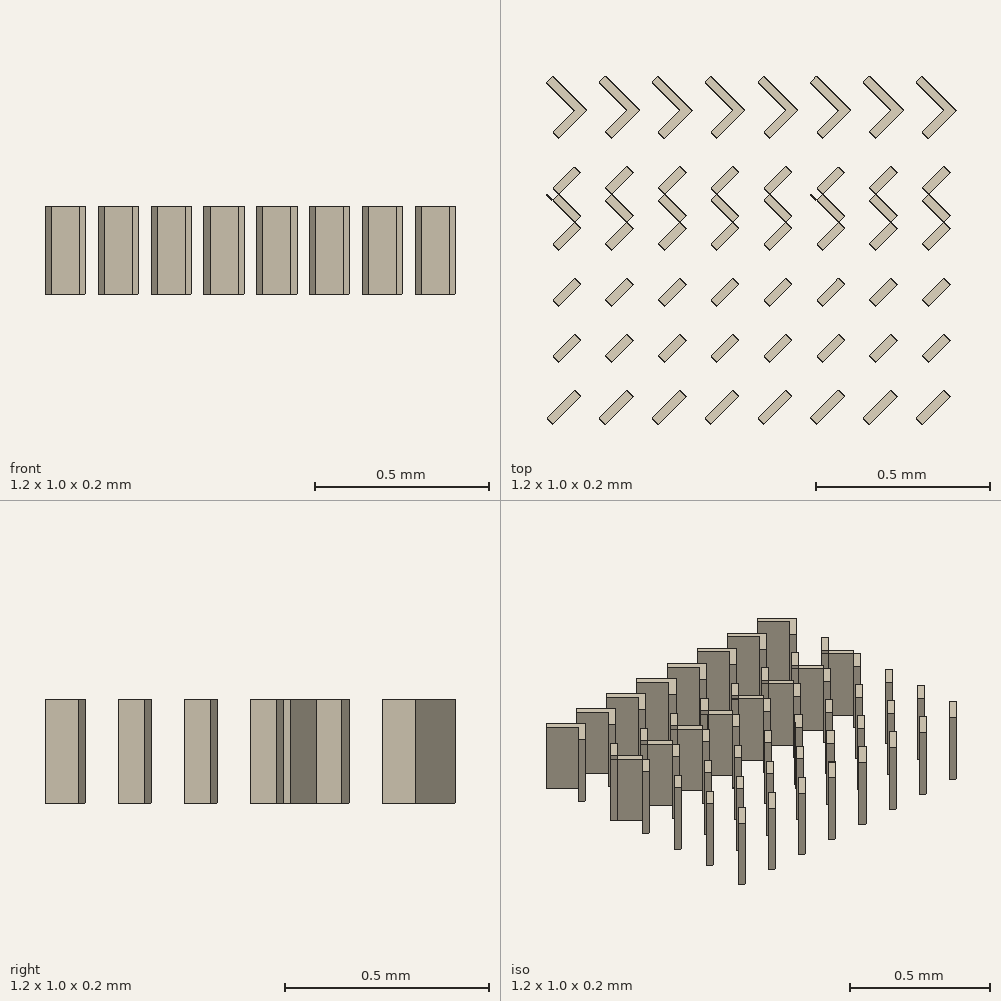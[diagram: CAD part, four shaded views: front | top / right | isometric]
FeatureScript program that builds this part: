
annotation { "Feature Type Name" : "Feature", "Feature Type Description" : "" }
export const myFeature = defineFeature(function(context is Context, id is Id, definition is map)
    precondition{}
    {
        {
            var Q0;
            Q0=qCreatedBy(makeId("Top.planeOp"),FACE);
            var sketch = newSketch(context, id + "F0", { "sketchPlane" : qUnion([Q0])});
            skLineSegment(sketch, "E0.bottom", {"start": v(-3.83, 2.01) * mm, "end": v(-3.93, 2.1) * mm});
            skLineSegment(sketch, "E0.top", {"start": v(-3.81, 2.03) * mm, "end": v(-3.91, 2.13) * mm});
            skLineSegment(sketch, "E0.left", {"start": v(-3.9, 1.93) * mm, "end": v(-3.9, 1.95) * mm});
            skLineSegment(sketch, "E0.right", {"start": v(-3.93, 2.1) * mm, "end": v(-3.91, 2.13) * mm});
            skPoint(sketch, "E0.middle", {"position": v(-3.95, 1.99) * mm});
            skLineSegment(sketch, "E1.bottom", {"start": v(-3.93, 1.95) * mm, "end": v(-3.83, 2.05) * mm});
            skLineSegment(sketch, "E1.top", {"start": v(-3.91, 1.93) * mm, "end": v(-3.81, 2.03) * mm});
            skLineSegment(sketch, "E1.left", {"start": v(-3.93, 1.95) * mm, "end": v(-3.91, 1.93) * mm});
            skLineSegment(sketch, "E1.right", {"start": v(-3.83, 2.05) * mm, "end": v(-3.81, 2.03) * mm});
            skPoint(sketch, "E1.middle", {"position": v(-3.87, 1.99) * mm});
            skLineSegment(sketch, "E2.bottom", {"start": v(-3.83, 1.85) * mm, "end": v(-3.93, 1.95) * mm});
            skLineSegment(sketch, "E2.top", {"start": v(-3.81, 1.87) * mm, "end": v(-3.91, 1.97) * mm});
            skLineSegment(sketch, "E2.left", {"start": v(-3.9, 1.77) * mm, "end": v(-3.9, 1.79) * mm});
            skLineSegment(sketch, "E2.right", {"start": v(-3.93, 1.95) * mm, "end": v(-3.91, 1.97) * mm});
            skPoint(sketch, "E2.middle", {"position": v(-3.95, 1.83) * mm});
            skLineSegment(sketch, "E3.bottom", {"start": v(-3.93, 1.79) * mm, "end": v(-3.83, 1.89) * mm});
            skLineSegment(sketch, "E3.top", {"start": v(-3.91, 1.77) * mm, "end": v(-3.81, 1.87) * mm});
            skLineSegment(sketch, "E3.left", {"start": v(-3.93, 1.79) * mm, "end": v(-3.91, 1.77) * mm});
            skLineSegment(sketch, "E3.right", {"start": v(-3.83, 1.89) * mm, "end": v(-3.81, 1.87) * mm});
            skPoint(sketch, "E3.middle", {"position": v(-3.87, 1.83) * mm});
            skLineSegment(sketch, "E4.bottom", {"start": v(-3.83, 1.69) * mm, "end": v(-3.93, 1.79) * mm});
            skLineSegment(sketch, "E4.top", {"start": v(-3.81, 1.7) * mm, "end": v(-3.9, 1.8) * mm});
            skLineSegment(sketch, "E4.left", {"start": v(-3.9, 1.6) * mm, "end": v(-3.9, 1.62) * mm});
            skLineSegment(sketch, "E4.right", {"start": v(-3.93, 1.79) * mm, "end": v(-3.9, 1.8) * mm});
            skPoint(sketch, "E4.middle", {"position": v(-3.95, 1.67) * mm});
            skLineSegment(sketch, "E5.bottom", {"start": v(-3.93, 1.63) * mm, "end": v(-3.83, 1.72) * mm});
            skLineSegment(sketch, "E5.top", {"start": v(-3.9, 1.6) * mm, "end": v(-3.81, 1.7) * mm});
            skLineSegment(sketch, "E5.left", {"start": v(-3.93, 1.63) * mm, "end": v(-3.9, 1.6) * mm});
            skLineSegment(sketch, "E5.right", {"start": v(-3.83, 1.72) * mm, "end": v(-3.81, 1.7) * mm});
            skPoint(sketch, "E5.middle", {"position": v(-3.87, 1.67) * mm});
            skLineSegment(sketch, "E6.bottom", {"start": v(-3.83, 1.53) * mm, "end": v(-3.93, 1.63) * mm});
            skLineSegment(sketch, "E6.top", {"start": v(-3.81, 1.54) * mm, "end": v(-3.9, 1.64) * mm});
            skLineSegment(sketch, "E6.left", {"start": v(-3.9, 1.45) * mm, "end": v(-3.9, 1.46) * mm});
            skLineSegment(sketch, "E6.right", {"start": v(-3.93, 1.63) * mm, "end": v(-3.9, 1.64) * mm});
            skPoint(sketch, "E6.middle", {"position": v(-3.95, 1.5) * mm});
            skLineSegment(sketch, "E7.bottom", {"start": v(-3.93, 1.46) * mm, "end": v(-3.83, 1.56) * mm});
            skLineSegment(sketch, "E7.top", {"start": v(-3.9, 1.45) * mm, "end": v(-3.81, 1.54) * mm});
            skLineSegment(sketch, "E7.left", {"start": v(-3.93, 1.46) * mm, "end": v(-3.9, 1.45) * mm});
            skLineSegment(sketch, "E7.right", {"start": v(-3.83, 1.56) * mm, "end": v(-3.81, 1.54) * mm});
            skPoint(sketch, "E7.middle", {"position": v(-3.87, 1.5) * mm});
            skLineSegment(sketch, "E8.bottom", {"start": v(-3.83, 1.36) * mm, "end": v(-3.93, 1.46) * mm});
            skLineSegment(sketch, "E8.top", {"start": v(-3.81, 1.38) * mm, "end": v(-3.9, 1.48) * mm});
            skLineSegment(sketch, "E8.left", {"start": v(-3.9, 1.28) * mm, "end": v(-3.9, 1.3) * mm});
            skLineSegment(sketch, "E8.right", {"start": v(-3.93, 1.46) * mm, "end": v(-3.9, 1.48) * mm});
            skPoint(sketch, "E8.middle", {"position": v(-3.95, 1.34) * mm});
            skLineSegment(sketch, "E9.bottom", {"start": v(-3.93, 1.3) * mm, "end": v(-3.83, 1.4) * mm});
            skLineSegment(sketch, "E9.top", {"start": v(-3.9, 1.28) * mm, "end": v(-3.81, 1.38) * mm});
            skLineSegment(sketch, "E9.left", {"start": v(-3.93, 1.3) * mm, "end": v(-3.9, 1.28) * mm});
            skLineSegment(sketch, "E9.right", {"start": v(-3.83, 1.4) * mm, "end": v(-3.81, 1.38) * mm});
            skPoint(sketch, "E9.middle", {"position": v(-3.87, 1.34) * mm});
            skLineSegment(sketch, "E10.bottom", {"start": v(-3.83, 1.2) * mm, "end": v(-3.93, 1.3) * mm});
            skLineSegment(sketch, "E10.top", {"start": v(-3.81, 1.22) * mm, "end": v(-3.9, 1.32) * mm});
            skLineSegment(sketch, "E10.left", {"start": v(-3.9, 1.12) * mm, "end": v(-3.9, 1.14) * mm});
            skLineSegment(sketch, "E10.right", {"start": v(-3.93, 1.3) * mm, "end": v(-3.9, 1.32) * mm});
            skPoint(sketch, "E10.middle", {"position": v(-3.95, 1.18) * mm});
            skLineSegment(sketch, "E11.bottom", {"start": v(-3.93, 1.14) * mm, "end": v(-3.83, 1.24) * mm});
            skLineSegment(sketch, "E11.top", {"start": v(-3.9, 1.12) * mm, "end": v(-3.81, 1.22) * mm});
            skLineSegment(sketch, "E11.left", {"start": v(-3.93, 1.14) * mm, "end": v(-3.9, 1.12) * mm});
            skLineSegment(sketch, "E11.right", {"start": v(-3.83, 1.24) * mm, "end": v(-3.81, 1.22) * mm});
            skPoint(sketch, "E11.middle", {"position": v(-3.87, 1.18) * mm});
            skLineSegment(sketch, "E12.0.1.0", {"start": v(-3.83, 3.56) * mm, "end": v(-3.93, 3.66) * mm});
            skLineSegment(sketch, "E12.0.1.1", {"start": v(-3.83, 3.24) * mm, "end": v(-3.93, 3.33) * mm});
            skPoint(sketch, "E12.0.1.2", {"position": v(-3.87, 4.02) * mm});
            skLineSegment(sketch, "E12.0.1.3", {"start": v(-3.81, 4.06) * mm, "end": v(-3.91, 4.16) * mm});
            skPoint(sketch, "E12.0.1.4", {"position": v(-3.95, 3.37) * mm});
            skLineSegment(sketch, "E12.0.1.5", {"start": v(-3.83, 4.04) * mm, "end": v(-3.93, 4.14) * mm});
            skPoint(sketch, "E12.0.1.6", {"position": v(-3.95, 3.54) * mm});
            skPoint(sketch, "E12.0.1.7", {"position": v(-3.95, 3.86) * mm});
            skPoint(sketch, "E12.0.1.8", {"position": v(-3.87, 3.37) * mm});
            skPoint(sketch, "E12.0.1.9", {"position": v(-3.87, 3.7) * mm});
            skLineSegment(sketch, "E12.0.1.10", {"start": v(-3.83, 3.4) * mm, "end": v(-3.93, 3.5) * mm});
            skPoint(sketch, "E12.0.1.11", {"position": v(-3.87, 3.54) * mm});
            skPoint(sketch, "E12.0.1.12", {"position": v(-3.87, 3.21) * mm});
            skLineSegment(sketch, "E12.0.1.13", {"start": v(-3.83, 3.72) * mm, "end": v(-3.93, 3.82) * mm});
            skPoint(sketch, "E12.0.1.14", {"position": v(-3.95, 4.02) * mm});
            skPoint(sketch, "E12.0.1.15", {"position": v(-3.95, 3.7) * mm});
            skLineSegment(sketch, "E12.0.1.16", {"start": v(-3.83, 3.88) * mm, "end": v(-3.93, 3.98) * mm});
            skPoint(sketch, "E12.0.1.17", {"position": v(-3.95, 3.21) * mm});
            skPoint(sketch, "E12.0.1.18", {"position": v(-3.87, 3.86) * mm});
            skLineSegment(sketch, "E12.0.1.19", {"start": v(-3.81, 3.41) * mm, "end": v(-3.9, 3.51) * mm});
            skLineSegment(sketch, "E12.0.1.20", {"start": v(-3.93, 3.98) * mm, "end": v(-3.83, 4.08) * mm});
            skLineSegment(sketch, "E12.0.1.21", {"start": v(-3.91, 3.8) * mm, "end": v(-3.81, 3.9) * mm});
            skLineSegment(sketch, "E12.0.1.22", {"start": v(-3.81, 3.58) * mm, "end": v(-3.9, 3.68) * mm});
            skLineSegment(sketch, "E12.0.1.23", {"start": v(-3.9, 3.32) * mm, "end": v(-3.81, 3.41) * mm});
            skLineSegment(sketch, "E12.0.1.24", {"start": v(-3.9, 3.64) * mm, "end": v(-3.81, 3.74) * mm});
            skLineSegment(sketch, "E12.0.1.25", {"start": v(-3.93, 3.5) * mm, "end": v(-3.83, 3.6) * mm});
            skLineSegment(sketch, "E12.0.1.26", {"start": v(-3.93, 3.17) * mm, "end": v(-3.83, 3.27) * mm});
            skLineSegment(sketch, "E12.0.1.27", {"start": v(-3.9, 3.48) * mm, "end": v(-3.81, 3.58) * mm});
            skLineSegment(sketch, "E12.0.1.28", {"start": v(-3.93, 3.33) * mm, "end": v(-3.83, 3.43) * mm});
            skLineSegment(sketch, "E12.0.1.29", {"start": v(-3.9, 3.15) * mm, "end": v(-3.81, 3.25) * mm});
            skLineSegment(sketch, "E12.0.1.30", {"start": v(-3.93, 3.66) * mm, "end": v(-3.83, 3.76) * mm});
            skLineSegment(sketch, "E12.0.1.31", {"start": v(-3.93, 3.82) * mm, "end": v(-3.83, 3.92) * mm});
            skLineSegment(sketch, "E12.0.1.32", {"start": v(-3.91, 3.96) * mm, "end": v(-3.81, 4.06) * mm});
            skLineSegment(sketch, "E12.0.1.33", {"start": v(-3.93, 4.14) * mm, "end": v(-3.91, 4.16) * mm});
            skLineSegment(sketch, "E12.0.1.34", {"start": v(-3.81, 3.74) * mm, "end": v(-3.9, 3.84) * mm});
            skLineSegment(sketch, "E12.0.1.35", {"start": v(-3.81, 3.25) * mm, "end": v(-3.9, 3.35) * mm});
            skLineSegment(sketch, "E12.0.1.36", {"start": v(-3.81, 3.9) * mm, "end": v(-3.91, 4) * mm});
            skLineSegment(sketch, "E12.0.1.37", {"start": v(-3.83, 3.92) * mm, "end": v(-3.81, 3.9) * mm});
            skLineSegment(sketch, "E12.0.1.38", {"start": v(-3.83, 3.6) * mm, "end": v(-3.81, 3.58) * mm});
            skLineSegment(sketch, "E12.0.1.39", {"start": v(-3.83, 3.27) * mm, "end": v(-3.81, 3.25) * mm});
            skLineSegment(sketch, "E12.0.1.40", {"start": v(-3.83, 3.76) * mm, "end": v(-3.81, 3.74) * mm});
            skLineSegment(sketch, "E12.0.1.41", {"start": v(-3.83, 3.43) * mm, "end": v(-3.81, 3.41) * mm});
            skLineSegment(sketch, "E12.0.1.42", {"start": v(-3.83, 4.08) * mm, "end": v(-3.81, 4.06) * mm});
            skLineSegment(sketch, "E12.0.1.43", {"start": v(-3.93, 3.82) * mm, "end": v(-3.9, 3.84) * mm});
            skLineSegment(sketch, "E12.0.1.44", {"start": v(-3.93, 3.82) * mm, "end": v(-3.91, 3.8) * mm});
            skLineSegment(sketch, "E12.0.1.45", {"start": v(-3.93, 3.17) * mm, "end": v(-3.9, 3.15) * mm});
            skLineSegment(sketch, "E12.0.1.46", {"start": v(-3.9, 3.8) * mm, "end": v(-3.9, 3.82) * mm});
            skLineSegment(sketch, "E12.0.1.47", {"start": v(-3.9, 3.15) * mm, "end": v(-3.9, 3.17) * mm});
            skLineSegment(sketch, "E12.0.1.48", {"start": v(-3.9, 3.96) * mm, "end": v(-3.9, 3.98) * mm});
            skLineSegment(sketch, "E12.0.1.49", {"start": v(-3.93, 3.33) * mm, "end": v(-3.9, 3.32) * mm});
            skLineSegment(sketch, "E12.0.1.50", {"start": v(-3.93, 3.66) * mm, "end": v(-3.9, 3.64) * mm});
            skLineSegment(sketch, "E12.0.1.51", {"start": v(-3.9, 3.64) * mm, "end": v(-3.9, 3.66) * mm});
            skLineSegment(sketch, "E12.0.1.52", {"start": v(-3.93, 3.5) * mm, "end": v(-3.9, 3.48) * mm});
            skLineSegment(sketch, "E12.0.1.53", {"start": v(-3.93, 3.66) * mm, "end": v(-3.9, 3.68) * mm});
            skLineSegment(sketch, "E12.0.1.54", {"start": v(-3.93, 3.33) * mm, "end": v(-3.9, 3.35) * mm});
            skLineSegment(sketch, "E12.0.1.55", {"start": v(-3.93, 3.98) * mm, "end": v(-3.91, 4) * mm});
            skLineSegment(sketch, "E12.0.1.56", {"start": v(-3.93, 3.98) * mm, "end": v(-3.91, 3.96) * mm});
            skLineSegment(sketch, "E12.0.1.57", {"start": v(-3.93, 3.5) * mm, "end": v(-3.9, 3.51) * mm});
            skLineSegment(sketch, "E12.0.1.58", {"start": v(-3.9, 3.48) * mm, "end": v(-3.9, 3.5) * mm});
            skLineSegment(sketch, "E12.0.1.59", {"start": v(-3.9, 3.32) * mm, "end": v(-3.9, 3.33) * mm});
            skLineSegment(sketch, "E12.1.0.0", {"start": v(-3.68, 1.53) * mm, "end": v(-3.78, 1.63) * mm});
            skLineSegment(sketch, "E12.1.0.1", {"start": v(-3.68, 1.2) * mm, "end": v(-3.78, 1.3) * mm});
            skPoint(sketch, "E12.1.0.2", {"position": v(-3.72, 1.99) * mm});
            skLineSegment(sketch, "E12.1.0.3", {"start": v(-3.66, 2.03) * mm, "end": v(-3.76, 2.13) * mm});
            skPoint(sketch, "E12.1.0.4", {"position": v(-3.8, 1.34) * mm});
            skLineSegment(sketch, "E12.1.0.5", {"start": v(-3.68, 2.01) * mm, "end": v(-3.78, 2.1) * mm});
            skPoint(sketch, "E12.1.0.6", {"position": v(-3.8, 1.5) * mm});
            skPoint(sketch, "E12.1.0.7", {"position": v(-3.8, 1.83) * mm});
            skPoint(sketch, "E12.1.0.8", {"position": v(-3.72, 1.34) * mm});
            skPoint(sketch, "E12.1.0.9", {"position": v(-3.72, 1.67) * mm});
            skLineSegment(sketch, "E12.1.0.10", {"start": v(-3.68, 1.36) * mm, "end": v(-3.78, 1.46) * mm});
            skPoint(sketch, "E12.1.0.11", {"position": v(-3.72, 1.5) * mm});
            skPoint(sketch, "E12.1.0.12", {"position": v(-3.72, 1.18) * mm});
            skLineSegment(sketch, "E12.1.0.13", {"start": v(-3.68, 1.69) * mm, "end": v(-3.78, 1.79) * mm});
            skPoint(sketch, "E12.1.0.14", {"position": v(-3.8, 1.99) * mm});
            skPoint(sketch, "E12.1.0.15", {"position": v(-3.8, 1.67) * mm});
            skLineSegment(sketch, "E12.1.0.16", {"start": v(-3.68, 1.85) * mm, "end": v(-3.78, 1.95) * mm});
            skPoint(sketch, "E12.1.0.17", {"position": v(-3.8, 1.18) * mm});
            skPoint(sketch, "E12.1.0.18", {"position": v(-3.72, 1.83) * mm});
            skLineSegment(sketch, "E12.1.0.19", {"start": v(-3.66, 1.38) * mm, "end": v(-3.76, 1.48) * mm});
            skLineSegment(sketch, "E12.1.0.20", {"start": v(-3.78, 1.95) * mm, "end": v(-3.68, 2.05) * mm});
            skLineSegment(sketch, "E12.1.0.21", {"start": v(-3.76, 1.77) * mm, "end": v(-3.66, 1.87) * mm});
            skLineSegment(sketch, "E12.1.0.22", {"start": v(-3.66, 1.54) * mm, "end": v(-3.76, 1.64) * mm});
            skLineSegment(sketch, "E12.1.0.23", {"start": v(-3.76, 1.28) * mm, "end": v(-3.66, 1.38) * mm});
            skLineSegment(sketch, "E12.1.0.24", {"start": v(-3.76, 1.6) * mm, "end": v(-3.66, 1.7) * mm});
            skLineSegment(sketch, "E12.1.0.25", {"start": v(-3.78, 1.46) * mm, "end": v(-3.68, 1.56) * mm});
            skLineSegment(sketch, "E12.1.0.26", {"start": v(-3.78, 1.14) * mm, "end": v(-3.68, 1.24) * mm});
            skLineSegment(sketch, "E12.1.0.27", {"start": v(-3.76, 1.45) * mm, "end": v(-3.66, 1.54) * mm});
            skLineSegment(sketch, "E12.1.0.28", {"start": v(-3.78, 1.3) * mm, "end": v(-3.68, 1.4) * mm});
            skLineSegment(sketch, "E12.1.0.29", {"start": v(-3.76, 1.12) * mm, "end": v(-3.66, 1.22) * mm});
            skLineSegment(sketch, "E12.1.0.30", {"start": v(-3.78, 1.63) * mm, "end": v(-3.68, 1.72) * mm});
            skLineSegment(sketch, "E12.1.0.31", {"start": v(-3.78, 1.79) * mm, "end": v(-3.68, 1.89) * mm});
            skLineSegment(sketch, "E12.1.0.32", {"start": v(-3.76, 1.93) * mm, "end": v(-3.66, 2.03) * mm});
            skLineSegment(sketch, "E12.1.0.33", {"start": v(-3.78, 2.1) * mm, "end": v(-3.76, 2.13) * mm});
            skLineSegment(sketch, "E12.1.0.34", {"start": v(-3.66, 1.7) * mm, "end": v(-3.76, 1.8) * mm});
            skLineSegment(sketch, "E12.1.0.35", {"start": v(-3.66, 1.22) * mm, "end": v(-3.76, 1.32) * mm});
            skLineSegment(sketch, "E12.1.0.36", {"start": v(-3.66, 1.87) * mm, "end": v(-3.76, 1.97) * mm});
            skLineSegment(sketch, "E12.1.0.37", {"start": v(-3.68, 1.89) * mm, "end": v(-3.66, 1.87) * mm});
            skLineSegment(sketch, "E12.1.0.38", {"start": v(-3.68, 1.56) * mm, "end": v(-3.66, 1.54) * mm});
            skLineSegment(sketch, "E12.1.0.39", {"start": v(-3.68, 1.24) * mm, "end": v(-3.66, 1.22) * mm});
            skLineSegment(sketch, "E12.1.0.40", {"start": v(-3.68, 1.72) * mm, "end": v(-3.66, 1.7) * mm});
            skLineSegment(sketch, "E12.1.0.41", {"start": v(-3.68, 1.4) * mm, "end": v(-3.66, 1.38) * mm});
            skLineSegment(sketch, "E12.1.0.42", {"start": v(-3.68, 2.05) * mm, "end": v(-3.66, 2.03) * mm});
            skLineSegment(sketch, "E12.1.0.43", {"start": v(-3.78, 1.79) * mm, "end": v(-3.76, 1.8) * mm});
            skLineSegment(sketch, "E12.1.0.44", {"start": v(-3.78, 1.79) * mm, "end": v(-3.76, 1.77) * mm});
            skLineSegment(sketch, "E12.1.0.45", {"start": v(-3.78, 1.14) * mm, "end": v(-3.76, 1.12) * mm});
            skLineSegment(sketch, "E12.1.0.46", {"start": v(-3.76, 1.77) * mm, "end": v(-3.74, 1.79) * mm});
            skLineSegment(sketch, "E12.1.0.47", {"start": v(-3.76, 1.12) * mm, "end": v(-3.74, 1.14) * mm});
            skLineSegment(sketch, "E12.1.0.48", {"start": v(-3.76, 1.93) * mm, "end": v(-3.74, 1.95) * mm});
            skLineSegment(sketch, "E12.1.0.49", {"start": v(-3.78, 1.3) * mm, "end": v(-3.76, 1.28) * mm});
            skLineSegment(sketch, "E12.1.0.50", {"start": v(-3.78, 1.63) * mm, "end": v(-3.76, 1.6) * mm});
            skLineSegment(sketch, "E12.1.0.51", {"start": v(-3.76, 1.6) * mm, "end": v(-3.74, 1.62) * mm});
            skLineSegment(sketch, "E12.1.0.52", {"start": v(-3.78, 1.46) * mm, "end": v(-3.76, 1.45) * mm});
            skLineSegment(sketch, "E12.1.0.53", {"start": v(-3.78, 1.63) * mm, "end": v(-3.76, 1.64) * mm});
            skLineSegment(sketch, "E12.1.0.54", {"start": v(-3.78, 1.3) * mm, "end": v(-3.76, 1.32) * mm});
            skLineSegment(sketch, "E12.1.0.55", {"start": v(-3.78, 1.95) * mm, "end": v(-3.76, 1.97) * mm});
            skLineSegment(sketch, "E12.1.0.56", {"start": v(-3.78, 1.95) * mm, "end": v(-3.76, 1.93) * mm});
            skLineSegment(sketch, "E12.1.0.57", {"start": v(-3.78, 1.46) * mm, "end": v(-3.76, 1.48) * mm});
            skLineSegment(sketch, "E12.1.0.58", {"start": v(-3.76, 1.45) * mm, "end": v(-3.74, 1.46) * mm});
            skLineSegment(sketch, "E12.1.0.59", {"start": v(-3.76, 1.28) * mm, "end": v(-3.74, 1.3) * mm});
            skLineSegment(sketch, "E12.1.1.0", {"start": v(-3.68, 3.56) * mm, "end": v(-3.78, 3.66) * mm});
            skLineSegment(sketch, "E12.1.1.1", {"start": v(-3.68, 3.24) * mm, "end": v(-3.78, 3.33) * mm});
            skPoint(sketch, "E12.1.1.2", {"position": v(-3.72, 4.02) * mm});
            skLineSegment(sketch, "E12.1.1.3", {"start": v(-3.66, 4.06) * mm, "end": v(-3.76, 4.16) * mm});
            skPoint(sketch, "E12.1.1.4", {"position": v(-3.8, 3.37) * mm});
            skLineSegment(sketch, "E12.1.1.5", {"start": v(-3.68, 4.04) * mm, "end": v(-3.78, 4.14) * mm});
            skPoint(sketch, "E12.1.1.6", {"position": v(-3.8, 3.54) * mm});
            skPoint(sketch, "E12.1.1.7", {"position": v(-3.8, 3.86) * mm});
            skPoint(sketch, "E12.1.1.8", {"position": v(-3.72, 3.37) * mm});
            skPoint(sketch, "E12.1.1.9", {"position": v(-3.72, 3.7) * mm});
            skLineSegment(sketch, "E12.1.1.10", {"start": v(-3.68, 3.4) * mm, "end": v(-3.78, 3.5) * mm});
            skPoint(sketch, "E12.1.1.11", {"position": v(-3.72, 3.54) * mm});
            skPoint(sketch, "E12.1.1.12", {"position": v(-3.72, 3.21) * mm});
            skLineSegment(sketch, "E12.1.1.13", {"start": v(-3.68, 3.72) * mm, "end": v(-3.78, 3.82) * mm});
            skPoint(sketch, "E12.1.1.14", {"position": v(-3.8, 4.02) * mm});
            skPoint(sketch, "E12.1.1.15", {"position": v(-3.8, 3.7) * mm});
            skLineSegment(sketch, "E12.1.1.16", {"start": v(-3.68, 3.88) * mm, "end": v(-3.78, 3.98) * mm});
            skPoint(sketch, "E12.1.1.17", {"position": v(-3.8, 3.21) * mm});
            skPoint(sketch, "E12.1.1.18", {"position": v(-3.72, 3.86) * mm});
            skLineSegment(sketch, "E12.1.1.19", {"start": v(-3.66, 3.41) * mm, "end": v(-3.76, 3.51) * mm});
            skLineSegment(sketch, "E12.1.1.20", {"start": v(-3.78, 3.98) * mm, "end": v(-3.68, 4.08) * mm});
            skLineSegment(sketch, "E12.1.1.21", {"start": v(-3.76, 3.8) * mm, "end": v(-3.66, 3.9) * mm});
            skLineSegment(sketch, "E12.1.1.22", {"start": v(-3.66, 3.58) * mm, "end": v(-3.76, 3.68) * mm});
            skLineSegment(sketch, "E12.1.1.23", {"start": v(-3.76, 3.32) * mm, "end": v(-3.66, 3.41) * mm});
            skLineSegment(sketch, "E12.1.1.24", {"start": v(-3.76, 3.64) * mm, "end": v(-3.66, 3.74) * mm});
            skLineSegment(sketch, "E12.1.1.25", {"start": v(-3.78, 3.5) * mm, "end": v(-3.68, 3.6) * mm});
            skLineSegment(sketch, "E12.1.1.26", {"start": v(-3.78, 3.17) * mm, "end": v(-3.68, 3.27) * mm});
            skLineSegment(sketch, "E12.1.1.27", {"start": v(-3.76, 3.48) * mm, "end": v(-3.66, 3.58) * mm});
            skLineSegment(sketch, "E12.1.1.28", {"start": v(-3.78, 3.33) * mm, "end": v(-3.68, 3.43) * mm});
            skLineSegment(sketch, "E12.1.1.29", {"start": v(-3.76, 3.15) * mm, "end": v(-3.66, 3.25) * mm});
            skLineSegment(sketch, "E12.1.1.30", {"start": v(-3.78, 3.66) * mm, "end": v(-3.68, 3.76) * mm});
            skLineSegment(sketch, "E12.1.1.31", {"start": v(-3.78, 3.82) * mm, "end": v(-3.68, 3.92) * mm});
            skLineSegment(sketch, "E12.1.1.32", {"start": v(-3.76, 3.96) * mm, "end": v(-3.66, 4.06) * mm});
            skLineSegment(sketch, "E12.1.1.33", {"start": v(-3.78, 4.14) * mm, "end": v(-3.76, 4.16) * mm});
            skLineSegment(sketch, "E12.1.1.34", {"start": v(-3.66, 3.74) * mm, "end": v(-3.76, 3.84) * mm});
            skLineSegment(sketch, "E12.1.1.35", {"start": v(-3.66, 3.25) * mm, "end": v(-3.76, 3.35) * mm});
            skLineSegment(sketch, "E12.1.1.36", {"start": v(-3.66, 3.9) * mm, "end": v(-3.76, 4) * mm});
            skLineSegment(sketch, "E12.1.1.37", {"start": v(-3.68, 3.92) * mm, "end": v(-3.66, 3.9) * mm});
            skLineSegment(sketch, "E12.1.1.38", {"start": v(-3.68, 3.6) * mm, "end": v(-3.66, 3.58) * mm});
            skLineSegment(sketch, "E12.1.1.39", {"start": v(-3.68, 3.27) * mm, "end": v(-3.66, 3.25) * mm});
            skLineSegment(sketch, "E12.1.1.40", {"start": v(-3.68, 3.76) * mm, "end": v(-3.66, 3.74) * mm});
            skLineSegment(sketch, "E12.1.1.41", {"start": v(-3.68, 3.43) * mm, "end": v(-3.66, 3.41) * mm});
            skLineSegment(sketch, "E12.1.1.42", {"start": v(-3.68, 4.08) * mm, "end": v(-3.66, 4.06) * mm});
            skLineSegment(sketch, "E12.1.1.43", {"start": v(-3.78, 3.82) * mm, "end": v(-3.76, 3.84) * mm});
            skLineSegment(sketch, "E12.1.1.44", {"start": v(-3.78, 3.82) * mm, "end": v(-3.76, 3.8) * mm});
            skLineSegment(sketch, "E12.1.1.45", {"start": v(-3.78, 3.17) * mm, "end": v(-3.76, 3.15) * mm});
            skLineSegment(sketch, "E12.1.1.46", {"start": v(-3.76, 3.8) * mm, "end": v(-3.74, 3.82) * mm});
            skLineSegment(sketch, "E12.1.1.47", {"start": v(-3.76, 3.15) * mm, "end": v(-3.74, 3.17) * mm});
            skLineSegment(sketch, "E12.1.1.48", {"start": v(-3.76, 3.96) * mm, "end": v(-3.74, 3.98) * mm});
            skLineSegment(sketch, "E12.1.1.49", {"start": v(-3.78, 3.33) * mm, "end": v(-3.76, 3.32) * mm});
            skLineSegment(sketch, "E12.1.1.50", {"start": v(-3.78, 3.66) * mm, "end": v(-3.76, 3.64) * mm});
            skLineSegment(sketch, "E12.1.1.51", {"start": v(-3.76, 3.64) * mm, "end": v(-3.74, 3.66) * mm});
            skLineSegment(sketch, "E12.1.1.52", {"start": v(-3.78, 3.5) * mm, "end": v(-3.76, 3.48) * mm});
            skLineSegment(sketch, "E12.1.1.53", {"start": v(-3.78, 3.66) * mm, "end": v(-3.76, 3.68) * mm});
            skLineSegment(sketch, "E12.1.1.54", {"start": v(-3.78, 3.33) * mm, "end": v(-3.76, 3.35) * mm});
            skLineSegment(sketch, "E12.1.1.55", {"start": v(-3.78, 3.98) * mm, "end": v(-3.76, 4) * mm});
            skLineSegment(sketch, "E12.1.1.56", {"start": v(-3.78, 3.98) * mm, "end": v(-3.76, 3.96) * mm});
            skLineSegment(sketch, "E12.1.1.57", {"start": v(-3.78, 3.5) * mm, "end": v(-3.76, 3.51) * mm});
            skLineSegment(sketch, "E12.1.1.58", {"start": v(-3.76, 3.48) * mm, "end": v(-3.74, 3.5) * mm});
            skLineSegment(sketch, "E12.1.1.59", {"start": v(-3.76, 3.32) * mm, "end": v(-3.74, 3.33) * mm});
            skLineSegment(sketch, "E12.2.0.0", {"start": v(-3.52, 1.53) * mm, "end": v(-3.62, 1.63) * mm});
            skLineSegment(sketch, "E12.2.0.1", {"start": v(-3.52, 1.2) * mm, "end": v(-3.62, 1.3) * mm});
            skPoint(sketch, "E12.2.0.2", {"position": v(-3.56, 1.99) * mm});
            skLineSegment(sketch, "E12.2.0.3", {"start": v(-3.5, 2.03) * mm, "end": v(-3.6, 2.13) * mm});
            skPoint(sketch, "E12.2.0.4", {"position": v(-3.65, 1.34) * mm});
            skLineSegment(sketch, "E12.2.0.5", {"start": v(-3.52, 2.01) * mm, "end": v(-3.62, 2.1) * mm});
            skPoint(sketch, "E12.2.0.6", {"position": v(-3.65, 1.5) * mm});
            skPoint(sketch, "E12.2.0.7", {"position": v(-3.65, 1.83) * mm});
            skPoint(sketch, "E12.2.0.8", {"position": v(-3.56, 1.34) * mm});
            skPoint(sketch, "E12.2.0.9", {"position": v(-3.56, 1.67) * mm});
            skLineSegment(sketch, "E12.2.0.10", {"start": v(-3.52, 1.36) * mm, "end": v(-3.62, 1.46) * mm});
            skPoint(sketch, "E12.2.0.11", {"position": v(-3.56, 1.5) * mm});
            skPoint(sketch, "E12.2.0.12", {"position": v(-3.56, 1.18) * mm});
            skLineSegment(sketch, "E12.2.0.13", {"start": v(-3.52, 1.69) * mm, "end": v(-3.62, 1.79) * mm});
            skPoint(sketch, "E12.2.0.14", {"position": v(-3.65, 1.99) * mm});
            skPoint(sketch, "E12.2.0.15", {"position": v(-3.65, 1.67) * mm});
            skLineSegment(sketch, "E12.2.0.16", {"start": v(-3.52, 1.85) * mm, "end": v(-3.62, 1.95) * mm});
            skPoint(sketch, "E12.2.0.17", {"position": v(-3.65, 1.18) * mm});
            skPoint(sketch, "E12.2.0.18", {"position": v(-3.56, 1.83) * mm});
            skLineSegment(sketch, "E12.2.0.19", {"start": v(-3.5, 1.38) * mm, "end": v(-3.6, 1.48) * mm});
            skLineSegment(sketch, "E12.2.0.20", {"start": v(-3.62, 1.95) * mm, "end": v(-3.52, 2.05) * mm});
            skLineSegment(sketch, "E12.2.0.21", {"start": v(-3.6, 1.77) * mm, "end": v(-3.5, 1.87) * mm});
            skLineSegment(sketch, "E12.2.0.22", {"start": v(-3.5, 1.54) * mm, "end": v(-3.6, 1.64) * mm});
            skLineSegment(sketch, "E12.2.0.23", {"start": v(-3.6, 1.28) * mm, "end": v(-3.5, 1.38) * mm});
            skLineSegment(sketch, "E12.2.0.24", {"start": v(-3.6, 1.6) * mm, "end": v(-3.5, 1.7) * mm});
            skLineSegment(sketch, "E12.2.0.25", {"start": v(-3.62, 1.46) * mm, "end": v(-3.52, 1.56) * mm});
            skLineSegment(sketch, "E12.2.0.26", {"start": v(-3.62, 1.14) * mm, "end": v(-3.52, 1.24) * mm});
            skLineSegment(sketch, "E12.2.0.27", {"start": v(-3.6, 1.45) * mm, "end": v(-3.5, 1.54) * mm});
            skLineSegment(sketch, "E12.2.0.28", {"start": v(-3.62, 1.3) * mm, "end": v(-3.52, 1.4) * mm});
            skLineSegment(sketch, "E12.2.0.29", {"start": v(-3.6, 1.12) * mm, "end": v(-3.5, 1.22) * mm});
            skLineSegment(sketch, "E12.2.0.30", {"start": v(-3.62, 1.63) * mm, "end": v(-3.52, 1.72) * mm});
            skLineSegment(sketch, "E12.2.0.31", {"start": v(-3.62, 1.79) * mm, "end": v(-3.52, 1.89) * mm});
            skLineSegment(sketch, "E12.2.0.32", {"start": v(-3.6, 1.93) * mm, "end": v(-3.5, 2.03) * mm});
            skLineSegment(sketch, "E12.2.0.33", {"start": v(-3.62, 2.1) * mm, "end": v(-3.6, 2.13) * mm});
            skLineSegment(sketch, "E12.2.0.34", {"start": v(-3.5, 1.7) * mm, "end": v(-3.6, 1.8) * mm});
            skLineSegment(sketch, "E12.2.0.35", {"start": v(-3.5, 1.22) * mm, "end": v(-3.6, 1.32) * mm});
            skLineSegment(sketch, "E12.2.0.36", {"start": v(-3.5, 1.87) * mm, "end": v(-3.6, 1.97) * mm});
            skLineSegment(sketch, "E12.2.0.37", {"start": v(-3.52, 1.89) * mm, "end": v(-3.5, 1.87) * mm});
            skLineSegment(sketch, "E12.2.0.38", {"start": v(-3.52, 1.56) * mm, "end": v(-3.5, 1.54) * mm});
            skLineSegment(sketch, "E12.2.0.39", {"start": v(-3.52, 1.24) * mm, "end": v(-3.5, 1.22) * mm});
            skLineSegment(sketch, "E12.2.0.40", {"start": v(-3.52, 1.72) * mm, "end": v(-3.5, 1.7) * mm});
            skLineSegment(sketch, "E12.2.0.41", {"start": v(-3.52, 1.4) * mm, "end": v(-3.5, 1.38) * mm});
            skLineSegment(sketch, "E12.2.0.42", {"start": v(-3.52, 2.05) * mm, "end": v(-3.5, 2.03) * mm});
            skLineSegment(sketch, "E12.2.0.43", {"start": v(-3.62, 1.79) * mm, "end": v(-3.6, 1.8) * mm});
            skLineSegment(sketch, "E12.2.0.44", {"start": v(-3.62, 1.79) * mm, "end": v(-3.6, 1.77) * mm});
            skLineSegment(sketch, "E12.2.0.45", {"start": v(-3.62, 1.14) * mm, "end": v(-3.6, 1.12) * mm});
            skLineSegment(sketch, "E12.2.0.46", {"start": v(-3.6, 1.77) * mm, "end": v(-3.59, 1.79) * mm});
            skLineSegment(sketch, "E12.2.0.47", {"start": v(-3.6, 1.12) * mm, "end": v(-3.59, 1.14) * mm});
            skLineSegment(sketch, "E12.2.0.48", {"start": v(-3.6, 1.93) * mm, "end": v(-3.59, 1.95) * mm});
            skLineSegment(sketch, "E12.2.0.49", {"start": v(-3.62, 1.3) * mm, "end": v(-3.6, 1.28) * mm});
            skLineSegment(sketch, "E12.2.0.50", {"start": v(-3.62, 1.63) * mm, "end": v(-3.6, 1.6) * mm});
            skLineSegment(sketch, "E12.2.0.51", {"start": v(-3.6, 1.6) * mm, "end": v(-3.59, 1.62) * mm});
            skLineSegment(sketch, "E12.2.0.52", {"start": v(-3.62, 1.46) * mm, "end": v(-3.6, 1.45) * mm});
            skLineSegment(sketch, "E12.2.0.53", {"start": v(-3.62, 1.63) * mm, "end": v(-3.6, 1.64) * mm});
            skLineSegment(sketch, "E12.2.0.54", {"start": v(-3.62, 1.3) * mm, "end": v(-3.6, 1.32) * mm});
            skLineSegment(sketch, "E12.2.0.55", {"start": v(-3.62, 1.95) * mm, "end": v(-3.6, 1.97) * mm});
            skLineSegment(sketch, "E12.2.0.56", {"start": v(-3.62, 1.95) * mm, "end": v(-3.6, 1.93) * mm});
            skLineSegment(sketch, "E12.2.0.57", {"start": v(-3.62, 1.46) * mm, "end": v(-3.6, 1.48) * mm});
            skLineSegment(sketch, "E12.2.0.58", {"start": v(-3.6, 1.45) * mm, "end": v(-3.59, 1.46) * mm});
            skLineSegment(sketch, "E12.2.0.59", {"start": v(-3.6, 1.28) * mm, "end": v(-3.59, 1.3) * mm});
            skLineSegment(sketch, "E12.2.1.0", {"start": v(-3.52, 3.56) * mm, "end": v(-3.62, 3.66) * mm});
            skLineSegment(sketch, "E12.2.1.1", {"start": v(-3.52, 3.24) * mm, "end": v(-3.62, 3.33) * mm});
            skPoint(sketch, "E12.2.1.2", {"position": v(-3.56, 4.02) * mm});
            skLineSegment(sketch, "E12.2.1.3", {"start": v(-3.5, 4.06) * mm, "end": v(-3.6, 4.16) * mm});
            skPoint(sketch, "E12.2.1.4", {"position": v(-3.65, 3.37) * mm});
            skLineSegment(sketch, "E12.2.1.5", {"start": v(-3.52, 4.04) * mm, "end": v(-3.62, 4.14) * mm});
            skPoint(sketch, "E12.2.1.6", {"position": v(-3.65, 3.54) * mm});
            skPoint(sketch, "E12.2.1.7", {"position": v(-3.65, 3.86) * mm});
            skPoint(sketch, "E12.2.1.8", {"position": v(-3.56, 3.37) * mm});
            skPoint(sketch, "E12.2.1.9", {"position": v(-3.56, 3.7) * mm});
            skLineSegment(sketch, "E12.2.1.10", {"start": v(-3.52, 3.4) * mm, "end": v(-3.62, 3.5) * mm});
            skPoint(sketch, "E12.2.1.11", {"position": v(-3.56, 3.54) * mm});
            skPoint(sketch, "E12.2.1.12", {"position": v(-3.56, 3.21) * mm});
            skLineSegment(sketch, "E12.2.1.13", {"start": v(-3.52, 3.72) * mm, "end": v(-3.62, 3.82) * mm});
            skPoint(sketch, "E12.2.1.14", {"position": v(-3.65, 4.02) * mm});
            skPoint(sketch, "E12.2.1.15", {"position": v(-3.65, 3.7) * mm});
            skLineSegment(sketch, "E12.2.1.16", {"start": v(-3.52, 3.88) * mm, "end": v(-3.62, 3.98) * mm});
            skPoint(sketch, "E12.2.1.17", {"position": v(-3.65, 3.21) * mm});
            skPoint(sketch, "E12.2.1.18", {"position": v(-3.56, 3.86) * mm});
            skLineSegment(sketch, "E12.2.1.19", {"start": v(-3.5, 3.41) * mm, "end": v(-3.6, 3.51) * mm});
            skLineSegment(sketch, "E12.2.1.20", {"start": v(-3.62, 3.98) * mm, "end": v(-3.52, 4.08) * mm});
            skLineSegment(sketch, "E12.2.1.21", {"start": v(-3.6, 3.8) * mm, "end": v(-3.5, 3.9) * mm});
            skLineSegment(sketch, "E12.2.1.22", {"start": v(-3.5, 3.58) * mm, "end": v(-3.6, 3.68) * mm});
            skLineSegment(sketch, "E12.2.1.23", {"start": v(-3.6, 3.32) * mm, "end": v(-3.5, 3.41) * mm});
            skLineSegment(sketch, "E12.2.1.24", {"start": v(-3.6, 3.64) * mm, "end": v(-3.5, 3.74) * mm});
            skLineSegment(sketch, "E12.2.1.25", {"start": v(-3.62, 3.5) * mm, "end": v(-3.52, 3.6) * mm});
            skLineSegment(sketch, "E12.2.1.26", {"start": v(-3.62, 3.17) * mm, "end": v(-3.52, 3.27) * mm});
            skLineSegment(sketch, "E12.2.1.27", {"start": v(-3.6, 3.48) * mm, "end": v(-3.5, 3.58) * mm});
            skLineSegment(sketch, "E12.2.1.28", {"start": v(-3.62, 3.33) * mm, "end": v(-3.52, 3.43) * mm});
            skLineSegment(sketch, "E12.2.1.29", {"start": v(-3.6, 3.15) * mm, "end": v(-3.5, 3.25) * mm});
            skLineSegment(sketch, "E12.2.1.30", {"start": v(-3.62, 3.66) * mm, "end": v(-3.52, 3.76) * mm});
            skLineSegment(sketch, "E12.2.1.31", {"start": v(-3.62, 3.82) * mm, "end": v(-3.52, 3.92) * mm});
            skLineSegment(sketch, "E12.2.1.32", {"start": v(-3.6, 3.96) * mm, "end": v(-3.5, 4.06) * mm});
            skLineSegment(sketch, "E12.2.1.33", {"start": v(-3.62, 4.14) * mm, "end": v(-3.6, 4.16) * mm});
            skLineSegment(sketch, "E12.2.1.34", {"start": v(-3.5, 3.74) * mm, "end": v(-3.6, 3.84) * mm});
            skLineSegment(sketch, "E12.2.1.35", {"start": v(-3.5, 3.25) * mm, "end": v(-3.6, 3.35) * mm});
            skLineSegment(sketch, "E12.2.1.36", {"start": v(-3.5, 3.9) * mm, "end": v(-3.6, 4) * mm});
            skLineSegment(sketch, "E12.2.1.37", {"start": v(-3.52, 3.92) * mm, "end": v(-3.5, 3.9) * mm});
            skLineSegment(sketch, "E12.2.1.38", {"start": v(-3.52, 3.6) * mm, "end": v(-3.5, 3.58) * mm});
            skLineSegment(sketch, "E12.2.1.39", {"start": v(-3.52, 3.27) * mm, "end": v(-3.5, 3.25) * mm});
            skLineSegment(sketch, "E12.2.1.40", {"start": v(-3.52, 3.76) * mm, "end": v(-3.5, 3.74) * mm});
            skLineSegment(sketch, "E12.2.1.41", {"start": v(-3.52, 3.43) * mm, "end": v(-3.5, 3.41) * mm});
            skLineSegment(sketch, "E12.2.1.42", {"start": v(-3.52, 4.08) * mm, "end": v(-3.5, 4.06) * mm});
            skLineSegment(sketch, "E12.2.1.43", {"start": v(-3.62, 3.82) * mm, "end": v(-3.6, 3.84) * mm});
            skLineSegment(sketch, "E12.2.1.44", {"start": v(-3.62, 3.82) * mm, "end": v(-3.6, 3.8) * mm});
            skLineSegment(sketch, "E12.2.1.45", {"start": v(-3.62, 3.17) * mm, "end": v(-3.6, 3.15) * mm});
            skLineSegment(sketch, "E12.2.1.46", {"start": v(-3.6, 3.8) * mm, "end": v(-3.59, 3.82) * mm});
            skLineSegment(sketch, "E12.2.1.47", {"start": v(-3.6, 3.15) * mm, "end": v(-3.59, 3.17) * mm});
            skLineSegment(sketch, "E12.2.1.48", {"start": v(-3.6, 3.96) * mm, "end": v(-3.59, 3.98) * mm});
            skLineSegment(sketch, "E12.2.1.49", {"start": v(-3.62, 3.33) * mm, "end": v(-3.6, 3.32) * mm});
            skLineSegment(sketch, "E12.2.1.50", {"start": v(-3.62, 3.66) * mm, "end": v(-3.6, 3.64) * mm});
            skLineSegment(sketch, "E12.2.1.51", {"start": v(-3.6, 3.64) * mm, "end": v(-3.59, 3.66) * mm});
            skLineSegment(sketch, "E12.2.1.52", {"start": v(-3.62, 3.5) * mm, "end": v(-3.6, 3.48) * mm});
            skLineSegment(sketch, "E12.2.1.53", {"start": v(-3.62, 3.66) * mm, "end": v(-3.6, 3.68) * mm});
            skLineSegment(sketch, "E12.2.1.54", {"start": v(-3.62, 3.33) * mm, "end": v(-3.6, 3.35) * mm});
            skLineSegment(sketch, "E12.2.1.55", {"start": v(-3.62, 3.98) * mm, "end": v(-3.6, 4) * mm});
            skLineSegment(sketch, "E12.2.1.56", {"start": v(-3.62, 3.98) * mm, "end": v(-3.6, 3.96) * mm});
            skLineSegment(sketch, "E12.2.1.57", {"start": v(-3.62, 3.5) * mm, "end": v(-3.6, 3.51) * mm});
            skLineSegment(sketch, "E12.2.1.58", {"start": v(-3.6, 3.48) * mm, "end": v(-3.59, 3.5) * mm});
            skLineSegment(sketch, "E12.2.1.59", {"start": v(-3.6, 3.32) * mm, "end": v(-3.59, 3.33) * mm});
            skLineSegment(sketch, "E12.3.0.0", {"start": v(-3.37, 1.53) * mm, "end": v(-3.47, 1.63) * mm});
            skLineSegment(sketch, "E12.3.0.1", {"start": v(-3.37, 1.2) * mm, "end": v(-3.47, 1.3) * mm});
            skPoint(sketch, "E12.3.0.2", {"position": v(-3.41, 1.99) * mm});
            skLineSegment(sketch, "E12.3.0.3", {"start": v(-3.35, 2.03) * mm, "end": v(-3.45, 2.13) * mm});
            skPoint(sketch, "E12.3.0.4", {"position": v(-3.5, 1.34) * mm});
            skLineSegment(sketch, "E12.3.0.5", {"start": v(-3.37, 2.01) * mm, "end": v(-3.47, 2.1) * mm});
            skPoint(sketch, "E12.3.0.6", {"position": v(-3.5, 1.5) * mm});
            skPoint(sketch, "E12.3.0.7", {"position": v(-3.5, 1.83) * mm});
            skPoint(sketch, "E12.3.0.8", {"position": v(-3.41, 1.34) * mm});
            skPoint(sketch, "E12.3.0.9", {"position": v(-3.41, 1.67) * mm});
            skLineSegment(sketch, "E12.3.0.10", {"start": v(-3.37, 1.36) * mm, "end": v(-3.47, 1.46) * mm});
            skPoint(sketch, "E12.3.0.11", {"position": v(-3.41, 1.5) * mm});
            skPoint(sketch, "E12.3.0.12", {"position": v(-3.41, 1.18) * mm});
            skLineSegment(sketch, "E12.3.0.13", {"start": v(-3.37, 1.69) * mm, "end": v(-3.47, 1.79) * mm});
            skPoint(sketch, "E12.3.0.14", {"position": v(-3.5, 1.99) * mm});
            skPoint(sketch, "E12.3.0.15", {"position": v(-3.5, 1.67) * mm});
            skLineSegment(sketch, "E12.3.0.16", {"start": v(-3.37, 1.85) * mm, "end": v(-3.47, 1.95) * mm});
            skPoint(sketch, "E12.3.0.17", {"position": v(-3.5, 1.18) * mm});
            skPoint(sketch, "E12.3.0.18", {"position": v(-3.41, 1.83) * mm});
            skLineSegment(sketch, "E12.3.0.19", {"start": v(-3.35, 1.38) * mm, "end": v(-3.45, 1.48) * mm});
            skLineSegment(sketch, "E12.3.0.20", {"start": v(-3.47, 1.95) * mm, "end": v(-3.37, 2.05) * mm});
            skLineSegment(sketch, "E12.3.0.21", {"start": v(-3.45, 1.77) * mm, "end": v(-3.35, 1.87) * mm});
            skLineSegment(sketch, "E12.3.0.22", {"start": v(-3.35, 1.54) * mm, "end": v(-3.45, 1.64) * mm});
            skLineSegment(sketch, "E12.3.0.23", {"start": v(-3.45, 1.28) * mm, "end": v(-3.35, 1.38) * mm});
            skLineSegment(sketch, "E12.3.0.24", {"start": v(-3.45, 1.6) * mm, "end": v(-3.35, 1.7) * mm});
            skLineSegment(sketch, "E12.3.0.25", {"start": v(-3.47, 1.46) * mm, "end": v(-3.37, 1.56) * mm});
            skLineSegment(sketch, "E12.3.0.26", {"start": v(-3.47, 1.14) * mm, "end": v(-3.37, 1.24) * mm});
            skLineSegment(sketch, "E12.3.0.27", {"start": v(-3.45, 1.45) * mm, "end": v(-3.35, 1.54) * mm});
            skLineSegment(sketch, "E12.3.0.28", {"start": v(-3.47, 1.3) * mm, "end": v(-3.37, 1.4) * mm});
            skLineSegment(sketch, "E12.3.0.29", {"start": v(-3.45, 1.12) * mm, "end": v(-3.35, 1.22) * mm});
            skLineSegment(sketch, "E12.3.0.30", {"start": v(-3.47, 1.63) * mm, "end": v(-3.37, 1.72) * mm});
            skLineSegment(sketch, "E12.3.0.31", {"start": v(-3.47, 1.79) * mm, "end": v(-3.37, 1.89) * mm});
            skLineSegment(sketch, "E12.3.0.32", {"start": v(-3.45, 1.93) * mm, "end": v(-3.35, 2.03) * mm});
            skLineSegment(sketch, "E12.3.0.33", {"start": v(-3.47, 2.1) * mm, "end": v(-3.45, 2.13) * mm});
            skLineSegment(sketch, "E12.3.0.34", {"start": v(-3.35, 1.7) * mm, "end": v(-3.45, 1.8) * mm});
            skLineSegment(sketch, "E12.3.0.35", {"start": v(-3.35, 1.22) * mm, "end": v(-3.45, 1.32) * mm});
            skLineSegment(sketch, "E12.3.0.36", {"start": v(-3.35, 1.87) * mm, "end": v(-3.45, 1.97) * mm});
            skLineSegment(sketch, "E12.3.0.37", {"start": v(-3.37, 1.89) * mm, "end": v(-3.35, 1.87) * mm});
            skLineSegment(sketch, "E12.3.0.38", {"start": v(-3.37, 1.56) * mm, "end": v(-3.35, 1.54) * mm});
            skLineSegment(sketch, "E12.3.0.39", {"start": v(-3.37, 1.24) * mm, "end": v(-3.35, 1.22) * mm});
            skLineSegment(sketch, "E12.3.0.40", {"start": v(-3.37, 1.72) * mm, "end": v(-3.35, 1.7) * mm});
            skLineSegment(sketch, "E12.3.0.41", {"start": v(-3.37, 1.4) * mm, "end": v(-3.35, 1.38) * mm});
            skLineSegment(sketch, "E12.3.0.42", {"start": v(-3.37, 2.05) * mm, "end": v(-3.35, 2.03) * mm});
            skLineSegment(sketch, "E12.3.0.43", {"start": v(-3.47, 1.79) * mm, "end": v(-3.45, 1.8) * mm});
            skLineSegment(sketch, "E12.3.0.44", {"start": v(-3.47, 1.79) * mm, "end": v(-3.45, 1.77) * mm});
            skLineSegment(sketch, "E12.3.0.45", {"start": v(-3.47, 1.14) * mm, "end": v(-3.45, 1.12) * mm});
            skLineSegment(sketch, "E12.3.0.46", {"start": v(-3.45, 1.77) * mm, "end": v(-3.43, 1.79) * mm});
            skLineSegment(sketch, "E12.3.0.47", {"start": v(-3.45, 1.12) * mm, "end": v(-3.43, 1.14) * mm});
            skLineSegment(sketch, "E12.3.0.48", {"start": v(-3.45, 1.93) * mm, "end": v(-3.43, 1.95) * mm});
            skLineSegment(sketch, "E12.3.0.49", {"start": v(-3.47, 1.3) * mm, "end": v(-3.45, 1.28) * mm});
            skLineSegment(sketch, "E12.3.0.50", {"start": v(-3.47, 1.63) * mm, "end": v(-3.45, 1.6) * mm});
            skLineSegment(sketch, "E12.3.0.51", {"start": v(-3.45, 1.6) * mm, "end": v(-3.43, 1.62) * mm});
            skLineSegment(sketch, "E12.3.0.52", {"start": v(-3.47, 1.46) * mm, "end": v(-3.45, 1.45) * mm});
            skLineSegment(sketch, "E12.3.0.53", {"start": v(-3.47, 1.63) * mm, "end": v(-3.45, 1.64) * mm});
            skLineSegment(sketch, "E12.3.0.54", {"start": v(-3.47, 1.3) * mm, "end": v(-3.45, 1.32) * mm});
            skLineSegment(sketch, "E12.3.0.55", {"start": v(-3.47, 1.95) * mm, "end": v(-3.45, 1.97) * mm});
            skLineSegment(sketch, "E12.3.0.56", {"start": v(-3.47, 1.95) * mm, "end": v(-3.45, 1.93) * mm});
            skLineSegment(sketch, "E12.3.0.57", {"start": v(-3.47, 1.46) * mm, "end": v(-3.45, 1.48) * mm});
            skLineSegment(sketch, "E12.3.0.58", {"start": v(-3.45, 1.45) * mm, "end": v(-3.43, 1.46) * mm});
            skLineSegment(sketch, "E12.3.0.59", {"start": v(-3.45, 1.28) * mm, "end": v(-3.43, 1.3) * mm});
            skLineSegment(sketch, "E12.3.1.0", {"start": v(-3.37, 3.56) * mm, "end": v(-3.47, 3.66) * mm});
            skLineSegment(sketch, "E12.3.1.1", {"start": v(-3.37, 3.24) * mm, "end": v(-3.47, 3.33) * mm});
            skPoint(sketch, "E12.3.1.2", {"position": v(-3.41, 4.02) * mm});
            skLineSegment(sketch, "E12.3.1.3", {"start": v(-3.35, 4.06) * mm, "end": v(-3.45, 4.16) * mm});
            skPoint(sketch, "E12.3.1.4", {"position": v(-3.5, 3.37) * mm});
            skLineSegment(sketch, "E12.3.1.5", {"start": v(-3.37, 4.04) * mm, "end": v(-3.47, 4.14) * mm});
            skPoint(sketch, "E12.3.1.6", {"position": v(-3.5, 3.54) * mm});
            skPoint(sketch, "E12.3.1.7", {"position": v(-3.5, 3.86) * mm});
            skPoint(sketch, "E12.3.1.8", {"position": v(-3.41, 3.37) * mm});
            skPoint(sketch, "E12.3.1.9", {"position": v(-3.41, 3.7) * mm});
            skLineSegment(sketch, "E12.3.1.10", {"start": v(-3.37, 3.4) * mm, "end": v(-3.47, 3.5) * mm});
            skPoint(sketch, "E12.3.1.11", {"position": v(-3.41, 3.54) * mm});
            skPoint(sketch, "E12.3.1.12", {"position": v(-3.41, 3.21) * mm});
            skLineSegment(sketch, "E12.3.1.13", {"start": v(-3.37, 3.72) * mm, "end": v(-3.47, 3.82) * mm});
            skPoint(sketch, "E12.3.1.14", {"position": v(-3.5, 4.02) * mm});
            skPoint(sketch, "E12.3.1.15", {"position": v(-3.5, 3.7) * mm});
            skLineSegment(sketch, "E12.3.1.16", {"start": v(-3.37, 3.88) * mm, "end": v(-3.47, 3.98) * mm});
            skPoint(sketch, "E12.3.1.17", {"position": v(-3.5, 3.21) * mm});
            skPoint(sketch, "E12.3.1.18", {"position": v(-3.41, 3.86) * mm});
            skLineSegment(sketch, "E12.3.1.19", {"start": v(-3.35, 3.41) * mm, "end": v(-3.45, 3.51) * mm});
            skLineSegment(sketch, "E12.3.1.20", {"start": v(-3.47, 3.98) * mm, "end": v(-3.37, 4.08) * mm});
            skLineSegment(sketch, "E12.3.1.21", {"start": v(-3.45, 3.8) * mm, "end": v(-3.35, 3.9) * mm});
            skLineSegment(sketch, "E12.3.1.22", {"start": v(-3.35, 3.58) * mm, "end": v(-3.45, 3.68) * mm});
            skLineSegment(sketch, "E12.3.1.23", {"start": v(-3.45, 3.32) * mm, "end": v(-3.35, 3.41) * mm});
            skLineSegment(sketch, "E12.3.1.24", {"start": v(-3.45, 3.64) * mm, "end": v(-3.35, 3.74) * mm});
            skLineSegment(sketch, "E12.3.1.25", {"start": v(-3.47, 3.5) * mm, "end": v(-3.37, 3.6) * mm});
            skLineSegment(sketch, "E12.3.1.26", {"start": v(-3.47, 3.17) * mm, "end": v(-3.37, 3.27) * mm});
            skLineSegment(sketch, "E12.3.1.27", {"start": v(-3.45, 3.48) * mm, "end": v(-3.35, 3.58) * mm});
            skLineSegment(sketch, "E12.3.1.28", {"start": v(-3.47, 3.33) * mm, "end": v(-3.37, 3.43) * mm});
            skLineSegment(sketch, "E12.3.1.29", {"start": v(-3.45, 3.15) * mm, "end": v(-3.35, 3.25) * mm});
            skLineSegment(sketch, "E12.3.1.30", {"start": v(-3.47, 3.66) * mm, "end": v(-3.37, 3.76) * mm});
            skLineSegment(sketch, "E12.3.1.31", {"start": v(-3.47, 3.82) * mm, "end": v(-3.37, 3.92) * mm});
            skLineSegment(sketch, "E12.3.1.32", {"start": v(-3.45, 3.96) * mm, "end": v(-3.35, 4.06) * mm});
            skLineSegment(sketch, "E12.3.1.33", {"start": v(-3.47, 4.14) * mm, "end": v(-3.45, 4.16) * mm});
            skLineSegment(sketch, "E12.3.1.34", {"start": v(-3.35, 3.74) * mm, "end": v(-3.45, 3.84) * mm});
            skLineSegment(sketch, "E12.3.1.35", {"start": v(-3.35, 3.25) * mm, "end": v(-3.45, 3.35) * mm});
            skLineSegment(sketch, "E12.3.1.36", {"start": v(-3.35, 3.9) * mm, "end": v(-3.45, 4) * mm});
            skLineSegment(sketch, "E12.3.1.37", {"start": v(-3.37, 3.92) * mm, "end": v(-3.35, 3.9) * mm});
            skLineSegment(sketch, "E12.3.1.38", {"start": v(-3.37, 3.6) * mm, "end": v(-3.35, 3.58) * mm});
            skLineSegment(sketch, "E12.3.1.39", {"start": v(-3.37, 3.27) * mm, "end": v(-3.35, 3.25) * mm});
            skLineSegment(sketch, "E12.3.1.40", {"start": v(-3.37, 3.76) * mm, "end": v(-3.35, 3.74) * mm});
            skLineSegment(sketch, "E12.3.1.41", {"start": v(-3.37, 3.43) * mm, "end": v(-3.35, 3.41) * mm});
            skLineSegment(sketch, "E12.3.1.42", {"start": v(-3.37, 4.08) * mm, "end": v(-3.35, 4.06) * mm});
            skLineSegment(sketch, "E12.3.1.43", {"start": v(-3.47, 3.82) * mm, "end": v(-3.45, 3.84) * mm});
            skLineSegment(sketch, "E12.3.1.44", {"start": v(-3.47, 3.82) * mm, "end": v(-3.45, 3.8) * mm});
            skLineSegment(sketch, "E12.3.1.45", {"start": v(-3.47, 3.17) * mm, "end": v(-3.45, 3.15) * mm});
            skLineSegment(sketch, "E12.3.1.46", {"start": v(-3.45, 3.8) * mm, "end": v(-3.43, 3.82) * mm});
            skLineSegment(sketch, "E12.3.1.47", {"start": v(-3.45, 3.15) * mm, "end": v(-3.43, 3.17) * mm});
            skLineSegment(sketch, "E12.3.1.48", {"start": v(-3.45, 3.96) * mm, "end": v(-3.43, 3.98) * mm});
            skLineSegment(sketch, "E12.3.1.49", {"start": v(-3.47, 3.33) * mm, "end": v(-3.45, 3.32) * mm});
            skLineSegment(sketch, "E12.3.1.50", {"start": v(-3.47, 3.66) * mm, "end": v(-3.45, 3.64) * mm});
            skLineSegment(sketch, "E12.3.1.51", {"start": v(-3.45, 3.64) * mm, "end": v(-3.43, 3.66) * mm});
            skLineSegment(sketch, "E12.3.1.52", {"start": v(-3.47, 3.5) * mm, "end": v(-3.45, 3.48) * mm});
            skLineSegment(sketch, "E12.3.1.53", {"start": v(-3.47, 3.66) * mm, "end": v(-3.45, 3.68) * mm});
            skLineSegment(sketch, "E12.3.1.54", {"start": v(-3.47, 3.33) * mm, "end": v(-3.45, 3.35) * mm});
            skLineSegment(sketch, "E12.3.1.55", {"start": v(-3.47, 3.98) * mm, "end": v(-3.45, 4) * mm});
            skLineSegment(sketch, "E12.3.1.56", {"start": v(-3.47, 3.98) * mm, "end": v(-3.45, 3.96) * mm});
            skLineSegment(sketch, "E12.3.1.57", {"start": v(-3.47, 3.5) * mm, "end": v(-3.45, 3.51) * mm});
            skLineSegment(sketch, "E12.3.1.58", {"start": v(-3.45, 3.48) * mm, "end": v(-3.43, 3.5) * mm});
            skLineSegment(sketch, "E12.3.1.59", {"start": v(-3.45, 3.32) * mm, "end": v(-3.43, 3.33) * mm});
            skLineSegment(sketch, "E12.4.0.0", {"start": v(-3.22, 1.53) * mm, "end": v(-3.32, 1.63) * mm});
            skLineSegment(sketch, "E12.4.0.1", {"start": v(-3.22, 1.2) * mm, "end": v(-3.32, 1.3) * mm});
            skPoint(sketch, "E12.4.0.2", {"position": v(-3.26, 1.99) * mm});
            skLineSegment(sketch, "E12.4.0.3", {"start": v(-3.2, 2.03) * mm, "end": v(-3.3, 2.13) * mm});
            skPoint(sketch, "E12.4.0.4", {"position": v(-3.34, 1.34) * mm});
            skLineSegment(sketch, "E12.4.0.5", {"start": v(-3.22, 2.01) * mm, "end": v(-3.32, 2.1) * mm});
            skPoint(sketch, "E12.4.0.6", {"position": v(-3.34, 1.5) * mm});
            skPoint(sketch, "E12.4.0.7", {"position": v(-3.34, 1.83) * mm});
            skPoint(sketch, "E12.4.0.8", {"position": v(-3.26, 1.34) * mm});
            skPoint(sketch, "E12.4.0.9", {"position": v(-3.26, 1.67) * mm});
            skLineSegment(sketch, "E12.4.0.10", {"start": v(-3.22, 1.36) * mm, "end": v(-3.32, 1.46) * mm});
            skPoint(sketch, "E12.4.0.11", {"position": v(-3.26, 1.5) * mm});
            skPoint(sketch, "E12.4.0.12", {"position": v(-3.26, 1.18) * mm});
            skLineSegment(sketch, "E12.4.0.13", {"start": v(-3.22, 1.69) * mm, "end": v(-3.32, 1.79) * mm});
            skPoint(sketch, "E12.4.0.14", {"position": v(-3.34, 1.99) * mm});
            skPoint(sketch, "E12.4.0.15", {"position": v(-3.34, 1.67) * mm});
            skLineSegment(sketch, "E12.4.0.16", {"start": v(-3.22, 1.85) * mm, "end": v(-3.32, 1.95) * mm});
            skPoint(sketch, "E12.4.0.17", {"position": v(-3.34, 1.18) * mm});
            skPoint(sketch, "E12.4.0.18", {"position": v(-3.26, 1.83) * mm});
            skLineSegment(sketch, "E12.4.0.19", {"start": v(-3.2, 1.38) * mm, "end": v(-3.3, 1.48) * mm});
            skLineSegment(sketch, "E12.4.0.20", {"start": v(-3.32, 1.95) * mm, "end": v(-3.22, 2.05) * mm});
            skLineSegment(sketch, "E12.4.0.21", {"start": v(-3.3, 1.77) * mm, "end": v(-3.2, 1.87) * mm});
            skLineSegment(sketch, "E12.4.0.22", {"start": v(-3.2, 1.54) * mm, "end": v(-3.3, 1.64) * mm});
            skLineSegment(sketch, "E12.4.0.23", {"start": v(-3.3, 1.28) * mm, "end": v(-3.2, 1.38) * mm});
            skLineSegment(sketch, "E12.4.0.24", {"start": v(-3.3, 1.6) * mm, "end": v(-3.2, 1.7) * mm});
            skLineSegment(sketch, "E12.4.0.25", {"start": v(-3.32, 1.46) * mm, "end": v(-3.22, 1.56) * mm});
            skLineSegment(sketch, "E12.4.0.26", {"start": v(-3.32, 1.14) * mm, "end": v(-3.22, 1.24) * mm});
            skLineSegment(sketch, "E12.4.0.27", {"start": v(-3.3, 1.45) * mm, "end": v(-3.2, 1.54) * mm});
            skLineSegment(sketch, "E12.4.0.28", {"start": v(-3.32, 1.3) * mm, "end": v(-3.22, 1.4) * mm});
            skLineSegment(sketch, "E12.4.0.29", {"start": v(-3.3, 1.12) * mm, "end": v(-3.2, 1.22) * mm});
            skLineSegment(sketch, "E12.4.0.30", {"start": v(-3.32, 1.63) * mm, "end": v(-3.22, 1.72) * mm});
            skLineSegment(sketch, "E12.4.0.31", {"start": v(-3.32, 1.79) * mm, "end": v(-3.22, 1.89) * mm});
            skLineSegment(sketch, "E12.4.0.32", {"start": v(-3.3, 1.93) * mm, "end": v(-3.2, 2.03) * mm});
            skLineSegment(sketch, "E12.4.0.33", {"start": v(-3.32, 2.1) * mm, "end": v(-3.3, 2.13) * mm});
            skLineSegment(sketch, "E12.4.0.34", {"start": v(-3.2, 1.7) * mm, "end": v(-3.3, 1.8) * mm});
            skLineSegment(sketch, "E12.4.0.35", {"start": v(-3.2, 1.22) * mm, "end": v(-3.3, 1.32) * mm});
            skLineSegment(sketch, "E12.4.0.36", {"start": v(-3.2, 1.87) * mm, "end": v(-3.3, 1.97) * mm});
            skLineSegment(sketch, "E12.4.0.37", {"start": v(-3.22, 1.89) * mm, "end": v(-3.2, 1.87) * mm});
            skLineSegment(sketch, "E12.4.0.38", {"start": v(-3.22, 1.56) * mm, "end": v(-3.2, 1.54) * mm});
            skLineSegment(sketch, "E12.4.0.39", {"start": v(-3.22, 1.24) * mm, "end": v(-3.2, 1.22) * mm});
            skLineSegment(sketch, "E12.4.0.40", {"start": v(-3.22, 1.72) * mm, "end": v(-3.2, 1.7) * mm});
            skLineSegment(sketch, "E12.4.0.41", {"start": v(-3.22, 1.4) * mm, "end": v(-3.2, 1.38) * mm});
            skLineSegment(sketch, "E12.4.0.42", {"start": v(-3.22, 2.05) * mm, "end": v(-3.2, 2.03) * mm});
            skLineSegment(sketch, "E12.4.0.43", {"start": v(-3.32, 1.79) * mm, "end": v(-3.3, 1.8) * mm});
            skLineSegment(sketch, "E12.4.0.44", {"start": v(-3.32, 1.79) * mm, "end": v(-3.3, 1.77) * mm});
            skLineSegment(sketch, "E12.4.0.45", {"start": v(-3.32, 1.14) * mm, "end": v(-3.3, 1.12) * mm});
            skLineSegment(sketch, "E12.4.0.46", {"start": v(-3.3, 1.77) * mm, "end": v(-3.28, 1.79) * mm});
            skLineSegment(sketch, "E12.4.0.47", {"start": v(-3.3, 1.12) * mm, "end": v(-3.28, 1.14) * mm});
            skLineSegment(sketch, "E12.4.0.48", {"start": v(-3.3, 1.93) * mm, "end": v(-3.28, 1.95) * mm});
            skLineSegment(sketch, "E12.4.0.49", {"start": v(-3.32, 1.3) * mm, "end": v(-3.3, 1.28) * mm});
            skLineSegment(sketch, "E12.4.0.50", {"start": v(-3.32, 1.63) * mm, "end": v(-3.3, 1.6) * mm});
            skLineSegment(sketch, "E12.4.0.51", {"start": v(-3.3, 1.6) * mm, "end": v(-3.28, 1.62) * mm});
            skLineSegment(sketch, "E12.4.0.52", {"start": v(-3.32, 1.46) * mm, "end": v(-3.3, 1.45) * mm});
            skLineSegment(sketch, "E12.4.0.53", {"start": v(-3.32, 1.63) * mm, "end": v(-3.3, 1.64) * mm});
            skLineSegment(sketch, "E12.4.0.54", {"start": v(-3.32, 1.3) * mm, "end": v(-3.3, 1.32) * mm});
            skLineSegment(sketch, "E12.4.0.55", {"start": v(-3.32, 1.95) * mm, "end": v(-3.3, 1.97) * mm});
            skLineSegment(sketch, "E12.4.0.56", {"start": v(-3.32, 1.95) * mm, "end": v(-3.3, 1.93) * mm});
            skLineSegment(sketch, "E12.4.0.57", {"start": v(-3.32, 1.46) * mm, "end": v(-3.3, 1.48) * mm});
            skLineSegment(sketch, "E12.4.0.58", {"start": v(-3.3, 1.45) * mm, "end": v(-3.28, 1.46) * mm});
            skLineSegment(sketch, "E12.4.0.59", {"start": v(-3.3, 1.28) * mm, "end": v(-3.28, 1.3) * mm});
            skLineSegment(sketch, "E12.4.1.0", {"start": v(-3.22, 3.56) * mm, "end": v(-3.32, 3.66) * mm});
            skLineSegment(sketch, "E12.4.1.1", {"start": v(-3.22, 3.24) * mm, "end": v(-3.32, 3.33) * mm});
            skPoint(sketch, "E12.4.1.2", {"position": v(-3.26, 4.02) * mm});
            skLineSegment(sketch, "E12.4.1.3", {"start": v(-3.2, 4.06) * mm, "end": v(-3.3, 4.16) * mm});
            skPoint(sketch, "E12.4.1.4", {"position": v(-3.34, 3.37) * mm});
            skLineSegment(sketch, "E12.4.1.5", {"start": v(-3.22, 4.04) * mm, "end": v(-3.32, 4.14) * mm});
            skPoint(sketch, "E12.4.1.6", {"position": v(-3.34, 3.54) * mm});
            skPoint(sketch, "E12.4.1.7", {"position": v(-3.34, 3.86) * mm});
            skPoint(sketch, "E12.4.1.8", {"position": v(-3.26, 3.37) * mm});
            skPoint(sketch, "E12.4.1.9", {"position": v(-3.26, 3.7) * mm});
            skLineSegment(sketch, "E12.4.1.10", {"start": v(-3.22, 3.4) * mm, "end": v(-3.32, 3.5) * mm});
            skPoint(sketch, "E12.4.1.11", {"position": v(-3.26, 3.54) * mm});
            skPoint(sketch, "E12.4.1.12", {"position": v(-3.26, 3.21) * mm});
            skLineSegment(sketch, "E12.4.1.13", {"start": v(-3.22, 3.72) * mm, "end": v(-3.32, 3.82) * mm});
            skPoint(sketch, "E12.4.1.14", {"position": v(-3.34, 4.02) * mm});
            skPoint(sketch, "E12.4.1.15", {"position": v(-3.34, 3.7) * mm});
            skLineSegment(sketch, "E12.4.1.16", {"start": v(-3.22, 3.88) * mm, "end": v(-3.32, 3.98) * mm});
            skPoint(sketch, "E12.4.1.17", {"position": v(-3.34, 3.21) * mm});
            skPoint(sketch, "E12.4.1.18", {"position": v(-3.26, 3.86) * mm});
            skLineSegment(sketch, "E12.4.1.19", {"start": v(-3.2, 3.41) * mm, "end": v(-3.3, 3.51) * mm});
            skLineSegment(sketch, "E12.4.1.20", {"start": v(-3.32, 3.98) * mm, "end": v(-3.22, 4.08) * mm});
            skLineSegment(sketch, "E12.4.1.21", {"start": v(-3.3, 3.8) * mm, "end": v(-3.2, 3.9) * mm});
            skLineSegment(sketch, "E12.4.1.22", {"start": v(-3.2, 3.58) * mm, "end": v(-3.3, 3.68) * mm});
            skLineSegment(sketch, "E12.4.1.23", {"start": v(-3.3, 3.32) * mm, "end": v(-3.2, 3.41) * mm});
            skLineSegment(sketch, "E12.4.1.24", {"start": v(-3.3, 3.64) * mm, "end": v(-3.2, 3.74) * mm});
            skLineSegment(sketch, "E12.4.1.25", {"start": v(-3.32, 3.5) * mm, "end": v(-3.22, 3.6) * mm});
            skLineSegment(sketch, "E12.4.1.26", {"start": v(-3.32, 3.17) * mm, "end": v(-3.22, 3.27) * mm});
            skLineSegment(sketch, "E12.4.1.27", {"start": v(-3.3, 3.48) * mm, "end": v(-3.2, 3.58) * mm});
            skLineSegment(sketch, "E12.4.1.28", {"start": v(-3.32, 3.33) * mm, "end": v(-3.22, 3.43) * mm});
            skLineSegment(sketch, "E12.4.1.29", {"start": v(-3.3, 3.15) * mm, "end": v(-3.2, 3.25) * mm});
            skLineSegment(sketch, "E12.4.1.30", {"start": v(-3.32, 3.66) * mm, "end": v(-3.22, 3.76) * mm});
            skLineSegment(sketch, "E12.4.1.31", {"start": v(-3.32, 3.82) * mm, "end": v(-3.22, 3.92) * mm});
            skLineSegment(sketch, "E12.4.1.32", {"start": v(-3.3, 3.96) * mm, "end": v(-3.2, 4.06) * mm});
            skLineSegment(sketch, "E12.4.1.33", {"start": v(-3.32, 4.14) * mm, "end": v(-3.3, 4.16) * mm});
            skLineSegment(sketch, "E12.4.1.34", {"start": v(-3.2, 3.74) * mm, "end": v(-3.3, 3.84) * mm});
            skLineSegment(sketch, "E12.4.1.35", {"start": v(-3.2, 3.25) * mm, "end": v(-3.3, 3.35) * mm});
            skLineSegment(sketch, "E12.4.1.36", {"start": v(-3.2, 3.9) * mm, "end": v(-3.3, 4) * mm});
            skLineSegment(sketch, "E12.4.1.37", {"start": v(-3.22, 3.92) * mm, "end": v(-3.2, 3.9) * mm});
            skLineSegment(sketch, "E12.4.1.38", {"start": v(-3.22, 3.6) * mm, "end": v(-3.2, 3.58) * mm});
            skLineSegment(sketch, "E12.4.1.39", {"start": v(-3.22, 3.27) * mm, "end": v(-3.2, 3.25) * mm});
            skLineSegment(sketch, "E12.4.1.40", {"start": v(-3.22, 3.76) * mm, "end": v(-3.2, 3.74) * mm});
            skLineSegment(sketch, "E12.4.1.41", {"start": v(-3.22, 3.43) * mm, "end": v(-3.2, 3.41) * mm});
            skLineSegment(sketch, "E12.4.1.42", {"start": v(-3.22, 4.08) * mm, "end": v(-3.2, 4.06) * mm});
            skLineSegment(sketch, "E12.4.1.43", {"start": v(-3.32, 3.82) * mm, "end": v(-3.3, 3.84) * mm});
            skLineSegment(sketch, "E12.4.1.44", {"start": v(-3.32, 3.82) * mm, "end": v(-3.3, 3.8) * mm});
            skLineSegment(sketch, "E12.4.1.45", {"start": v(-3.32, 3.17) * mm, "end": v(-3.3, 3.15) * mm});
            skLineSegment(sketch, "E12.4.1.46", {"start": v(-3.3, 3.8) * mm, "end": v(-3.28, 3.82) * mm});
            skLineSegment(sketch, "E12.4.1.47", {"start": v(-3.3, 3.15) * mm, "end": v(-3.28, 3.17) * mm});
            skLineSegment(sketch, "E12.4.1.48", {"start": v(-3.3, 3.96) * mm, "end": v(-3.28, 3.98) * mm});
            skLineSegment(sketch, "E12.4.1.49", {"start": v(-3.32, 3.33) * mm, "end": v(-3.3, 3.32) * mm});
            skLineSegment(sketch, "E12.4.1.50", {"start": v(-3.32, 3.66) * mm, "end": v(-3.3, 3.64) * mm});
            skLineSegment(sketch, "E12.4.1.51", {"start": v(-3.3, 3.64) * mm, "end": v(-3.28, 3.66) * mm});
            skLineSegment(sketch, "E12.4.1.52", {"start": v(-3.32, 3.5) * mm, "end": v(-3.3, 3.48) * mm});
            skLineSegment(sketch, "E12.4.1.53", {"start": v(-3.32, 3.66) * mm, "end": v(-3.3, 3.68) * mm});
            skLineSegment(sketch, "E12.4.1.54", {"start": v(-3.32, 3.33) * mm, "end": v(-3.3, 3.35) * mm});
            skLineSegment(sketch, "E12.4.1.55", {"start": v(-3.32, 3.98) * mm, "end": v(-3.3, 4) * mm});
            skLineSegment(sketch, "E12.4.1.56", {"start": v(-3.32, 3.98) * mm, "end": v(-3.3, 3.96) * mm});
            skLineSegment(sketch, "E12.4.1.57", {"start": v(-3.32, 3.5) * mm, "end": v(-3.3, 3.51) * mm});
            skLineSegment(sketch, "E12.4.1.58", {"start": v(-3.3, 3.48) * mm, "end": v(-3.28, 3.5) * mm});
            skLineSegment(sketch, "E12.4.1.59", {"start": v(-3.3, 3.32) * mm, "end": v(-3.28, 3.33) * mm});
            skLineSegment(sketch, "E12.5.0.0", {"start": v(-3.07, 1.53) * mm, "end": v(-3.17, 1.63) * mm});
            skLineSegment(sketch, "E12.5.0.1", {"start": v(-3.07, 1.2) * mm, "end": v(-3.17, 1.3) * mm});
            skPoint(sketch, "E12.5.0.2", {"position": v(-3.1, 1.99) * mm});
            skLineSegment(sketch, "E12.5.0.3", {"start": v(-3.05, 2.03) * mm, "end": v(-3.15, 2.13) * mm});
            skPoint(sketch, "E12.5.0.4", {"position": v(-3.19, 1.34) * mm});
            skLineSegment(sketch, "E12.5.0.5", {"start": v(-3.07, 2.01) * mm, "end": v(-3.17, 2.1) * mm});
            skPoint(sketch, "E12.5.0.6", {"position": v(-3.19, 1.5) * mm});
            skPoint(sketch, "E12.5.0.7", {"position": v(-3.19, 1.83) * mm});
            skPoint(sketch, "E12.5.0.8", {"position": v(-3.1, 1.34) * mm});
            skPoint(sketch, "E12.5.0.9", {"position": v(-3.1, 1.67) * mm});
            skLineSegment(sketch, "E12.5.0.10", {"start": v(-3.07, 1.36) * mm, "end": v(-3.17, 1.46) * mm});
            skPoint(sketch, "E12.5.0.11", {"position": v(-3.1, 1.5) * mm});
            skPoint(sketch, "E12.5.0.12", {"position": v(-3.1, 1.18) * mm});
            skLineSegment(sketch, "E12.5.0.13", {"start": v(-3.07, 1.69) * mm, "end": v(-3.17, 1.79) * mm});
            skPoint(sketch, "E12.5.0.14", {"position": v(-3.19, 1.99) * mm});
            skPoint(sketch, "E12.5.0.15", {"position": v(-3.19, 1.67) * mm});
            skLineSegment(sketch, "E12.5.0.16", {"start": v(-3.07, 1.85) * mm, "end": v(-3.17, 1.95) * mm});
            skPoint(sketch, "E12.5.0.17", {"position": v(-3.19, 1.18) * mm});
            skPoint(sketch, "E12.5.0.18", {"position": v(-3.1, 1.83) * mm});
            skLineSegment(sketch, "E12.5.0.19", {"start": v(-3.05, 1.38) * mm, "end": v(-3.15, 1.48) * mm});
            skLineSegment(sketch, "E12.5.0.20", {"start": v(-3.17, 1.95) * mm, "end": v(-3.07, 2.05) * mm});
            skLineSegment(sketch, "E12.5.0.21", {"start": v(-3.15, 1.77) * mm, "end": v(-3.05, 1.87) * mm});
            skLineSegment(sketch, "E12.5.0.22", {"start": v(-3.05, 1.54) * mm, "end": v(-3.15, 1.64) * mm});
            skLineSegment(sketch, "E12.5.0.23", {"start": v(-3.15, 1.28) * mm, "end": v(-3.05, 1.38) * mm});
            skLineSegment(sketch, "E12.5.0.24", {"start": v(-3.15, 1.6) * mm, "end": v(-3.05, 1.7) * mm});
            skLineSegment(sketch, "E12.5.0.25", {"start": v(-3.17, 1.46) * mm, "end": v(-3.07, 1.56) * mm});
            skLineSegment(sketch, "E12.5.0.26", {"start": v(-3.17, 1.14) * mm, "end": v(-3.07, 1.24) * mm});
            skLineSegment(sketch, "E12.5.0.27", {"start": v(-3.15, 1.45) * mm, "end": v(-3.05, 1.54) * mm});
            skLineSegment(sketch, "E12.5.0.28", {"start": v(-3.17, 1.3) * mm, "end": v(-3.07, 1.4) * mm});
            skLineSegment(sketch, "E12.5.0.29", {"start": v(-3.15, 1.12) * mm, "end": v(-3.05, 1.22) * mm});
            skLineSegment(sketch, "E12.5.0.30", {"start": v(-3.17, 1.63) * mm, "end": v(-3.07, 1.72) * mm});
            skLineSegment(sketch, "E12.5.0.31", {"start": v(-3.17, 1.79) * mm, "end": v(-3.07, 1.89) * mm});
            skLineSegment(sketch, "E12.5.0.32", {"start": v(-3.15, 1.93) * mm, "end": v(-3.05, 2.03) * mm});
            skLineSegment(sketch, "E12.5.0.33", {"start": v(-3.17, 2.1) * mm, "end": v(-3.15, 2.13) * mm});
            skLineSegment(sketch, "E12.5.0.34", {"start": v(-3.05, 1.7) * mm, "end": v(-3.15, 1.8) * mm});
            skLineSegment(sketch, "E12.5.0.35", {"start": v(-3.05, 1.22) * mm, "end": v(-3.15, 1.32) * mm});
            skLineSegment(sketch, "E12.5.0.36", {"start": v(-3.05, 1.87) * mm, "end": v(-3.15, 1.97) * mm});
            skLineSegment(sketch, "E12.5.0.37", {"start": v(-3.07, 1.89) * mm, "end": v(-3.05, 1.87) * mm});
            skLineSegment(sketch, "E12.5.0.38", {"start": v(-3.07, 1.56) * mm, "end": v(-3.05, 1.54) * mm});
            skLineSegment(sketch, "E12.5.0.39", {"start": v(-3.07, 1.24) * mm, "end": v(-3.05, 1.22) * mm});
            skLineSegment(sketch, "E12.5.0.40", {"start": v(-3.07, 1.72) * mm, "end": v(-3.05, 1.7) * mm});
            skLineSegment(sketch, "E12.5.0.41", {"start": v(-3.07, 1.4) * mm, "end": v(-3.05, 1.38) * mm});
            skLineSegment(sketch, "E12.5.0.42", {"start": v(-3.07, 2.05) * mm, "end": v(-3.05, 2.03) * mm});
            skLineSegment(sketch, "E12.5.0.43", {"start": v(-3.17, 1.79) * mm, "end": v(-3.15, 1.8) * mm});
            skLineSegment(sketch, "E12.5.0.44", {"start": v(-3.17, 1.79) * mm, "end": v(-3.15, 1.77) * mm});
            skLineSegment(sketch, "E12.5.0.45", {"start": v(-3.17, 1.14) * mm, "end": v(-3.15, 1.12) * mm});
            skLineSegment(sketch, "E12.5.0.46", {"start": v(-3.15, 1.77) * mm, "end": v(-3.13, 1.79) * mm});
            skLineSegment(sketch, "E12.5.0.47", {"start": v(-3.15, 1.12) * mm, "end": v(-3.13, 1.14) * mm});
            skLineSegment(sketch, "E12.5.0.48", {"start": v(-3.15, 1.93) * mm, "end": v(-3.13, 1.95) * mm});
            skLineSegment(sketch, "E12.5.0.49", {"start": v(-3.17, 1.3) * mm, "end": v(-3.15, 1.28) * mm});
            skLineSegment(sketch, "E12.5.0.50", {"start": v(-3.17, 1.63) * mm, "end": v(-3.15, 1.6) * mm});
            skLineSegment(sketch, "E12.5.0.51", {"start": v(-3.15, 1.6) * mm, "end": v(-3.13, 1.62) * mm});
            skLineSegment(sketch, "E12.5.0.52", {"start": v(-3.17, 1.46) * mm, "end": v(-3.15, 1.45) * mm});
            skLineSegment(sketch, "E12.5.0.53", {"start": v(-3.17, 1.63) * mm, "end": v(-3.15, 1.64) * mm});
            skLineSegment(sketch, "E12.5.0.54", {"start": v(-3.17, 1.3) * mm, "end": v(-3.15, 1.32) * mm});
            skLineSegment(sketch, "E12.5.0.55", {"start": v(-3.17, 1.95) * mm, "end": v(-3.15, 1.97) * mm});
            skLineSegment(sketch, "E12.5.0.56", {"start": v(-3.17, 1.95) * mm, "end": v(-3.15, 1.93) * mm});
            skLineSegment(sketch, "E12.5.0.57", {"start": v(-3.17, 1.46) * mm, "end": v(-3.15, 1.48) * mm});
            skLineSegment(sketch, "E12.5.0.58", {"start": v(-3.15, 1.45) * mm, "end": v(-3.13, 1.46) * mm});
            skLineSegment(sketch, "E12.5.0.59", {"start": v(-3.15, 1.28) * mm, "end": v(-3.13, 1.3) * mm});
            skLineSegment(sketch, "E12.5.1.0", {"start": v(-3.07, 3.56) * mm, "end": v(-3.17, 3.66) * mm});
            skLineSegment(sketch, "E12.5.1.1", {"start": v(-3.07, 3.24) * mm, "end": v(-3.17, 3.33) * mm});
            skPoint(sketch, "E12.5.1.2", {"position": v(-3.1, 4.02) * mm});
            skLineSegment(sketch, "E12.5.1.3", {"start": v(-3.05, 4.06) * mm, "end": v(-3.15, 4.16) * mm});
            skPoint(sketch, "E12.5.1.4", {"position": v(-3.19, 3.37) * mm});
            skLineSegment(sketch, "E12.5.1.5", {"start": v(-3.07, 4.04) * mm, "end": v(-3.17, 4.14) * mm});
            skPoint(sketch, "E12.5.1.6", {"position": v(-3.19, 3.54) * mm});
            skPoint(sketch, "E12.5.1.7", {"position": v(-3.19, 3.86) * mm});
            skPoint(sketch, "E12.5.1.8", {"position": v(-3.1, 3.37) * mm});
            skPoint(sketch, "E12.5.1.9", {"position": v(-3.1, 3.7) * mm});
            skLineSegment(sketch, "E12.5.1.10", {"start": v(-3.07, 3.4) * mm, "end": v(-3.17, 3.5) * mm});
            skPoint(sketch, "E12.5.1.11", {"position": v(-3.1, 3.54) * mm});
            skPoint(sketch, "E12.5.1.12", {"position": v(-3.1, 3.21) * mm});
            skLineSegment(sketch, "E12.5.1.13", {"start": v(-3.07, 3.72) * mm, "end": v(-3.17, 3.82) * mm});
            skPoint(sketch, "E12.5.1.14", {"position": v(-3.19, 4.02) * mm});
            skPoint(sketch, "E12.5.1.15", {"position": v(-3.19, 3.7) * mm});
            skLineSegment(sketch, "E12.5.1.16", {"start": v(-3.07, 3.88) * mm, "end": v(-3.17, 3.98) * mm});
            skPoint(sketch, "E12.5.1.17", {"position": v(-3.19, 3.21) * mm});
            skPoint(sketch, "E12.5.1.18", {"position": v(-3.1, 3.86) * mm});
            skLineSegment(sketch, "E12.5.1.19", {"start": v(-3.05, 3.41) * mm, "end": v(-3.15, 3.51) * mm});
            skLineSegment(sketch, "E12.5.1.20", {"start": v(-3.17, 3.98) * mm, "end": v(-3.07, 4.08) * mm});
            skLineSegment(sketch, "E12.5.1.21", {"start": v(-3.15, 3.8) * mm, "end": v(-3.05, 3.9) * mm});
            skLineSegment(sketch, "E12.5.1.22", {"start": v(-3.05, 3.58) * mm, "end": v(-3.15, 3.68) * mm});
            skLineSegment(sketch, "E12.5.1.23", {"start": v(-3.15, 3.32) * mm, "end": v(-3.05, 3.41) * mm});
            skLineSegment(sketch, "E12.5.1.24", {"start": v(-3.15, 3.64) * mm, "end": v(-3.05, 3.74) * mm});
            skLineSegment(sketch, "E12.5.1.25", {"start": v(-3.17, 3.5) * mm, "end": v(-3.07, 3.6) * mm});
            skLineSegment(sketch, "E12.5.1.26", {"start": v(-3.17, 3.17) * mm, "end": v(-3.07, 3.27) * mm});
            skLineSegment(sketch, "E12.5.1.27", {"start": v(-3.15, 3.48) * mm, "end": v(-3.05, 3.58) * mm});
            skLineSegment(sketch, "E12.5.1.28", {"start": v(-3.17, 3.33) * mm, "end": v(-3.07, 3.43) * mm});
            skLineSegment(sketch, "E12.5.1.29", {"start": v(-3.15, 3.15) * mm, "end": v(-3.05, 3.25) * mm});
            skLineSegment(sketch, "E12.5.1.30", {"start": v(-3.17, 3.66) * mm, "end": v(-3.07, 3.76) * mm});
            skLineSegment(sketch, "E12.5.1.31", {"start": v(-3.17, 3.82) * mm, "end": v(-3.07, 3.92) * mm});
            skLineSegment(sketch, "E12.5.1.32", {"start": v(-3.15, 3.96) * mm, "end": v(-3.05, 4.06) * mm});
            skLineSegment(sketch, "E12.5.1.33", {"start": v(-3.17, 4.14) * mm, "end": v(-3.15, 4.16) * mm});
            skLineSegment(sketch, "E12.5.1.34", {"start": v(-3.05, 3.74) * mm, "end": v(-3.15, 3.84) * mm});
            skLineSegment(sketch, "E12.5.1.35", {"start": v(-3.05, 3.25) * mm, "end": v(-3.15, 3.35) * mm});
            skLineSegment(sketch, "E12.5.1.36", {"start": v(-3.05, 3.9) * mm, "end": v(-3.15, 4) * mm});
            skLineSegment(sketch, "E12.5.1.37", {"start": v(-3.07, 3.92) * mm, "end": v(-3.05, 3.9) * mm});
            skLineSegment(sketch, "E12.5.1.38", {"start": v(-3.07, 3.6) * mm, "end": v(-3.05, 3.58) * mm});
            skLineSegment(sketch, "E12.5.1.39", {"start": v(-3.07, 3.27) * mm, "end": v(-3.05, 3.25) * mm});
            skLineSegment(sketch, "E12.5.1.40", {"start": v(-3.07, 3.76) * mm, "end": v(-3.05, 3.74) * mm});
            skLineSegment(sketch, "E12.5.1.41", {"start": v(-3.07, 3.43) * mm, "end": v(-3.05, 3.41) * mm});
            skLineSegment(sketch, "E12.5.1.42", {"start": v(-3.07, 4.08) * mm, "end": v(-3.05, 4.06) * mm});
            skLineSegment(sketch, "E12.5.1.43", {"start": v(-3.17, 3.82) * mm, "end": v(-3.15, 3.84) * mm});
            skLineSegment(sketch, "E12.5.1.44", {"start": v(-3.17, 3.82) * mm, "end": v(-3.15, 3.8) * mm});
            skLineSegment(sketch, "E12.5.1.45", {"start": v(-3.17, 3.17) * mm, "end": v(-3.15, 3.15) * mm});
            skLineSegment(sketch, "E12.5.1.46", {"start": v(-3.15, 3.8) * mm, "end": v(-3.13, 3.82) * mm});
            skLineSegment(sketch, "E12.5.1.47", {"start": v(-3.15, 3.15) * mm, "end": v(-3.13, 3.17) * mm});
            skLineSegment(sketch, "E12.5.1.48", {"start": v(-3.15, 3.96) * mm, "end": v(-3.13, 3.98) * mm});
            skLineSegment(sketch, "E12.5.1.49", {"start": v(-3.17, 3.33) * mm, "end": v(-3.15, 3.32) * mm});
            skLineSegment(sketch, "E12.5.1.50", {"start": v(-3.17, 3.66) * mm, "end": v(-3.15, 3.64) * mm});
            skLineSegment(sketch, "E12.5.1.51", {"start": v(-3.15, 3.64) * mm, "end": v(-3.13, 3.66) * mm});
            skLineSegment(sketch, "E12.5.1.52", {"start": v(-3.17, 3.5) * mm, "end": v(-3.15, 3.48) * mm});
            skLineSegment(sketch, "E12.5.1.53", {"start": v(-3.17, 3.66) * mm, "end": v(-3.15, 3.68) * mm});
            skLineSegment(sketch, "E12.5.1.54", {"start": v(-3.17, 3.33) * mm, "end": v(-3.15, 3.35) * mm});
            skLineSegment(sketch, "E12.5.1.55", {"start": v(-3.17, 3.98) * mm, "end": v(-3.15, 4) * mm});
            skLineSegment(sketch, "E12.5.1.56", {"start": v(-3.17, 3.98) * mm, "end": v(-3.15, 3.96) * mm});
            skLineSegment(sketch, "E12.5.1.57", {"start": v(-3.17, 3.5) * mm, "end": v(-3.15, 3.51) * mm});
            skLineSegment(sketch, "E12.5.1.58", {"start": v(-3.15, 3.48) * mm, "end": v(-3.13, 3.5) * mm});
            skLineSegment(sketch, "E12.5.1.59", {"start": v(-3.15, 3.32) * mm, "end": v(-3.13, 3.33) * mm});
            skLineSegment(sketch, "E12.6.0.0", {"start": v(-2.91, 1.53) * mm, "end": v(-3.01, 1.63) * mm});
            skLineSegment(sketch, "E12.6.0.1", {"start": v(-2.91, 1.2) * mm, "end": v(-3.01, 1.3) * mm});
            skPoint(sketch, "E12.6.0.2", {"position": v(-2.96, 1.99) * mm});
            skLineSegment(sketch, "E12.6.0.3", {"start": v(-2.9, 2.03) * mm, "end": v(-3, 2.13) * mm});
            skPoint(sketch, "E12.6.0.4", {"position": v(-3.04, 1.34) * mm});
            skLineSegment(sketch, "E12.6.0.5", {"start": v(-2.91, 2.01) * mm, "end": v(-3.01, 2.1) * mm});
            skPoint(sketch, "E12.6.0.6", {"position": v(-3.04, 1.5) * mm});
            skPoint(sketch, "E12.6.0.7", {"position": v(-3.04, 1.83) * mm});
            skPoint(sketch, "E12.6.0.8", {"position": v(-2.96, 1.34) * mm});
            skPoint(sketch, "E12.6.0.9", {"position": v(-2.96, 1.67) * mm});
            skLineSegment(sketch, "E12.6.0.10", {"start": v(-2.91, 1.36) * mm, "end": v(-3.01, 1.46) * mm});
            skPoint(sketch, "E12.6.0.11", {"position": v(-2.96, 1.5) * mm});
            skPoint(sketch, "E12.6.0.12", {"position": v(-2.96, 1.18) * mm});
            skLineSegment(sketch, "E12.6.0.13", {"start": v(-2.91, 1.69) * mm, "end": v(-3.01, 1.79) * mm});
            skPoint(sketch, "E12.6.0.14", {"position": v(-3.04, 1.99) * mm});
            skPoint(sketch, "E12.6.0.15", {"position": v(-3.04, 1.67) * mm});
            skLineSegment(sketch, "E12.6.0.16", {"start": v(-2.91, 1.85) * mm, "end": v(-3.01, 1.95) * mm});
            skPoint(sketch, "E12.6.0.17", {"position": v(-3.04, 1.18) * mm});
            skPoint(sketch, "E12.6.0.18", {"position": v(-2.96, 1.83) * mm});
            skLineSegment(sketch, "E12.6.0.19", {"start": v(-2.9, 1.38) * mm, "end": v(-3, 1.48) * mm});
            skLineSegment(sketch, "E12.6.0.20", {"start": v(-3.01, 1.95) * mm, "end": v(-2.91, 2.05) * mm});
            skLineSegment(sketch, "E12.6.0.21", {"start": v(-3, 1.77) * mm, "end": v(-2.9, 1.87) * mm});
            skLineSegment(sketch, "E12.6.0.22", {"start": v(-2.9, 1.54) * mm, "end": v(-3, 1.64) * mm});
            skLineSegment(sketch, "E12.6.0.23", {"start": v(-3, 1.28) * mm, "end": v(-2.9, 1.38) * mm});
            skLineSegment(sketch, "E12.6.0.24", {"start": v(-3, 1.6) * mm, "end": v(-2.9, 1.7) * mm});
            skLineSegment(sketch, "E12.6.0.25", {"start": v(-3.01, 1.46) * mm, "end": v(-2.91, 1.56) * mm});
            skLineSegment(sketch, "E12.6.0.26", {"start": v(-3.01, 1.14) * mm, "end": v(-2.91, 1.24) * mm});
            skLineSegment(sketch, "E12.6.0.27", {"start": v(-3, 1.45) * mm, "end": v(-2.9, 1.54) * mm});
            skLineSegment(sketch, "E12.6.0.28", {"start": v(-3.01, 1.3) * mm, "end": v(-2.91, 1.4) * mm});
            skLineSegment(sketch, "E12.6.0.29", {"start": v(-3, 1.12) * mm, "end": v(-2.9, 1.22) * mm});
            skLineSegment(sketch, "E12.6.0.30", {"start": v(-3.01, 1.63) * mm, "end": v(-2.91, 1.72) * mm});
            skLineSegment(sketch, "E12.6.0.31", {"start": v(-3.01, 1.79) * mm, "end": v(-2.91, 1.89) * mm});
            skLineSegment(sketch, "E12.6.0.32", {"start": v(-3, 1.93) * mm, "end": v(-2.9, 2.03) * mm});
            skLineSegment(sketch, "E12.6.0.33", {"start": v(-3.01, 2.1) * mm, "end": v(-3, 2.13) * mm});
            skLineSegment(sketch, "E12.6.0.34", {"start": v(-2.9, 1.7) * mm, "end": v(-3, 1.8) * mm});
            skLineSegment(sketch, "E12.6.0.35", {"start": v(-2.9, 1.22) * mm, "end": v(-3, 1.32) * mm});
            skLineSegment(sketch, "E12.6.0.36", {"start": v(-2.9, 1.87) * mm, "end": v(-3, 1.97) * mm});
            skLineSegment(sketch, "E12.6.0.37", {"start": v(-2.91, 1.89) * mm, "end": v(-2.9, 1.87) * mm});
            skLineSegment(sketch, "E12.6.0.38", {"start": v(-2.91, 1.56) * mm, "end": v(-2.9, 1.54) * mm});
            skLineSegment(sketch, "E12.6.0.39", {"start": v(-2.91, 1.24) * mm, "end": v(-2.9, 1.22) * mm});
            skLineSegment(sketch, "E12.6.0.40", {"start": v(-2.91, 1.72) * mm, "end": v(-2.9, 1.7) * mm});
            skLineSegment(sketch, "E12.6.0.41", {"start": v(-2.91, 1.4) * mm, "end": v(-2.9, 1.38) * mm});
            skLineSegment(sketch, "E12.6.0.42", {"start": v(-2.91, 2.05) * mm, "end": v(-2.9, 2.03) * mm});
            skLineSegment(sketch, "E12.6.0.43", {"start": v(-3.01, 1.79) * mm, "end": v(-3, 1.8) * mm});
            skLineSegment(sketch, "E12.6.0.44", {"start": v(-3.01, 1.79) * mm, "end": v(-3, 1.77) * mm});
            skLineSegment(sketch, "E12.6.0.45", {"start": v(-3.01, 1.14) * mm, "end": v(-3, 1.12) * mm});
            skLineSegment(sketch, "E12.6.0.46", {"start": v(-3, 1.77) * mm, "end": v(-2.98, 1.79) * mm});
            skLineSegment(sketch, "E12.6.0.47", {"start": v(-3, 1.12) * mm, "end": v(-2.98, 1.14) * mm});
            skLineSegment(sketch, "E12.6.0.48", {"start": v(-3, 1.93) * mm, "end": v(-2.98, 1.95) * mm});
            skLineSegment(sketch, "E12.6.0.49", {"start": v(-3.01, 1.3) * mm, "end": v(-3, 1.28) * mm});
            skLineSegment(sketch, "E12.6.0.50", {"start": v(-3.01, 1.63) * mm, "end": v(-3, 1.6) * mm});
            skLineSegment(sketch, "E12.6.0.51", {"start": v(-3, 1.6) * mm, "end": v(-2.98, 1.62) * mm});
            skLineSegment(sketch, "E12.6.0.52", {"start": v(-3.01, 1.46) * mm, "end": v(-3, 1.45) * mm});
            skLineSegment(sketch, "E12.6.0.53", {"start": v(-3.01, 1.63) * mm, "end": v(-3, 1.64) * mm});
            skLineSegment(sketch, "E12.6.0.54", {"start": v(-3.01, 1.3) * mm, "end": v(-3, 1.32) * mm});
            skLineSegment(sketch, "E12.6.0.55", {"start": v(-3.01, 1.95) * mm, "end": v(-3, 1.97) * mm});
            skLineSegment(sketch, "E12.6.0.56", {"start": v(-3.01, 1.95) * mm, "end": v(-3, 1.93) * mm});
            skLineSegment(sketch, "E12.6.0.57", {"start": v(-3.01, 1.46) * mm, "end": v(-3, 1.48) * mm});
            skLineSegment(sketch, "E12.6.0.58", {"start": v(-3, 1.45) * mm, "end": v(-2.98, 1.46) * mm});
            skLineSegment(sketch, "E12.6.0.59", {"start": v(-3, 1.28) * mm, "end": v(-2.98, 1.3) * mm});
            skLineSegment(sketch, "E12.6.1.0", {"start": v(-2.91, 3.56) * mm, "end": v(-3.01, 3.66) * mm});
            skLineSegment(sketch, "E12.6.1.1", {"start": v(-2.91, 3.24) * mm, "end": v(-3.01, 3.33) * mm});
            skPoint(sketch, "E12.6.1.2", {"position": v(-2.96, 4.02) * mm});
            skLineSegment(sketch, "E12.6.1.3", {"start": v(-2.9, 4.06) * mm, "end": v(-3, 4.16) * mm});
            skPoint(sketch, "E12.6.1.4", {"position": v(-3.04, 3.37) * mm});
            skLineSegment(sketch, "E12.6.1.5", {"start": v(-2.91, 4.04) * mm, "end": v(-3.01, 4.14) * mm});
            skPoint(sketch, "E12.6.1.6", {"position": v(-3.04, 3.54) * mm});
            skPoint(sketch, "E12.6.1.7", {"position": v(-3.04, 3.86) * mm});
            skPoint(sketch, "E12.6.1.8", {"position": v(-2.96, 3.37) * mm});
            skPoint(sketch, "E12.6.1.9", {"position": v(-2.96, 3.7) * mm});
            skLineSegment(sketch, "E12.6.1.10", {"start": v(-2.91, 3.4) * mm, "end": v(-3.01, 3.5) * mm});
            skPoint(sketch, "E12.6.1.11", {"position": v(-2.96, 3.54) * mm});
            skPoint(sketch, "E12.6.1.12", {"position": v(-2.96, 3.21) * mm});
            skLineSegment(sketch, "E12.6.1.13", {"start": v(-2.91, 3.72) * mm, "end": v(-3.01, 3.82) * mm});
            skPoint(sketch, "E12.6.1.14", {"position": v(-3.04, 4.02) * mm});
            skPoint(sketch, "E12.6.1.15", {"position": v(-3.04, 3.7) * mm});
            skLineSegment(sketch, "E12.6.1.16", {"start": v(-2.91, 3.88) * mm, "end": v(-3.01, 3.98) * mm});
            skPoint(sketch, "E12.6.1.17", {"position": v(-3.04, 3.21) * mm});
            skPoint(sketch, "E12.6.1.18", {"position": v(-2.96, 3.86) * mm});
            skLineSegment(sketch, "E12.6.1.19", {"start": v(-2.9, 3.41) * mm, "end": v(-3, 3.51) * mm});
            skLineSegment(sketch, "E12.6.1.20", {"start": v(-3.01, 3.98) * mm, "end": v(-2.91, 4.08) * mm});
            skLineSegment(sketch, "E12.6.1.21", {"start": v(-3, 3.8) * mm, "end": v(-2.9, 3.9) * mm});
            skLineSegment(sketch, "E12.6.1.22", {"start": v(-2.9, 3.58) * mm, "end": v(-3, 3.68) * mm});
            skLineSegment(sketch, "E12.6.1.23", {"start": v(-3, 3.32) * mm, "end": v(-2.9, 3.41) * mm});
            skLineSegment(sketch, "E12.6.1.24", {"start": v(-3, 3.64) * mm, "end": v(-2.9, 3.74) * mm});
            skLineSegment(sketch, "E12.6.1.25", {"start": v(-3.01, 3.5) * mm, "end": v(-2.91, 3.6) * mm});
            skLineSegment(sketch, "E12.6.1.26", {"start": v(-3.01, 3.17) * mm, "end": v(-2.91, 3.27) * mm});
            skLineSegment(sketch, "E12.6.1.27", {"start": v(-3, 3.48) * mm, "end": v(-2.9, 3.58) * mm});
            skLineSegment(sketch, "E12.6.1.28", {"start": v(-3.01, 3.33) * mm, "end": v(-2.91, 3.43) * mm});
            skLineSegment(sketch, "E12.6.1.29", {"start": v(-3, 3.15) * mm, "end": v(-2.9, 3.25) * mm});
            skLineSegment(sketch, "E12.6.1.30", {"start": v(-3.01, 3.66) * mm, "end": v(-2.91, 3.76) * mm});
            skLineSegment(sketch, "E12.6.1.31", {"start": v(-3.01, 3.82) * mm, "end": v(-2.91, 3.92) * mm});
            skLineSegment(sketch, "E12.6.1.32", {"start": v(-3, 3.96) * mm, "end": v(-2.9, 4.06) * mm});
            skLineSegment(sketch, "E12.6.1.33", {"start": v(-3.01, 4.14) * mm, "end": v(-3, 4.16) * mm});
            skLineSegment(sketch, "E12.6.1.34", {"start": v(-2.9, 3.74) * mm, "end": v(-3, 3.84) * mm});
            skLineSegment(sketch, "E12.6.1.35", {"start": v(-2.9, 3.25) * mm, "end": v(-3, 3.35) * mm});
            skLineSegment(sketch, "E12.6.1.36", {"start": v(-2.9, 3.9) * mm, "end": v(-3, 4) * mm});
            skLineSegment(sketch, "E12.6.1.37", {"start": v(-2.91, 3.92) * mm, "end": v(-2.9, 3.9) * mm});
            skLineSegment(sketch, "E12.6.1.38", {"start": v(-2.91, 3.6) * mm, "end": v(-2.9, 3.58) * mm});
            skLineSegment(sketch, "E12.6.1.39", {"start": v(-2.91, 3.27) * mm, "end": v(-2.9, 3.25) * mm});
            skLineSegment(sketch, "E12.6.1.40", {"start": v(-2.91, 3.76) * mm, "end": v(-2.9, 3.74) * mm});
            skLineSegment(sketch, "E12.6.1.41", {"start": v(-2.91, 3.43) * mm, "end": v(-2.9, 3.41) * mm});
            skLineSegment(sketch, "E12.6.1.42", {"start": v(-2.91, 4.08) * mm, "end": v(-2.9, 4.06) * mm});
            skLineSegment(sketch, "E12.6.1.43", {"start": v(-3.01, 3.82) * mm, "end": v(-3, 3.84) * mm});
            skLineSegment(sketch, "E12.6.1.44", {"start": v(-3.01, 3.82) * mm, "end": v(-3, 3.8) * mm});
            skLineSegment(sketch, "E12.6.1.45", {"start": v(-3.01, 3.17) * mm, "end": v(-3, 3.15) * mm});
            skLineSegment(sketch, "E12.6.1.46", {"start": v(-3, 3.8) * mm, "end": v(-2.98, 3.82) * mm});
            skLineSegment(sketch, "E12.6.1.47", {"start": v(-3, 3.15) * mm, "end": v(-2.98, 3.17) * mm});
            skLineSegment(sketch, "E12.6.1.48", {"start": v(-3, 3.96) * mm, "end": v(-2.98, 3.98) * mm});
            skLineSegment(sketch, "E12.6.1.49", {"start": v(-3.01, 3.33) * mm, "end": v(-3, 3.32) * mm});
            skLineSegment(sketch, "E12.6.1.50", {"start": v(-3.01, 3.66) * mm, "end": v(-3, 3.64) * mm});
            skLineSegment(sketch, "E12.6.1.51", {"start": v(-3, 3.64) * mm, "end": v(-2.98, 3.66) * mm});
            skLineSegment(sketch, "E12.6.1.52", {"start": v(-3.01, 3.5) * mm, "end": v(-3, 3.48) * mm});
            skLineSegment(sketch, "E12.6.1.53", {"start": v(-3.01, 3.66) * mm, "end": v(-3, 3.68) * mm});
            skLineSegment(sketch, "E12.6.1.54", {"start": v(-3.01, 3.33) * mm, "end": v(-3, 3.35) * mm});
            skLineSegment(sketch, "E12.6.1.55", {"start": v(-3.01, 3.98) * mm, "end": v(-3, 4) * mm});
            skLineSegment(sketch, "E12.6.1.56", {"start": v(-3.01, 3.98) * mm, "end": v(-3, 3.96) * mm});
            skLineSegment(sketch, "E12.6.1.57", {"start": v(-3.01, 3.5) * mm, "end": v(-3, 3.51) * mm});
            skLineSegment(sketch, "E12.6.1.58", {"start": v(-3, 3.48) * mm, "end": v(-2.98, 3.5) * mm});
            skLineSegment(sketch, "E12.6.1.59", {"start": v(-3, 3.32) * mm, "end": v(-2.98, 3.33) * mm});
            skLineSegment(sketch, "E12.7.0.0", {"start": v(-2.76, 1.53) * mm, "end": v(-2.86, 1.63) * mm});
            skLineSegment(sketch, "E12.7.0.1", {"start": v(-2.76, 1.2) * mm, "end": v(-2.86, 1.3) * mm});
            skPoint(sketch, "E12.7.0.2", {"position": v(-2.8, 1.99) * mm});
            skLineSegment(sketch, "E12.7.0.3", {"start": v(-2.74, 2.03) * mm, "end": v(-2.84, 2.13) * mm});
            skPoint(sketch, "E12.7.0.4", {"position": v(-2.88, 1.34) * mm});
            skLineSegment(sketch, "E12.7.0.5", {"start": v(-2.76, 2.01) * mm, "end": v(-2.86, 2.1) * mm});
            skPoint(sketch, "E12.7.0.6", {"position": v(-2.88, 1.5) * mm});
            skPoint(sketch, "E12.7.0.7", {"position": v(-2.88, 1.83) * mm});
            skPoint(sketch, "E12.7.0.8", {"position": v(-2.8, 1.34) * mm});
            skPoint(sketch, "E12.7.0.9", {"position": v(-2.8, 1.67) * mm});
            skLineSegment(sketch, "E12.7.0.10", {"start": v(-2.76, 1.36) * mm, "end": v(-2.86, 1.46) * mm});
            skPoint(sketch, "E12.7.0.11", {"position": v(-2.8, 1.5) * mm});
            skPoint(sketch, "E12.7.0.12", {"position": v(-2.8, 1.18) * mm});
            skLineSegment(sketch, "E12.7.0.13", {"start": v(-2.76, 1.69) * mm, "end": v(-2.86, 1.79) * mm});
            skPoint(sketch, "E12.7.0.14", {"position": v(-2.88, 1.99) * mm});
            skPoint(sketch, "E12.7.0.15", {"position": v(-2.88, 1.67) * mm});
            skLineSegment(sketch, "E12.7.0.16", {"start": v(-2.76, 1.85) * mm, "end": v(-2.86, 1.95) * mm});
            skPoint(sketch, "E12.7.0.17", {"position": v(-2.88, 1.18) * mm});
            skPoint(sketch, "E12.7.0.18", {"position": v(-2.8, 1.83) * mm});
            skLineSegment(sketch, "E12.7.0.19", {"start": v(-2.74, 1.38) * mm, "end": v(-2.84, 1.48) * mm});
            skLineSegment(sketch, "E12.7.0.20", {"start": v(-2.86, 1.95) * mm, "end": v(-2.76, 2.05) * mm});
            skLineSegment(sketch, "E12.7.0.21", {"start": v(-2.84, 1.77) * mm, "end": v(-2.74, 1.87) * mm});
            skLineSegment(sketch, "E12.7.0.22", {"start": v(-2.74, 1.54) * mm, "end": v(-2.84, 1.64) * mm});
            skLineSegment(sketch, "E12.7.0.23", {"start": v(-2.84, 1.28) * mm, "end": v(-2.74, 1.38) * mm});
            skLineSegment(sketch, "E12.7.0.24", {"start": v(-2.84, 1.6) * mm, "end": v(-2.74, 1.7) * mm});
            skLineSegment(sketch, "E12.7.0.25", {"start": v(-2.86, 1.46) * mm, "end": v(-2.76, 1.56) * mm});
            skLineSegment(sketch, "E12.7.0.26", {"start": v(-2.86, 1.14) * mm, "end": v(-2.76, 1.24) * mm});
            skLineSegment(sketch, "E12.7.0.27", {"start": v(-2.84, 1.45) * mm, "end": v(-2.74, 1.54) * mm});
            skLineSegment(sketch, "E12.7.0.28", {"start": v(-2.86, 1.3) * mm, "end": v(-2.76, 1.4) * mm});
            skLineSegment(sketch, "E12.7.0.29", {"start": v(-2.84, 1.12) * mm, "end": v(-2.74, 1.22) * mm});
            skLineSegment(sketch, "E12.7.0.30", {"start": v(-2.86, 1.63) * mm, "end": v(-2.76, 1.72) * mm});
            skLineSegment(sketch, "E12.7.0.31", {"start": v(-2.86, 1.79) * mm, "end": v(-2.76, 1.89) * mm});
            skLineSegment(sketch, "E12.7.0.32", {"start": v(-2.84, 1.93) * mm, "end": v(-2.74, 2.03) * mm});
            skLineSegment(sketch, "E12.7.0.33", {"start": v(-2.86, 2.1) * mm, "end": v(-2.84, 2.13) * mm});
            skLineSegment(sketch, "E12.7.0.34", {"start": v(-2.74, 1.7) * mm, "end": v(-2.84, 1.8) * mm});
            skLineSegment(sketch, "E12.7.0.35", {"start": v(-2.74, 1.22) * mm, "end": v(-2.84, 1.32) * mm});
            skLineSegment(sketch, "E12.7.0.36", {"start": v(-2.74, 1.87) * mm, "end": v(-2.84, 1.97) * mm});
            skLineSegment(sketch, "E12.7.0.37", {"start": v(-2.76, 1.89) * mm, "end": v(-2.74, 1.87) * mm});
            skLineSegment(sketch, "E12.7.0.38", {"start": v(-2.76, 1.56) * mm, "end": v(-2.74, 1.54) * mm});
            skLineSegment(sketch, "E12.7.0.39", {"start": v(-2.76, 1.24) * mm, "end": v(-2.74, 1.22) * mm});
            skLineSegment(sketch, "E12.7.0.40", {"start": v(-2.76, 1.72) * mm, "end": v(-2.74, 1.7) * mm});
            skLineSegment(sketch, "E12.7.0.41", {"start": v(-2.76, 1.4) * mm, "end": v(-2.74, 1.38) * mm});
            skLineSegment(sketch, "E12.7.0.42", {"start": v(-2.76, 2.05) * mm, "end": v(-2.74, 2.03) * mm});
            skLineSegment(sketch, "E12.7.0.43", {"start": v(-2.86, 1.79) * mm, "end": v(-2.84, 1.8) * mm});
            skLineSegment(sketch, "E12.7.0.44", {"start": v(-2.86, 1.79) * mm, "end": v(-2.84, 1.77) * mm});
            skLineSegment(sketch, "E12.7.0.45", {"start": v(-2.86, 1.14) * mm, "end": v(-2.84, 1.12) * mm});
            skLineSegment(sketch, "E12.7.0.46", {"start": v(-2.84, 1.77) * mm, "end": v(-2.83, 1.79) * mm});
            skLineSegment(sketch, "E12.7.0.47", {"start": v(-2.84, 1.12) * mm, "end": v(-2.82, 1.14) * mm});
            skLineSegment(sketch, "E12.7.0.48", {"start": v(-2.84, 1.93) * mm, "end": v(-2.83, 1.95) * mm});
            skLineSegment(sketch, "E12.7.0.49", {"start": v(-2.86, 1.3) * mm, "end": v(-2.84, 1.28) * mm});
            skLineSegment(sketch, "E12.7.0.50", {"start": v(-2.86, 1.63) * mm, "end": v(-2.84, 1.6) * mm});
            skLineSegment(sketch, "E12.7.0.51", {"start": v(-2.84, 1.6) * mm, "end": v(-2.82, 1.62) * mm});
            skLineSegment(sketch, "E12.7.0.52", {"start": v(-2.86, 1.46) * mm, "end": v(-2.84, 1.45) * mm});
            skLineSegment(sketch, "E12.7.0.53", {"start": v(-2.86, 1.63) * mm, "end": v(-2.84, 1.64) * mm});
            skLineSegment(sketch, "E12.7.0.54", {"start": v(-2.86, 1.3) * mm, "end": v(-2.84, 1.32) * mm});
            skLineSegment(sketch, "E12.7.0.55", {"start": v(-2.86, 1.95) * mm, "end": v(-2.84, 1.97) * mm});
            skLineSegment(sketch, "E12.7.0.56", {"start": v(-2.86, 1.95) * mm, "end": v(-2.84, 1.93) * mm});
            skLineSegment(sketch, "E12.7.0.57", {"start": v(-2.86, 1.46) * mm, "end": v(-2.84, 1.48) * mm});
            skLineSegment(sketch, "E12.7.0.58", {"start": v(-2.84, 1.45) * mm, "end": v(-2.82, 1.46) * mm});
            skLineSegment(sketch, "E12.7.0.59", {"start": v(-2.84, 1.28) * mm, "end": v(-2.82, 1.3) * mm});
            skLineSegment(sketch, "E12.7.1.0", {"start": v(-2.76, 3.56) * mm, "end": v(-2.86, 3.66) * mm});
            skLineSegment(sketch, "E12.7.1.1", {"start": v(-2.76, 3.24) * mm, "end": v(-2.86, 3.33) * mm});
            skPoint(sketch, "E12.7.1.2", {"position": v(-2.8, 4.02) * mm});
            skLineSegment(sketch, "E12.7.1.3", {"start": v(-2.74, 4.06) * mm, "end": v(-2.84, 4.16) * mm});
            skPoint(sketch, "E12.7.1.4", {"position": v(-2.88, 3.37) * mm});
            skLineSegment(sketch, "E12.7.1.5", {"start": v(-2.76, 4.04) * mm, "end": v(-2.86, 4.14) * mm});
            skPoint(sketch, "E12.7.1.6", {"position": v(-2.88, 3.54) * mm});
            skPoint(sketch, "E12.7.1.7", {"position": v(-2.88, 3.86) * mm});
            skPoint(sketch, "E12.7.1.8", {"position": v(-2.8, 3.37) * mm});
            skPoint(sketch, "E12.7.1.9", {"position": v(-2.8, 3.7) * mm});
            skLineSegment(sketch, "E12.7.1.10", {"start": v(-2.76, 3.4) * mm, "end": v(-2.86, 3.5) * mm});
            skPoint(sketch, "E12.7.1.11", {"position": v(-2.8, 3.54) * mm});
            skPoint(sketch, "E12.7.1.12", {"position": v(-2.8, 3.21) * mm});
            skLineSegment(sketch, "E12.7.1.13", {"start": v(-2.76, 3.72) * mm, "end": v(-2.86, 3.82) * mm});
            skPoint(sketch, "E12.7.1.14", {"position": v(-2.88, 4.02) * mm});
            skPoint(sketch, "E12.7.1.15", {"position": v(-2.88, 3.7) * mm});
            skLineSegment(sketch, "E12.7.1.16", {"start": v(-2.76, 3.88) * mm, "end": v(-2.86, 3.98) * mm});
            skPoint(sketch, "E12.7.1.17", {"position": v(-2.88, 3.21) * mm});
            skPoint(sketch, "E12.7.1.18", {"position": v(-2.8, 3.86) * mm});
            skLineSegment(sketch, "E12.7.1.19", {"start": v(-2.74, 3.41) * mm, "end": v(-2.84, 3.51) * mm});
            skLineSegment(sketch, "E12.7.1.20", {"start": v(-2.86, 3.98) * mm, "end": v(-2.76, 4.08) * mm});
            skLineSegment(sketch, "E12.7.1.21", {"start": v(-2.84, 3.8) * mm, "end": v(-2.74, 3.9) * mm});
            skLineSegment(sketch, "E12.7.1.22", {"start": v(-2.74, 3.58) * mm, "end": v(-2.84, 3.68) * mm});
            skLineSegment(sketch, "E12.7.1.23", {"start": v(-2.84, 3.32) * mm, "end": v(-2.74, 3.41) * mm});
            skLineSegment(sketch, "E12.7.1.24", {"start": v(-2.84, 3.64) * mm, "end": v(-2.74, 3.74) * mm});
            skLineSegment(sketch, "E12.7.1.25", {"start": v(-2.86, 3.5) * mm, "end": v(-2.76, 3.6) * mm});
            skLineSegment(sketch, "E12.7.1.26", {"start": v(-2.86, 3.17) * mm, "end": v(-2.76, 3.27) * mm});
            skLineSegment(sketch, "E12.7.1.27", {"start": v(-2.84, 3.48) * mm, "end": v(-2.74, 3.58) * mm});
            skLineSegment(sketch, "E12.7.1.28", {"start": v(-2.86, 3.33) * mm, "end": v(-2.76, 3.43) * mm});
            skLineSegment(sketch, "E12.7.1.29", {"start": v(-2.84, 3.15) * mm, "end": v(-2.74, 3.25) * mm});
            skLineSegment(sketch, "E12.7.1.30", {"start": v(-2.86, 3.66) * mm, "end": v(-2.76, 3.76) * mm});
            skLineSegment(sketch, "E12.7.1.31", {"start": v(-2.86, 3.82) * mm, "end": v(-2.76, 3.92) * mm});
            skLineSegment(sketch, "E12.7.1.32", {"start": v(-2.84, 3.96) * mm, "end": v(-2.74, 4.06) * mm});
            skLineSegment(sketch, "E12.7.1.33", {"start": v(-2.86, 4.14) * mm, "end": v(-2.84, 4.16) * mm});
            skLineSegment(sketch, "E12.7.1.34", {"start": v(-2.74, 3.74) * mm, "end": v(-2.84, 3.84) * mm});
            skLineSegment(sketch, "E12.7.1.35", {"start": v(-2.74, 3.25) * mm, "end": v(-2.84, 3.35) * mm});
            skLineSegment(sketch, "E12.7.1.36", {"start": v(-2.74, 3.9) * mm, "end": v(-2.84, 4) * mm});
            skLineSegment(sketch, "E12.7.1.37", {"start": v(-2.76, 3.92) * mm, "end": v(-2.74, 3.9) * mm});
            skLineSegment(sketch, "E12.7.1.38", {"start": v(-2.76, 3.6) * mm, "end": v(-2.74, 3.58) * mm});
            skLineSegment(sketch, "E12.7.1.39", {"start": v(-2.76, 3.27) * mm, "end": v(-2.74, 3.25) * mm});
            skLineSegment(sketch, "E12.7.1.40", {"start": v(-2.76, 3.76) * mm, "end": v(-2.74, 3.74) * mm});
            skLineSegment(sketch, "E12.7.1.41", {"start": v(-2.76, 3.43) * mm, "end": v(-2.74, 3.41) * mm});
            skLineSegment(sketch, "E12.7.1.42", {"start": v(-2.76, 4.08) * mm, "end": v(-2.74, 4.06) * mm});
            skLineSegment(sketch, "E12.7.1.43", {"start": v(-2.86, 3.82) * mm, "end": v(-2.84, 3.84) * mm});
            skLineSegment(sketch, "E12.7.1.44", {"start": v(-2.86, 3.82) * mm, "end": v(-2.84, 3.8) * mm});
            skLineSegment(sketch, "E12.7.1.45", {"start": v(-2.86, 3.17) * mm, "end": v(-2.84, 3.15) * mm});
            skLineSegment(sketch, "E12.7.1.46", {"start": v(-2.84, 3.8) * mm, "end": v(-2.83, 3.82) * mm});
            skLineSegment(sketch, "E12.7.1.47", {"start": v(-2.84, 3.15) * mm, "end": v(-2.82, 3.17) * mm});
            skLineSegment(sketch, "E12.7.1.48", {"start": v(-2.84, 3.96) * mm, "end": v(-2.83, 3.98) * mm});
            skLineSegment(sketch, "E12.7.1.49", {"start": v(-2.86, 3.33) * mm, "end": v(-2.84, 3.32) * mm});
            skLineSegment(sketch, "E12.7.1.50", {"start": v(-2.86, 3.66) * mm, "end": v(-2.84, 3.64) * mm});
            skLineSegment(sketch, "E12.7.1.51", {"start": v(-2.84, 3.64) * mm, "end": v(-2.82, 3.66) * mm});
            skLineSegment(sketch, "E12.7.1.52", {"start": v(-2.86, 3.5) * mm, "end": v(-2.84, 3.48) * mm});
            skLineSegment(sketch, "E12.7.1.53", {"start": v(-2.86, 3.66) * mm, "end": v(-2.84, 3.68) * mm});
            skLineSegment(sketch, "E12.7.1.54", {"start": v(-2.86, 3.33) * mm, "end": v(-2.84, 3.35) * mm});
            skLineSegment(sketch, "E12.7.1.55", {"start": v(-2.86, 3.98) * mm, "end": v(-2.84, 4) * mm});
            skLineSegment(sketch, "E12.7.1.56", {"start": v(-2.86, 3.98) * mm, "end": v(-2.84, 3.96) * mm});
            skLineSegment(sketch, "E12.7.1.57", {"start": v(-2.86, 3.5) * mm, "end": v(-2.84, 3.51) * mm});
            skLineSegment(sketch, "E12.7.1.58", {"start": v(-2.84, 3.48) * mm, "end": v(-2.82, 3.5) * mm});
            skLineSegment(sketch, "E12.7.1.59", {"start": v(-2.84, 3.32) * mm, "end": v(-2.82, 3.33) * mm});
            skLineSegment(sketch, "E12.direction1", {"start": v(-3.9, 1.12) * mm, "end": v(-3.76, 1.12) * mm, "construction": true});
            skLineSegment(sketch, "E12.direction2", {"start": v(-3.9, 1.12) * mm, "end": v(-3.9, 3.15) * mm, "construction": true});
            skSolve(sketch);
        }
        {
            var Q0;
            {var subQ0=sQuery(id+"F0.wireOp",EDGE,"E12.2.0.3");Q0=makeQuery(id+"F0.imprint","IMPRINT",FACE,{"disambiguationData":[TD([[makeQuery(id+"F0.imprint","IMPRINT",EDGE,{"derivedFrom":subQ0}),1.0]])]});}
            var Q1;
            {var subQ4=sQuery(id+"F0.wireOp",EDGE,"E0.top");Q1=makeQuery(id+"F0.imprint","IMPRINT",FACE,{"disambiguationData":[TD([[makeQuery(id+"F0.imprint","IMPRINT",EDGE,{"derivedFrom":subQ4}),1.0]])]});}
            var Q2;
            {var subQ0=sQuery(id+"F0.wireOp",EDGE,"E12.1.0.3");Q2=makeQuery(id+"F0.imprint","IMPRINT",FACE,{"disambiguationData":[TD([[makeQuery(id+"F0.imprint","IMPRINT",EDGE,{"derivedFrom":subQ0}),1.0]])]});}
            var Q3;
            {var subQ1=sQuery(id+"F0.wireOp",EDGE,"E12.4.0.13");var subQ5=makeQuery(id+"F0.imprint","IMPRINT",VERTEX,{"derivedFrom":subQ1});Q3=makeQuery(id+"F0.imprint","IMPRINT",FACE,{"disambiguationData":[TD([[makeQuery(id+"F0.imprint","IMPRINT",EDGE,{"disambiguationData":[TD([[subQ5,1.0]])],"derivedFrom":subQ1}),-1.0]])]});}
            var Q4;
            {var subQ1=sQuery(id+"F0.wireOp",EDGE,"E12.6.0.13");var subQ5=makeQuery(id+"F0.imprint","IMPRINT",VERTEX,{"derivedFrom":subQ1});Q4=makeQuery(id+"F0.imprint","IMPRINT",FACE,{"disambiguationData":[TD([[makeQuery(id+"F0.imprint","IMPRINT",EDGE,{"disambiguationData":[TD([[subQ5,1.0]])],"derivedFrom":subQ1}),-1.0]])]});}
            var Q5;
            {var subQ1=sQuery(id+"F0.wireOp",EDGE,"E12.5.0.13");var subQ5=makeQuery(id+"F0.imprint","IMPRINT",VERTEX,{"derivedFrom":subQ1});Q5=makeQuery(id+"F0.imprint","IMPRINT",FACE,{"disambiguationData":[TD([[makeQuery(id+"F0.imprint","IMPRINT",EDGE,{"disambiguationData":[TD([[subQ5,1.0]])],"derivedFrom":subQ1}),-1.0]])]});}
            var Q6;
            {var subQ1=sQuery(id+"F0.wireOp",EDGE,"E12.7.0.13");var subQ5=makeQuery(id+"F0.imprint","IMPRINT",VERTEX,{"derivedFrom":subQ1});Q6=makeQuery(id+"F0.imprint","IMPRINT",FACE,{"disambiguationData":[TD([[makeQuery(id+"F0.imprint","IMPRINT",EDGE,{"disambiguationData":[TD([[subQ5,1.0]])],"derivedFrom":subQ1}),-1.0]])]});}
            var Q7;
            {var subQ0=sQuery(id+"F0.wireOp",EDGE,"E12.5.0.3");Q7=makeQuery(id+"F0.imprint","IMPRINT",FACE,{"disambiguationData":[TD([[makeQuery(id+"F0.imprint","IMPRINT",EDGE,{"derivedFrom":subQ0}),1.0]])]});}
            var Q8;
            {var subQ1=sQuery(id+"F0.wireOp",EDGE,"E12.2.0.13");var subQ5=makeQuery(id+"F0.imprint","IMPRINT",VERTEX,{"derivedFrom":subQ1});Q8=makeQuery(id+"F0.imprint","IMPRINT",FACE,{"disambiguationData":[TD([[makeQuery(id+"F0.imprint","IMPRINT",EDGE,{"disambiguationData":[TD([[subQ5,1.0]])],"derivedFrom":subQ1}),-1.0]])]});}
            var Q9;
            {var subQ1=sQuery(id+"F0.wireOp",EDGE,"E12.1.0.13");var subQ5=makeQuery(id+"F0.imprint","IMPRINT",VERTEX,{"derivedFrom":subQ1});Q9=makeQuery(id+"F0.imprint","IMPRINT",FACE,{"disambiguationData":[TD([[makeQuery(id+"F0.imprint","IMPRINT",EDGE,{"disambiguationData":[TD([[subQ5,1.0]])],"derivedFrom":subQ1}),-1.0]])]});}
            var Q10;
            {var subQ1=sQuery(id+"F0.wireOp",EDGE,"E12.3.0.13");var subQ5=makeQuery(id+"F0.imprint","IMPRINT",VERTEX,{"derivedFrom":subQ1});Q10=makeQuery(id+"F0.imprint","IMPRINT",FACE,{"disambiguationData":[TD([[makeQuery(id+"F0.imprint","IMPRINT",EDGE,{"disambiguationData":[TD([[subQ5,1.0]])],"derivedFrom":subQ1}),-1.0]])]});}
            var Q11;
            {var subQ0=sQuery(id+"F0.wireOp",EDGE,"E6.left");Q11=makeQuery(id+"F0.imprint","IMPRINT",FACE,{"disambiguationData":[TD([[makeQuery(id+"F0.imprint","IMPRINT",EDGE,{"derivedFrom":subQ0}),-1.0]])]});}
            var Q12;
            {var subQ0=sQuery(id+"F0.wireOp",EDGE,"E12.2.0.51");Q12=makeQuery(id+"F0.imprint","IMPRINT",FACE,{"disambiguationData":[TD([[makeQuery(id+"F0.imprint","IMPRINT",EDGE,{"derivedFrom":subQ0}),-1.0]])]});}
            var Q13;
            {var subQ0=sQuery(id+"F0.wireOp",EDGE,"E12.1.0.48");Q13=makeQuery(id+"F0.imprint","IMPRINT",FACE,{"disambiguationData":[TD([[makeQuery(id+"F0.imprint","IMPRINT",EDGE,{"derivedFrom":subQ0}),-1.0]])]});}
            var Q14;
            {var subQ0=sQuery(id+"F0.wireOp",EDGE,"E12.1.0.51");Q14=makeQuery(id+"F0.imprint","IMPRINT",FACE,{"disambiguationData":[TD([[makeQuery(id+"F0.imprint","IMPRINT",EDGE,{"derivedFrom":subQ0}),-1.0]])]});}
            var Q15;
            {var subQ0=sQuery(id+"F0.wireOp",EDGE,"E12.3.0.48");Q15=makeQuery(id+"F0.imprint","IMPRINT",FACE,{"disambiguationData":[TD([[makeQuery(id+"F0.imprint","IMPRINT",EDGE,{"derivedFrom":subQ0}),-1.0]])]});}
            var Q16;
            {var subQ0=sQuery(id+"F0.wireOp",EDGE,"E12.3.0.51");Q16=makeQuery(id+"F0.imprint","IMPRINT",FACE,{"disambiguationData":[TD([[makeQuery(id+"F0.imprint","IMPRINT",EDGE,{"derivedFrom":subQ0}),-1.0]])]});}
            var Q17;
            {var subQ0=sQuery(id+"F0.wireOp",EDGE,"E12.2.0.48");Q17=makeQuery(id+"F0.imprint","IMPRINT",FACE,{"disambiguationData":[TD([[makeQuery(id+"F0.imprint","IMPRINT",EDGE,{"derivedFrom":subQ0}),-1.0]])]});}
            var Q18;
            {var subQ0=sQuery(id+"F0.wireOp",EDGE,"E12.4.0.48");Q18=makeQuery(id+"F0.imprint","IMPRINT",FACE,{"disambiguationData":[TD([[makeQuery(id+"F0.imprint","IMPRINT",EDGE,{"derivedFrom":subQ0}),-1.0]])]});}
            var Q19;
            {var subQ0=sQuery(id+"F0.wireOp",EDGE,"E12.4.0.51");Q19=makeQuery(id+"F0.imprint","IMPRINT",FACE,{"disambiguationData":[TD([[makeQuery(id+"F0.imprint","IMPRINT",EDGE,{"derivedFrom":subQ0}),-1.0]])]});}
            var Q20;
            {var subQ0=sQuery(id+"F0.wireOp",EDGE,"E12.6.0.51");Q20=makeQuery(id+"F0.imprint","IMPRINT",FACE,{"disambiguationData":[TD([[makeQuery(id+"F0.imprint","IMPRINT",EDGE,{"derivedFrom":subQ0}),-1.0]])]});}
            var Q21;
            {var subQ0=sQuery(id+"F0.wireOp",EDGE,"E12.5.0.48");Q21=makeQuery(id+"F0.imprint","IMPRINT",FACE,{"disambiguationData":[TD([[makeQuery(id+"F0.imprint","IMPRINT",EDGE,{"derivedFrom":subQ0}),-1.0]])]});}
            var Q22;
            {var subQ0=sQuery(id+"F0.wireOp",EDGE,"E12.5.0.51");Q22=makeQuery(id+"F0.imprint","IMPRINT",FACE,{"disambiguationData":[TD([[makeQuery(id+"F0.imprint","IMPRINT",EDGE,{"derivedFrom":subQ0}),-1.0]])]});}
            var Q23;
            {var subQ0=sQuery(id+"F0.wireOp",EDGE,"E12.7.0.48");Q23=makeQuery(id+"F0.imprint","IMPRINT",FACE,{"disambiguationData":[TD([[makeQuery(id+"F0.imprint","IMPRINT",EDGE,{"derivedFrom":subQ0}),-1.0]])]});}
            var Q24;
            {var subQ0=sQuery(id+"F0.wireOp",EDGE,"E12.7.0.51");Q24=makeQuery(id+"F0.imprint","IMPRINT",FACE,{"disambiguationData":[TD([[makeQuery(id+"F0.imprint","IMPRINT",EDGE,{"derivedFrom":subQ0}),-1.0]])]});}
            var Q25;
            {var subQ0=sQuery(id+"F0.wireOp",EDGE,"E12.6.0.48");Q25=makeQuery(id+"F0.imprint","IMPRINT",FACE,{"disambiguationData":[TD([[makeQuery(id+"F0.imprint","IMPRINT",EDGE,{"derivedFrom":subQ0}),-1.0]])]});}
            var Q26;
            {var subQ0=sQuery(id+"F0.wireOp",EDGE,"E12.3.0.3");Q26=makeQuery(id+"F0.imprint","IMPRINT",FACE,{"disambiguationData":[TD([[makeQuery(id+"F0.imprint","IMPRINT",EDGE,{"derivedFrom":subQ0}),1.0]])]});}
            var Q27;
            {var subQ0=sQuery(id+"F0.wireOp",EDGE,"E0.left");Q27=makeQuery(id+"F0.imprint","IMPRINT",FACE,{"disambiguationData":[TD([[makeQuery(id+"F0.imprint","IMPRINT",EDGE,{"derivedFrom":subQ0}),-1.0]])]});}
            var Q28;
            {var subQ0=sQuery(id+"F0.wireOp",EDGE,"E8.left");Q28=makeQuery(id+"F0.imprint","IMPRINT",FACE,{"disambiguationData":[TD([[makeQuery(id+"F0.imprint","IMPRINT",EDGE,{"derivedFrom":subQ0}),-1.0]])]});}
            var Q29;
            {var subQ0=sQuery(id+"F0.wireOp",EDGE,"E12.6.0.3");Q29=makeQuery(id+"F0.imprint","IMPRINT",FACE,{"disambiguationData":[TD([[makeQuery(id+"F0.imprint","IMPRINT",EDGE,{"derivedFrom":subQ0}),1.0]])]});}
            var Q30;
            {var subQ0=sQuery(id+"F0.wireOp",EDGE,"E12.2.0.59");Q30=makeQuery(id+"F0.imprint","IMPRINT",FACE,{"disambiguationData":[TD([[makeQuery(id+"F0.imprint","IMPRINT",EDGE,{"derivedFrom":subQ0}),-1.0]])]});}
            var Q31;
            {var subQ0=sQuery(id+"F0.wireOp",EDGE,"E12.1.0.59");Q31=makeQuery(id+"F0.imprint","IMPRINT",FACE,{"disambiguationData":[TD([[makeQuery(id+"F0.imprint","IMPRINT",EDGE,{"derivedFrom":subQ0}),-1.0]])]});}
            var Q32;
            {var subQ0=sQuery(id+"F0.wireOp",EDGE,"E12.3.0.59");Q32=makeQuery(id+"F0.imprint","IMPRINT",FACE,{"disambiguationData":[TD([[makeQuery(id+"F0.imprint","IMPRINT",EDGE,{"derivedFrom":subQ0}),-1.0]])]});}
            var Q33;
            {var subQ0=sQuery(id+"F0.wireOp",EDGE,"E12.4.0.59");Q33=makeQuery(id+"F0.imprint","IMPRINT",FACE,{"disambiguationData":[TD([[makeQuery(id+"F0.imprint","IMPRINT",EDGE,{"derivedFrom":subQ0}),-1.0]])]});}
            var Q34;
            {var subQ0=sQuery(id+"F0.wireOp",EDGE,"E12.6.0.59");Q34=makeQuery(id+"F0.imprint","IMPRINT",FACE,{"disambiguationData":[TD([[makeQuery(id+"F0.imprint","IMPRINT",EDGE,{"derivedFrom":subQ0}),-1.0]])]});}
            var Q35;
            {var subQ0=sQuery(id+"F0.wireOp",EDGE,"E12.5.0.59");Q35=makeQuery(id+"F0.imprint","IMPRINT",FACE,{"disambiguationData":[TD([[makeQuery(id+"F0.imprint","IMPRINT",EDGE,{"derivedFrom":subQ0}),-1.0]])]});}
            var Q36;
            {var subQ0=sQuery(id+"F0.wireOp",EDGE,"E12.7.0.59");Q36=makeQuery(id+"F0.imprint","IMPRINT",FACE,{"disambiguationData":[TD([[makeQuery(id+"F0.imprint","IMPRINT",EDGE,{"derivedFrom":subQ0}),-1.0]])]});}
            var Q37;
            {var subQ5=sQuery(id+"F0.wireOp",EDGE,"E4.bottom");var subQ6=makeQuery(id+"F0.imprint","IMPRINT",VERTEX,{"derivedFrom":subQ5});Q37=makeQuery(id+"F0.imprint","IMPRINT",FACE,{"disambiguationData":[TD([[makeQuery(id+"F0.imprint","IMPRINT",EDGE,{"disambiguationData":[TD([[subQ6,1.0]])],"derivedFrom":subQ5}),-1.0]])]});}
            var Q38;
            {var subQ0=sQuery(id+"F0.wireOp",EDGE,"E12.4.0.3");Q38=makeQuery(id+"F0.imprint","IMPRINT",FACE,{"disambiguationData":[TD([[makeQuery(id+"F0.imprint","IMPRINT",EDGE,{"derivedFrom":subQ0}),1.0]])]});}
            var Q39;
            {var subQ0=sQuery(id+"F0.wireOp",EDGE,"E12.7.0.58");Q39=makeQuery(id+"F0.imprint","IMPRINT",FACE,{"disambiguationData":[TD([[makeQuery(id+"F0.imprint","IMPRINT",EDGE,{"derivedFrom":subQ0}),-1.0]])]});}
            var Q40;
            {var subQ0=sQuery(id+"F0.wireOp",EDGE,"E4.left");Q40=makeQuery(id+"F0.imprint","IMPRINT",FACE,{"disambiguationData":[TD([[makeQuery(id+"F0.imprint","IMPRINT",EDGE,{"derivedFrom":subQ0}),-1.0]])]});}
            var Q41;
            {var subQ0=sQuery(id+"F0.wireOp",EDGE,"E12.7.0.3");Q41=makeQuery(id+"F0.imprint","IMPRINT",FACE,{"disambiguationData":[TD([[makeQuery(id+"F0.imprint","IMPRINT",EDGE,{"derivedFrom":subQ0}),1.0]])]});}
            var Q42;
            {var subQ0=sQuery(id+"F0.wireOp",EDGE,"E12.1.0.58");Q42=makeQuery(id+"F0.imprint","IMPRINT",FACE,{"disambiguationData":[TD([[makeQuery(id+"F0.imprint","IMPRINT",EDGE,{"derivedFrom":subQ0}),-1.0]])]});}
            var Q43;
            {var subQ0=sQuery(id+"F0.wireOp",EDGE,"E12.2.0.58");Q43=makeQuery(id+"F0.imprint","IMPRINT",FACE,{"disambiguationData":[TD([[makeQuery(id+"F0.imprint","IMPRINT",EDGE,{"derivedFrom":subQ0}),-1.0]])]});}
            var Q44;
            {var subQ0=sQuery(id+"F0.wireOp",EDGE,"E12.4.0.58");Q44=makeQuery(id+"F0.imprint","IMPRINT",FACE,{"disambiguationData":[TD([[makeQuery(id+"F0.imprint","IMPRINT",EDGE,{"derivedFrom":subQ0}),-1.0]])]});}
            var Q45;
            {var subQ0=sQuery(id+"F0.wireOp",EDGE,"E12.3.0.58");Q45=makeQuery(id+"F0.imprint","IMPRINT",FACE,{"disambiguationData":[TD([[makeQuery(id+"F0.imprint","IMPRINT",EDGE,{"derivedFrom":subQ0}),-1.0]])]});}
            var Q46;
            {var subQ0=sQuery(id+"F0.wireOp",EDGE,"E12.5.0.58");Q46=makeQuery(id+"F0.imprint","IMPRINT",FACE,{"disambiguationData":[TD([[makeQuery(id+"F0.imprint","IMPRINT",EDGE,{"derivedFrom":subQ0}),-1.0]])]});}
            var Q47;
            {var subQ0=sQuery(id+"F0.wireOp",EDGE,"E12.6.0.58");Q47=makeQuery(id+"F0.imprint","IMPRINT",FACE,{"disambiguationData":[TD([[makeQuery(id+"F0.imprint","IMPRINT",EDGE,{"derivedFrom":subQ0}),-1.0]])]});}
            var Q48;
            {var subQ5=sQuery(id+"F0.wireOp",EDGE,"E11.left");Q48=makeQuery(id+"F0.imprint","IMPRINT",FACE,{"disambiguationData":[TD([[makeQuery(id+"F0.imprint","IMPRINT",EDGE,{"derivedFrom":subQ5}),1.0]])]});}
            var Q49;
            {var subQ5=sQuery(id+"F0.wireOp",EDGE,"E12.1.0.45");Q49=makeQuery(id+"F0.imprint","IMPRINT",FACE,{"disambiguationData":[TD([[makeQuery(id+"F0.imprint","IMPRINT",EDGE,{"derivedFrom":subQ5}),1.0]])]});}
            var Q50;
            {var subQ5=sQuery(id+"F0.wireOp",EDGE,"E12.2.0.45");Q50=makeQuery(id+"F0.imprint","IMPRINT",FACE,{"disambiguationData":[TD([[makeQuery(id+"F0.imprint","IMPRINT",EDGE,{"derivedFrom":subQ5}),1.0]])]});}
            var Q51;
            {var subQ0=sQuery(id+"F0.wireOp",EDGE,"E7.top");var subQ1=sQuery(id+"F0.wireOp",EDGE,"E6.bottom");var subQ2=makeQuery(id+"F0.imprint","INTERSECT",VERTEX,{"derivedFrom":[subQ1,subQ0]});Q51=makeQuery(id+"F0.imprint","IMPRINT",FACE,{"disambiguationData":[TD([[makeQuery(id+"F0.imprint","IMPRINT",EDGE,{"disambiguationData":[TD([[subQ2,-1.0]])],"derivedFrom":subQ1}),1.0]])]});}
            var Q52;
            {var subQ0=sQuery(id+"F0.wireOp",EDGE,"E12.1.0.24");var subQ1=sQuery(id+"F0.wireOp",EDGE,"E12.1.0.13");var subQ2=makeQuery(id+"F0.imprint","INTERSECT",VERTEX,{"derivedFrom":[subQ1,subQ0]});Q52=makeQuery(id+"F0.imprint","IMPRINT",FACE,{"disambiguationData":[TD([[makeQuery(id+"F0.imprint","IMPRINT",EDGE,{"disambiguationData":[TD([[subQ2,-1.0]])],"derivedFrom":subQ1}),1.0]])]});}
            var Q53;
            {var subQ0=sQuery(id+"F0.wireOp",EDGE,"E12.3.0.24");var subQ1=sQuery(id+"F0.wireOp",EDGE,"E12.3.0.13");var subQ2=makeQuery(id+"F0.imprint","INTERSECT",VERTEX,{"derivedFrom":[subQ1,subQ0]});Q53=makeQuery(id+"F0.imprint","IMPRINT",FACE,{"disambiguationData":[TD([[makeQuery(id+"F0.imprint","IMPRINT",EDGE,{"disambiguationData":[TD([[subQ2,-1.0]])],"derivedFrom":subQ1}),1.0]])]});}
            var Q54;
            {var subQ0=sQuery(id+"F0.wireOp",EDGE,"E12.2.0.24");var subQ1=sQuery(id+"F0.wireOp",EDGE,"E12.2.0.13");var subQ2=makeQuery(id+"F0.imprint","INTERSECT",VERTEX,{"derivedFrom":[subQ1,subQ0]});Q54=makeQuery(id+"F0.imprint","IMPRINT",FACE,{"disambiguationData":[TD([[makeQuery(id+"F0.imprint","IMPRINT",EDGE,{"disambiguationData":[TD([[subQ2,-1.0]])],"derivedFrom":subQ1}),1.0]])]});}
            var Q55;
            {var subQ0=sQuery(id+"F0.wireOp",EDGE,"E12.4.0.24");var subQ1=sQuery(id+"F0.wireOp",EDGE,"E12.4.0.13");var subQ2=makeQuery(id+"F0.imprint","INTERSECT",VERTEX,{"derivedFrom":[subQ1,subQ0]});Q55=makeQuery(id+"F0.imprint","IMPRINT",FACE,{"disambiguationData":[TD([[makeQuery(id+"F0.imprint","IMPRINT",EDGE,{"disambiguationData":[TD([[subQ2,-1.0]])],"derivedFrom":subQ1}),1.0]])]});}
            var Q56;
            {var subQ0=sQuery(id+"F0.wireOp",EDGE,"E12.5.0.24");var subQ1=sQuery(id+"F0.wireOp",EDGE,"E12.5.0.13");var subQ2=makeQuery(id+"F0.imprint","INTERSECT",VERTEX,{"derivedFrom":[subQ1,subQ0]});Q56=makeQuery(id+"F0.imprint","IMPRINT",FACE,{"disambiguationData":[TD([[makeQuery(id+"F0.imprint","IMPRINT",EDGE,{"disambiguationData":[TD([[subQ2,-1.0]])],"derivedFrom":subQ1}),1.0]])]});}
            var Q57;
            {var subQ0=sQuery(id+"F0.wireOp",EDGE,"E12.7.0.24");var subQ1=sQuery(id+"F0.wireOp",EDGE,"E12.7.0.13");var subQ2=makeQuery(id+"F0.imprint","INTERSECT",VERTEX,{"derivedFrom":[subQ1,subQ0]});Q57=makeQuery(id+"F0.imprint","IMPRINT",FACE,{"disambiguationData":[TD([[makeQuery(id+"F0.imprint","IMPRINT",EDGE,{"disambiguationData":[TD([[subQ2,-1.0]])],"derivedFrom":subQ1}),1.0]])]});}
            var Q58;
            {var subQ0=sQuery(id+"F0.wireOp",EDGE,"E12.6.0.24");var subQ1=sQuery(id+"F0.wireOp",EDGE,"E12.6.0.13");var subQ2=makeQuery(id+"F0.imprint","INTERSECT",VERTEX,{"derivedFrom":[subQ1,subQ0]});Q58=makeQuery(id+"F0.imprint","IMPRINT",FACE,{"disambiguationData":[TD([[makeQuery(id+"F0.imprint","IMPRINT",EDGE,{"disambiguationData":[TD([[subQ2,-1.0]])],"derivedFrom":subQ1}),1.0]])]});}
            var Q59;
            {var subQ5=sQuery(id+"F0.wireOp",EDGE,"E12.5.0.45");Q59=makeQuery(id+"F0.imprint","IMPRINT",FACE,{"disambiguationData":[TD([[makeQuery(id+"F0.imprint","IMPRINT",EDGE,{"derivedFrom":subQ5}),1.0]])]});}
            var Q60;
            {var subQ0=sQuery(id+"F0.wireOp",EDGE,"E1.top");var subQ1=sQuery(id+"F0.wireOp",EDGE,"E0.bottom");var subQ2=makeQuery(id+"F0.imprint","INTERSECT",VERTEX,{"derivedFrom":[subQ1,subQ0]});Q60=makeQuery(id+"F0.imprint","IMPRINT",FACE,{"disambiguationData":[TD([[makeQuery(id+"F0.imprint","IMPRINT",EDGE,{"disambiguationData":[TD([[subQ2,-1.0]])],"derivedFrom":subQ1}),1.0]])]});}
            var Q61;
            {var subQ0=sQuery(id+"F0.wireOp",EDGE,"E12.2.0.27");var subQ1=sQuery(id+"F0.wireOp",EDGE,"E12.2.0.0");var subQ2=makeQuery(id+"F0.imprint","INTERSECT",VERTEX,{"derivedFrom":[subQ1,subQ0]});Q61=makeQuery(id+"F0.imprint","IMPRINT",FACE,{"disambiguationData":[TD([[makeQuery(id+"F0.imprint","IMPRINT",EDGE,{"disambiguationData":[TD([[subQ2,-1.0]])],"derivedFrom":subQ1}),1.0]])]});}
            var Q62;
            {var subQ0=sQuery(id+"F0.wireOp",EDGE,"E12.1.0.21");var subQ1=sQuery(id+"F0.wireOp",EDGE,"E12.1.0.16");var subQ2=makeQuery(id+"F0.imprint","INTERSECT",VERTEX,{"derivedFrom":[subQ1,subQ0]});Q62=makeQuery(id+"F0.imprint","IMPRINT",FACE,{"disambiguationData":[TD([[makeQuery(id+"F0.imprint","IMPRINT",EDGE,{"disambiguationData":[TD([[subQ2,-1.0]])],"derivedFrom":subQ1}),1.0]])]});}
            var Q63;
            {var subQ0=sQuery(id+"F0.wireOp",EDGE,"E12.1.0.27");var subQ1=sQuery(id+"F0.wireOp",EDGE,"E12.1.0.0");var subQ2=makeQuery(id+"F0.imprint","INTERSECT",VERTEX,{"derivedFrom":[subQ1,subQ0]});Q63=makeQuery(id+"F0.imprint","IMPRINT",FACE,{"disambiguationData":[TD([[makeQuery(id+"F0.imprint","IMPRINT",EDGE,{"disambiguationData":[TD([[subQ2,-1.0]])],"derivedFrom":subQ1}),1.0]])]});}
            var Q64;
            {var subQ0=sQuery(id+"F0.wireOp",EDGE,"E12.3.0.21");var subQ1=sQuery(id+"F0.wireOp",EDGE,"E12.3.0.16");var subQ2=makeQuery(id+"F0.imprint","INTERSECT",VERTEX,{"derivedFrom":[subQ1,subQ0]});Q64=makeQuery(id+"F0.imprint","IMPRINT",FACE,{"disambiguationData":[TD([[makeQuery(id+"F0.imprint","IMPRINT",EDGE,{"disambiguationData":[TD([[subQ2,-1.0]])],"derivedFrom":subQ1}),1.0]])]});}
            var Q65;
            {var subQ0=sQuery(id+"F0.wireOp",EDGE,"E12.3.0.27");var subQ1=sQuery(id+"F0.wireOp",EDGE,"E12.3.0.0");var subQ2=makeQuery(id+"F0.imprint","INTERSECT",VERTEX,{"derivedFrom":[subQ1,subQ0]});Q65=makeQuery(id+"F0.imprint","IMPRINT",FACE,{"disambiguationData":[TD([[makeQuery(id+"F0.imprint","IMPRINT",EDGE,{"disambiguationData":[TD([[subQ2,-1.0]])],"derivedFrom":subQ1}),1.0]])]});}
            var Q66;
            {var subQ0=sQuery(id+"F0.wireOp",EDGE,"E12.2.0.21");var subQ1=sQuery(id+"F0.wireOp",EDGE,"E12.2.0.16");var subQ2=makeQuery(id+"F0.imprint","INTERSECT",VERTEX,{"derivedFrom":[subQ1,subQ0]});Q66=makeQuery(id+"F0.imprint","IMPRINT",FACE,{"disambiguationData":[TD([[makeQuery(id+"F0.imprint","IMPRINT",EDGE,{"disambiguationData":[TD([[subQ2,-1.0]])],"derivedFrom":subQ1}),1.0]])]});}
            var Q67;
            {var subQ0=sQuery(id+"F0.wireOp",EDGE,"E12.4.0.21");var subQ1=sQuery(id+"F0.wireOp",EDGE,"E12.4.0.16");var subQ2=makeQuery(id+"F0.imprint","INTERSECT",VERTEX,{"derivedFrom":[subQ1,subQ0]});Q67=makeQuery(id+"F0.imprint","IMPRINT",FACE,{"disambiguationData":[TD([[makeQuery(id+"F0.imprint","IMPRINT",EDGE,{"disambiguationData":[TD([[subQ2,-1.0]])],"derivedFrom":subQ1}),1.0]])]});}
            var Q68;
            {var subQ0=sQuery(id+"F0.wireOp",EDGE,"E12.4.0.27");var subQ1=sQuery(id+"F0.wireOp",EDGE,"E12.4.0.0");var subQ2=makeQuery(id+"F0.imprint","INTERSECT",VERTEX,{"derivedFrom":[subQ1,subQ0]});Q68=makeQuery(id+"F0.imprint","IMPRINT",FACE,{"disambiguationData":[TD([[makeQuery(id+"F0.imprint","IMPRINT",EDGE,{"disambiguationData":[TD([[subQ2,-1.0]])],"derivedFrom":subQ1}),1.0]])]});}
            var Q69;
            {var subQ0=sQuery(id+"F0.wireOp",EDGE,"E12.6.0.27");var subQ1=sQuery(id+"F0.wireOp",EDGE,"E12.6.0.0");var subQ2=makeQuery(id+"F0.imprint","INTERSECT",VERTEX,{"derivedFrom":[subQ1,subQ0]});Q69=makeQuery(id+"F0.imprint","IMPRINT",FACE,{"disambiguationData":[TD([[makeQuery(id+"F0.imprint","IMPRINT",EDGE,{"disambiguationData":[TD([[subQ2,-1.0]])],"derivedFrom":subQ1}),1.0]])]});}
            var Q70;
            {var subQ0=sQuery(id+"F0.wireOp",EDGE,"E12.5.0.21");var subQ1=sQuery(id+"F0.wireOp",EDGE,"E12.5.0.16");var subQ2=makeQuery(id+"F0.imprint","INTERSECT",VERTEX,{"derivedFrom":[subQ1,subQ0]});Q70=makeQuery(id+"F0.imprint","IMPRINT",FACE,{"disambiguationData":[TD([[makeQuery(id+"F0.imprint","IMPRINT",EDGE,{"disambiguationData":[TD([[subQ2,-1.0]])],"derivedFrom":subQ1}),1.0]])]});}
            var Q71;
            {var subQ0=sQuery(id+"F0.wireOp",EDGE,"E12.5.0.27");var subQ1=sQuery(id+"F0.wireOp",EDGE,"E12.5.0.0");var subQ2=makeQuery(id+"F0.imprint","INTERSECT",VERTEX,{"derivedFrom":[subQ1,subQ0]});Q71=makeQuery(id+"F0.imprint","IMPRINT",FACE,{"disambiguationData":[TD([[makeQuery(id+"F0.imprint","IMPRINT",EDGE,{"disambiguationData":[TD([[subQ2,-1.0]])],"derivedFrom":subQ1}),1.0]])]});}
            var Q72;
            {var subQ0=sQuery(id+"F0.wireOp",EDGE,"E12.7.0.21");var subQ1=sQuery(id+"F0.wireOp",EDGE,"E12.7.0.16");var subQ2=makeQuery(id+"F0.imprint","INTERSECT",VERTEX,{"derivedFrom":[subQ1,subQ0]});Q72=makeQuery(id+"F0.imprint","IMPRINT",FACE,{"disambiguationData":[TD([[makeQuery(id+"F0.imprint","IMPRINT",EDGE,{"disambiguationData":[TD([[subQ2,-1.0]])],"derivedFrom":subQ1}),1.0]])]});}
            var Q73;
            {var subQ0=sQuery(id+"F0.wireOp",EDGE,"E12.7.0.27");var subQ1=sQuery(id+"F0.wireOp",EDGE,"E12.7.0.0");var subQ2=makeQuery(id+"F0.imprint","INTERSECT",VERTEX,{"derivedFrom":[subQ1,subQ0]});Q73=makeQuery(id+"F0.imprint","IMPRINT",FACE,{"disambiguationData":[TD([[makeQuery(id+"F0.imprint","IMPRINT",EDGE,{"disambiguationData":[TD([[subQ2,-1.0]])],"derivedFrom":subQ1}),1.0]])]});}
            var Q74;
            {var subQ0=sQuery(id+"F0.wireOp",EDGE,"E12.6.0.21");var subQ1=sQuery(id+"F0.wireOp",EDGE,"E12.6.0.16");var subQ2=makeQuery(id+"F0.imprint","INTERSECT",VERTEX,{"derivedFrom":[subQ1,subQ0]});Q74=makeQuery(id+"F0.imprint","IMPRINT",FACE,{"disambiguationData":[TD([[makeQuery(id+"F0.imprint","IMPRINT",EDGE,{"disambiguationData":[TD([[subQ2,-1.0]])],"derivedFrom":subQ1}),1.0]])]});}
            var Q75;
            {var subQ5=sQuery(id+"F0.wireOp",EDGE,"E12.1.0.37");Q75=makeQuery(id+"F0.imprint","IMPRINT",FACE,{"disambiguationData":[TD([[makeQuery(id+"F0.imprint","IMPRINT",EDGE,{"derivedFrom":subQ5}),-1.0]])]});}
            var Q76;
            {var subQ5=sQuery(id+"F0.wireOp",EDGE,"E12.3.0.37");Q76=makeQuery(id+"F0.imprint","IMPRINT",FACE,{"disambiguationData":[TD([[makeQuery(id+"F0.imprint","IMPRINT",EDGE,{"derivedFrom":subQ5}),-1.0]])]});}
            var Q77;
            {var subQ5=sQuery(id+"F0.wireOp",EDGE,"E12.2.0.37");Q77=makeQuery(id+"F0.imprint","IMPRINT",FACE,{"disambiguationData":[TD([[makeQuery(id+"F0.imprint","IMPRINT",EDGE,{"derivedFrom":subQ5}),-1.0]])]});}
            var Q78;
            {var subQ5=sQuery(id+"F0.wireOp",EDGE,"E12.4.0.37");Q78=makeQuery(id+"F0.imprint","IMPRINT",FACE,{"disambiguationData":[TD([[makeQuery(id+"F0.imprint","IMPRINT",EDGE,{"derivedFrom":subQ5}),-1.0]])]});}
            var Q79;
            {var subQ5=sQuery(id+"F0.wireOp",EDGE,"E12.5.0.37");Q79=makeQuery(id+"F0.imprint","IMPRINT",FACE,{"disambiguationData":[TD([[makeQuery(id+"F0.imprint","IMPRINT",EDGE,{"derivedFrom":subQ5}),-1.0]])]});}
            var Q80;
            {var subQ5=sQuery(id+"F0.wireOp",EDGE,"E12.7.0.37");Q80=makeQuery(id+"F0.imprint","IMPRINT",FACE,{"disambiguationData":[TD([[makeQuery(id+"F0.imprint","IMPRINT",EDGE,{"derivedFrom":subQ5}),-1.0]])]});}
            var Q81;
            {var subQ5=sQuery(id+"F0.wireOp",EDGE,"E12.6.0.37");Q81=makeQuery(id+"F0.imprint","IMPRINT",FACE,{"disambiguationData":[TD([[makeQuery(id+"F0.imprint","IMPRINT",EDGE,{"derivedFrom":subQ5}),-1.0]])]});}
            var Q82;
            {var subQ5=sQuery(id+"F0.wireOp",EDGE,"E12.3.0.45");Q82=makeQuery(id+"F0.imprint","IMPRINT",FACE,{"disambiguationData":[TD([[makeQuery(id+"F0.imprint","IMPRINT",EDGE,{"derivedFrom":subQ5}),1.0]])]});}
            var Q83;
            {var subQ0=sQuery(id+"F0.wireOp",EDGE,"E9.top");var subQ1=sQuery(id+"F0.wireOp",EDGE,"E8.bottom");var subQ2=makeQuery(id+"F0.imprint","INTERSECT",VERTEX,{"derivedFrom":[subQ1,subQ0]});Q83=makeQuery(id+"F0.imprint","IMPRINT",FACE,{"disambiguationData":[TD([[makeQuery(id+"F0.imprint","IMPRINT",EDGE,{"disambiguationData":[TD([[subQ2,-1.0]])],"derivedFrom":subQ1}),1.0]])]});}
            var Q84;
            {var subQ5=sQuery(id+"F0.wireOp",EDGE,"E12.6.0.45");Q84=makeQuery(id+"F0.imprint","IMPRINT",FACE,{"disambiguationData":[TD([[makeQuery(id+"F0.imprint","IMPRINT",EDGE,{"derivedFrom":subQ5}),1.0]])]});}
            var Q85;
            {var subQ0=sQuery(id+"F0.wireOp",EDGE,"E3.top");var subQ1=sQuery(id+"F0.wireOp",EDGE,"E2.bottom");var subQ2=makeQuery(id+"F0.imprint","INTERSECT",VERTEX,{"derivedFrom":[subQ1,subQ0]});Q85=makeQuery(id+"F0.imprint","IMPRINT",FACE,{"disambiguationData":[TD([[makeQuery(id+"F0.imprint","IMPRINT",EDGE,{"disambiguationData":[TD([[subQ2,-1.0]])],"derivedFrom":subQ1}),1.0]])]});}
            var Q86;
            {var subQ0=sQuery(id+"F0.wireOp",EDGE,"E12.2.0.32");var subQ1=sQuery(id+"F0.wireOp",EDGE,"E12.2.0.5");var subQ2=makeQuery(id+"F0.imprint","INTERSECT",VERTEX,{"derivedFrom":[subQ1,subQ0]});Q86=makeQuery(id+"F0.imprint","IMPRINT",FACE,{"disambiguationData":[TD([[makeQuery(id+"F0.imprint","IMPRINT",EDGE,{"disambiguationData":[TD([[subQ2,-1.0]])],"derivedFrom":subQ1}),1.0]])]});}
            var Q87;
            {var subQ0=sQuery(id+"F0.wireOp",EDGE,"E12.4.0.32");var subQ1=sQuery(id+"F0.wireOp",EDGE,"E12.4.0.5");var subQ2=makeQuery(id+"F0.imprint","INTERSECT",VERTEX,{"derivedFrom":[subQ1,subQ0]});Q87=makeQuery(id+"F0.imprint","IMPRINT",FACE,{"disambiguationData":[TD([[makeQuery(id+"F0.imprint","IMPRINT",EDGE,{"disambiguationData":[TD([[subQ2,-1.0]])],"derivedFrom":subQ1}),1.0]])]});}
            var Q88;
            {var subQ0=sQuery(id+"F0.wireOp",EDGE,"E12.3.0.32");var subQ1=sQuery(id+"F0.wireOp",EDGE,"E12.3.0.5");var subQ2=makeQuery(id+"F0.imprint","INTERSECT",VERTEX,{"derivedFrom":[subQ1,subQ0]});Q88=makeQuery(id+"F0.imprint","IMPRINT",FACE,{"disambiguationData":[TD([[makeQuery(id+"F0.imprint","IMPRINT",EDGE,{"disambiguationData":[TD([[subQ2,-1.0]])],"derivedFrom":subQ1}),1.0]])]});}
            var Q89;
            {var subQ0=sQuery(id+"F0.wireOp",EDGE,"E12.5.0.32");var subQ1=sQuery(id+"F0.wireOp",EDGE,"E12.5.0.5");var subQ2=makeQuery(id+"F0.imprint","INTERSECT",VERTEX,{"derivedFrom":[subQ1,subQ0]});Q89=makeQuery(id+"F0.imprint","IMPRINT",FACE,{"disambiguationData":[TD([[makeQuery(id+"F0.imprint","IMPRINT",EDGE,{"disambiguationData":[TD([[subQ2,-1.0]])],"derivedFrom":subQ1}),1.0]])]});}
            var Q90;
            {var subQ0=sQuery(id+"F0.wireOp",EDGE,"E12.6.0.32");var subQ1=sQuery(id+"F0.wireOp",EDGE,"E12.6.0.5");var subQ2=makeQuery(id+"F0.imprint","INTERSECT",VERTEX,{"derivedFrom":[subQ1,subQ0]});Q90=makeQuery(id+"F0.imprint","IMPRINT",FACE,{"disambiguationData":[TD([[makeQuery(id+"F0.imprint","IMPRINT",EDGE,{"disambiguationData":[TD([[subQ2,-1.0]])],"derivedFrom":subQ1}),1.0]])]});}
            var Q91;
            {var subQ0=sQuery(id+"F0.wireOp",EDGE,"E12.7.0.32");var subQ1=sQuery(id+"F0.wireOp",EDGE,"E12.7.0.5");var subQ2=makeQuery(id+"F0.imprint","INTERSECT",VERTEX,{"derivedFrom":[subQ1,subQ0]});Q91=makeQuery(id+"F0.imprint","IMPRINT",FACE,{"disambiguationData":[TD([[makeQuery(id+"F0.imprint","IMPRINT",EDGE,{"disambiguationData":[TD([[subQ2,-1.0]])],"derivedFrom":subQ1}),1.0]])]});}
            var Q92;
            {var subQ0=sQuery(id+"F0.wireOp",EDGE,"E12.1.0.32");var subQ1=sQuery(id+"F0.wireOp",EDGE,"E12.1.0.5");var subQ2=makeQuery(id+"F0.imprint","INTERSECT",VERTEX,{"derivedFrom":[subQ1,subQ0]});Q92=makeQuery(id+"F0.imprint","IMPRINT",FACE,{"disambiguationData":[TD([[makeQuery(id+"F0.imprint","IMPRINT",EDGE,{"disambiguationData":[TD([[subQ2,-1.0]])],"derivedFrom":subQ1}),1.0]])]});}
            var Q93;
            {var subQ0=sQuery(id+"F0.wireOp",EDGE,"E5.top");var subQ1=sQuery(id+"F0.wireOp",EDGE,"E4.bottom");var subQ2=makeQuery(id+"F0.imprint","INTERSECT",VERTEX,{"derivedFrom":[subQ1,subQ0]});Q93=makeQuery(id+"F0.imprint","IMPRINT",FACE,{"disambiguationData":[TD([[makeQuery(id+"F0.imprint","IMPRINT",EDGE,{"disambiguationData":[TD([[subQ2,-1.0]])],"derivedFrom":subQ1}),1.0]])]});}
            var Q94;
            {var subQ5=sQuery(id+"F0.wireOp",EDGE,"E12.4.0.45");Q94=makeQuery(id+"F0.imprint","IMPRINT",FACE,{"disambiguationData":[TD([[makeQuery(id+"F0.imprint","IMPRINT",EDGE,{"derivedFrom":subQ5}),1.0]])]});}
            var Q95;
            {var subQ0=sQuery(id+"F0.wireOp",EDGE,"E12.5.0.23");var subQ1=sQuery(id+"F0.wireOp",EDGE,"E12.5.0.10");var subQ2=makeQuery(id+"F0.imprint","INTERSECT",VERTEX,{"derivedFrom":[subQ1,subQ0]});Q95=makeQuery(id+"F0.imprint","IMPRINT",FACE,{"disambiguationData":[TD([[makeQuery(id+"F0.imprint","IMPRINT",EDGE,{"disambiguationData":[TD([[subQ2,-1.0]])],"derivedFrom":subQ1}),1.0]])]});}
            var Q96;
            {var subQ0=sQuery(id+"F0.wireOp",EDGE,"E12.6.0.23");var subQ1=sQuery(id+"F0.wireOp",EDGE,"E12.6.0.10");var subQ2=makeQuery(id+"F0.imprint","INTERSECT",VERTEX,{"derivedFrom":[subQ1,subQ0]});Q96=makeQuery(id+"F0.imprint","IMPRINT",FACE,{"disambiguationData":[TD([[makeQuery(id+"F0.imprint","IMPRINT",EDGE,{"disambiguationData":[TD([[subQ2,-1.0]])],"derivedFrom":subQ1}),1.0]])]});}
            var Q97;
            {var subQ0=sQuery(id+"F0.wireOp",EDGE,"E12.7.0.23");var subQ1=sQuery(id+"F0.wireOp",EDGE,"E12.7.0.10");var subQ2=makeQuery(id+"F0.imprint","INTERSECT",VERTEX,{"derivedFrom":[subQ1,subQ0]});Q97=makeQuery(id+"F0.imprint","IMPRINT",FACE,{"disambiguationData":[TD([[makeQuery(id+"F0.imprint","IMPRINT",EDGE,{"disambiguationData":[TD([[subQ2,-1.0]])],"derivedFrom":subQ1}),1.0]])]});}
            var Q98;
            {var subQ0=sQuery(id+"F0.wireOp",EDGE,"E12.1.0.23");var subQ1=sQuery(id+"F0.wireOp",EDGE,"E12.1.0.10");var subQ2=makeQuery(id+"F0.imprint","INTERSECT",VERTEX,{"derivedFrom":[subQ1,subQ0]});Q98=makeQuery(id+"F0.imprint","IMPRINT",FACE,{"disambiguationData":[TD([[makeQuery(id+"F0.imprint","IMPRINT",EDGE,{"disambiguationData":[TD([[subQ2,-1.0]])],"derivedFrom":subQ1}),1.0]])]});}
            var Q99;
            {var subQ0=sQuery(id+"F0.wireOp",EDGE,"E12.2.0.23");var subQ1=sQuery(id+"F0.wireOp",EDGE,"E12.2.0.10");var subQ2=makeQuery(id+"F0.imprint","INTERSECT",VERTEX,{"derivedFrom":[subQ1,subQ0]});Q99=makeQuery(id+"F0.imprint","IMPRINT",FACE,{"disambiguationData":[TD([[makeQuery(id+"F0.imprint","IMPRINT",EDGE,{"disambiguationData":[TD([[subQ2,-1.0]])],"derivedFrom":subQ1}),1.0]])]});}
            var Q100;
            {var subQ0=sQuery(id+"F0.wireOp",EDGE,"E12.4.0.23");var subQ1=sQuery(id+"F0.wireOp",EDGE,"E12.4.0.10");var subQ2=makeQuery(id+"F0.imprint","INTERSECT",VERTEX,{"derivedFrom":[subQ1,subQ0]});Q100=makeQuery(id+"F0.imprint","IMPRINT",FACE,{"disambiguationData":[TD([[makeQuery(id+"F0.imprint","IMPRINT",EDGE,{"disambiguationData":[TD([[subQ2,-1.0]])],"derivedFrom":subQ1}),1.0]])]});}
            var Q101;
            {var subQ0=sQuery(id+"F0.wireOp",EDGE,"E12.3.0.23");var subQ1=sQuery(id+"F0.wireOp",EDGE,"E12.3.0.10");var subQ2=makeQuery(id+"F0.imprint","INTERSECT",VERTEX,{"derivedFrom":[subQ1,subQ0]});Q101=makeQuery(id+"F0.imprint","IMPRINT",FACE,{"disambiguationData":[TD([[makeQuery(id+"F0.imprint","IMPRINT",EDGE,{"disambiguationData":[TD([[subQ2,-1.0]])],"derivedFrom":subQ1}),1.0]])]});}
            var Q102;
            {var subQ5=sQuery(id+"F0.wireOp",EDGE,"E12.7.0.45");Q102=makeQuery(id+"F0.imprint","IMPRINT",FACE,{"disambiguationData":[TD([[makeQuery(id+"F0.imprint","IMPRINT",EDGE,{"derivedFrom":subQ5}),1.0]])]});}
            var Q103;
            {var subQ0=sQuery(id+"F0.wireOp",EDGE,"E6.left");Q103=makeQuery(id+"F0.imprint","IMPRINT",FACE,{"disambiguationData":[TD([[makeQuery(id+"F0.imprint","IMPRINT",EDGE,{"derivedFrom":subQ0}),1.0]])]});}
            var Q104;
            {var subQ5=sQuery(id+"F0.wireOp",EDGE,"E7.right");Q104=makeQuery(id+"F0.imprint","IMPRINT",FACE,{"disambiguationData":[TD([[makeQuery(id+"F0.imprint","IMPRINT",EDGE,{"derivedFrom":subQ5}),-1.0]])]});}
            var Q105;
            {var subQ5=sQuery(id+"F0.wireOp",EDGE,"E12.1.0.40");Q105=makeQuery(id+"F0.imprint","IMPRINT",FACE,{"disambiguationData":[TD([[makeQuery(id+"F0.imprint","IMPRINT",EDGE,{"derivedFrom":subQ5}),-1.0]])]});}
            var Q106;
            {var subQ5=sQuery(id+"F0.wireOp",EDGE,"E12.3.0.40");Q106=makeQuery(id+"F0.imprint","IMPRINT",FACE,{"disambiguationData":[TD([[makeQuery(id+"F0.imprint","IMPRINT",EDGE,{"derivedFrom":subQ5}),-1.0]])]});}
            var Q107;
            {var subQ5=sQuery(id+"F0.wireOp",EDGE,"E12.2.0.40");Q107=makeQuery(id+"F0.imprint","IMPRINT",FACE,{"disambiguationData":[TD([[makeQuery(id+"F0.imprint","IMPRINT",EDGE,{"derivedFrom":subQ5}),-1.0]])]});}
            var Q108;
            {var subQ5=sQuery(id+"F0.wireOp",EDGE,"E12.4.0.40");Q108=makeQuery(id+"F0.imprint","IMPRINT",FACE,{"disambiguationData":[TD([[makeQuery(id+"F0.imprint","IMPRINT",EDGE,{"derivedFrom":subQ5}),-1.0]])]});}
            var Q109;
            {var subQ5=sQuery(id+"F0.wireOp",EDGE,"E12.5.0.40");Q109=makeQuery(id+"F0.imprint","IMPRINT",FACE,{"disambiguationData":[TD([[makeQuery(id+"F0.imprint","IMPRINT",EDGE,{"derivedFrom":subQ5}),-1.0]])]});}
            var Q110;
            {var subQ5=sQuery(id+"F0.wireOp",EDGE,"E12.7.0.40");Q110=makeQuery(id+"F0.imprint","IMPRINT",FACE,{"disambiguationData":[TD([[makeQuery(id+"F0.imprint","IMPRINT",EDGE,{"derivedFrom":subQ5}),-1.0]])]});}
            var Q111;
            {var subQ5=sQuery(id+"F0.wireOp",EDGE,"E12.6.0.40");Q111=makeQuery(id+"F0.imprint","IMPRINT",FACE,{"disambiguationData":[TD([[makeQuery(id+"F0.imprint","IMPRINT",EDGE,{"derivedFrom":subQ5}),-1.0]])]});}
            var Q112;
            {var subQ5=sQuery(id+"F0.wireOp",EDGE,"E4.right");Q112=makeQuery(id+"F0.imprint","IMPRINT",FACE,{"disambiguationData":[TD([[makeQuery(id+"F0.imprint","IMPRINT",EDGE,{"derivedFrom":subQ5}),-1.0]])]});}
            var Q113;
            {var subQ5=sQuery(id+"F0.wireOp",EDGE,"E8.right");Q113=makeQuery(id+"F0.imprint","IMPRINT",FACE,{"disambiguationData":[TD([[makeQuery(id+"F0.imprint","IMPRINT",EDGE,{"derivedFrom":subQ5}),-1.0]])]});}
            var Q114;
            {var subQ5=sQuery(id+"F0.wireOp",EDGE,"E1.right");Q114=makeQuery(id+"F0.imprint","IMPRINT",FACE,{"disambiguationData":[TD([[makeQuery(id+"F0.imprint","IMPRINT",EDGE,{"derivedFrom":subQ5}),-1.0]])]});}
            var Q115;
            {var subQ5=sQuery(id+"F0.wireOp",EDGE,"E12.2.0.38");Q115=makeQuery(id+"F0.imprint","IMPRINT",FACE,{"disambiguationData":[TD([[makeQuery(id+"F0.imprint","IMPRINT",EDGE,{"derivedFrom":subQ5}),-1.0]])]});}
            var Q116;
            {var subQ5=sQuery(id+"F0.wireOp",EDGE,"E12.1.0.38");Q116=makeQuery(id+"F0.imprint","IMPRINT",FACE,{"disambiguationData":[TD([[makeQuery(id+"F0.imprint","IMPRINT",EDGE,{"derivedFrom":subQ5}),-1.0]])]});}
            var Q117;
            {var subQ5=sQuery(id+"F0.wireOp",EDGE,"E12.3.0.38");Q117=makeQuery(id+"F0.imprint","IMPRINT",FACE,{"disambiguationData":[TD([[makeQuery(id+"F0.imprint","IMPRINT",EDGE,{"derivedFrom":subQ5}),-1.0]])]});}
            var Q118;
            {var subQ5=sQuery(id+"F0.wireOp",EDGE,"E12.4.0.38");Q118=makeQuery(id+"F0.imprint","IMPRINT",FACE,{"disambiguationData":[TD([[makeQuery(id+"F0.imprint","IMPRINT",EDGE,{"derivedFrom":subQ5}),-1.0]])]});}
            var Q119;
            {var subQ5=sQuery(id+"F0.wireOp",EDGE,"E12.6.0.38");Q119=makeQuery(id+"F0.imprint","IMPRINT",FACE,{"disambiguationData":[TD([[makeQuery(id+"F0.imprint","IMPRINT",EDGE,{"derivedFrom":subQ5}),-1.0]])]});}
            var Q120;
            {var subQ5=sQuery(id+"F0.wireOp",EDGE,"E12.5.0.38");Q120=makeQuery(id+"F0.imprint","IMPRINT",FACE,{"disambiguationData":[TD([[makeQuery(id+"F0.imprint","IMPRINT",EDGE,{"derivedFrom":subQ5}),-1.0]])]});}
            var Q121;
            {var subQ5=sQuery(id+"F0.wireOp",EDGE,"E12.7.0.38");Q121=makeQuery(id+"F0.imprint","IMPRINT",FACE,{"disambiguationData":[TD([[makeQuery(id+"F0.imprint","IMPRINT",EDGE,{"derivedFrom":subQ5}),-1.0]])]});}
            var Q122;
            {var subQ0=sQuery(id+"F0.wireOp",EDGE,"E0.left");Q122=makeQuery(id+"F0.imprint","IMPRINT",FACE,{"disambiguationData":[TD([[makeQuery(id+"F0.imprint","IMPRINT",EDGE,{"derivedFrom":subQ0}),1.0]])]});}
            var Q123;
            {var subQ0=sQuery(id+"F0.wireOp",EDGE,"E12.1.0.43");Q123=makeQuery(id+"F0.imprint","IMPRINT",FACE,{"disambiguationData":[TD([[makeQuery(id+"F0.imprint","IMPRINT",EDGE,{"derivedFrom":subQ0}),-1.0]])]});}
            var Q124;
            {var subQ5=sQuery(id+"F0.wireOp",EDGE,"E9.right");Q124=makeQuery(id+"F0.imprint","IMPRINT",FACE,{"disambiguationData":[TD([[makeQuery(id+"F0.imprint","IMPRINT",EDGE,{"derivedFrom":subQ5}),-1.0]])]});}
            var Q125;
            {var subQ3=sQuery(id+"F0.wireOp",EDGE,"E12.1.0.48");Q125=makeQuery(id+"F0.imprint","IMPRINT",FACE,{"disambiguationData":[TD([[makeQuery(id+"F0.imprint","IMPRINT",EDGE,{"derivedFrom":subQ3}),1.0]])]});}
            var Q126;
            {var subQ3=sQuery(id+"F0.wireOp",EDGE,"E12.1.0.51");Q126=makeQuery(id+"F0.imprint","IMPRINT",FACE,{"disambiguationData":[TD([[makeQuery(id+"F0.imprint","IMPRINT",EDGE,{"derivedFrom":subQ3}),1.0]])]});}
            var Q127;
            {var subQ0=sQuery(id+"F0.wireOp",EDGE,"E8.left");Q127=makeQuery(id+"F0.imprint","IMPRINT",FACE,{"disambiguationData":[TD([[makeQuery(id+"F0.imprint","IMPRINT",EDGE,{"derivedFrom":subQ0}),1.0]])]});}
            var Q128;
            {var subQ5=sQuery(id+"F0.wireOp",EDGE,"E12.2.0.39");Q128=makeQuery(id+"F0.imprint","IMPRINT",FACE,{"disambiguationData":[TD([[makeQuery(id+"F0.imprint","IMPRINT",EDGE,{"derivedFrom":subQ5}),-1.0]])]});}
            var Q129;
            {var subQ4=sQuery(id+"F0.wireOp",EDGE,"E12.1.0.52");Q129=makeQuery(id+"F0.imprint","IMPRINT",FACE,{"disambiguationData":[TD([[makeQuery(id+"F0.imprint","IMPRINT",EDGE,{"derivedFrom":subQ4}),1.0]])]});}
            var Q130;
            {var subQ5=sQuery(id+"F0.wireOp",EDGE,"E12.1.0.39");Q130=makeQuery(id+"F0.imprint","IMPRINT",FACE,{"disambiguationData":[TD([[makeQuery(id+"F0.imprint","IMPRINT",EDGE,{"derivedFrom":subQ5}),-1.0]])]});}
            var Q131;
            {var subQ4=sQuery(id+"F0.wireOp",EDGE,"E12.3.0.52");Q131=makeQuery(id+"F0.imprint","IMPRINT",FACE,{"disambiguationData":[TD([[makeQuery(id+"F0.imprint","IMPRINT",EDGE,{"derivedFrom":subQ4}),1.0]])]});}
            var Q132;
            {var subQ5=sQuery(id+"F0.wireOp",EDGE,"E12.3.0.39");Q132=makeQuery(id+"F0.imprint","IMPRINT",FACE,{"disambiguationData":[TD([[makeQuery(id+"F0.imprint","IMPRINT",EDGE,{"derivedFrom":subQ5}),-1.0]])]});}
            var Q133;
            {var subQ4=sQuery(id+"F0.wireOp",EDGE,"E12.2.0.52");Q133=makeQuery(id+"F0.imprint","IMPRINT",FACE,{"disambiguationData":[TD([[makeQuery(id+"F0.imprint","IMPRINT",EDGE,{"derivedFrom":subQ4}),1.0]])]});}
            var Q134;
            {var subQ4=sQuery(id+"F0.wireOp",EDGE,"E12.4.0.52");Q134=makeQuery(id+"F0.imprint","IMPRINT",FACE,{"disambiguationData":[TD([[makeQuery(id+"F0.imprint","IMPRINT",EDGE,{"derivedFrom":subQ4}),1.0]])]});}
            var Q135;
            {var subQ5=sQuery(id+"F0.wireOp",EDGE,"E12.4.0.39");Q135=makeQuery(id+"F0.imprint","IMPRINT",FACE,{"disambiguationData":[TD([[makeQuery(id+"F0.imprint","IMPRINT",EDGE,{"derivedFrom":subQ5}),-1.0]])]});}
            var Q136;
            {var subQ5=sQuery(id+"F0.wireOp",EDGE,"E12.6.0.39");Q136=makeQuery(id+"F0.imprint","IMPRINT",FACE,{"disambiguationData":[TD([[makeQuery(id+"F0.imprint","IMPRINT",EDGE,{"derivedFrom":subQ5}),-1.0]])]});}
            var Q137;
            {var subQ4=sQuery(id+"F0.wireOp",EDGE,"E12.5.0.52");Q137=makeQuery(id+"F0.imprint","IMPRINT",FACE,{"disambiguationData":[TD([[makeQuery(id+"F0.imprint","IMPRINT",EDGE,{"derivedFrom":subQ4}),1.0]])]});}
            var Q138;
            {var subQ5=sQuery(id+"F0.wireOp",EDGE,"E12.5.0.39");Q138=makeQuery(id+"F0.imprint","IMPRINT",FACE,{"disambiguationData":[TD([[makeQuery(id+"F0.imprint","IMPRINT",EDGE,{"derivedFrom":subQ5}),-1.0]])]});}
            var Q139;
            {var subQ4=sQuery(id+"F0.wireOp",EDGE,"E12.7.0.52");Q139=makeQuery(id+"F0.imprint","IMPRINT",FACE,{"disambiguationData":[TD([[makeQuery(id+"F0.imprint","IMPRINT",EDGE,{"derivedFrom":subQ4}),1.0]])]});}
            var Q140;
            {var subQ5=sQuery(id+"F0.wireOp",EDGE,"E12.7.0.39");Q140=makeQuery(id+"F0.imprint","IMPRINT",FACE,{"disambiguationData":[TD([[makeQuery(id+"F0.imprint","IMPRINT",EDGE,{"derivedFrom":subQ5}),-1.0]])]});}
            var Q141;
            {var subQ4=sQuery(id+"F0.wireOp",EDGE,"E12.6.0.52");Q141=makeQuery(id+"F0.imprint","IMPRINT",FACE,{"disambiguationData":[TD([[makeQuery(id+"F0.imprint","IMPRINT",EDGE,{"derivedFrom":subQ4}),1.0]])]});}
            var Q142;
            {var subQ4=sQuery(id+"F0.wireOp",EDGE,"E12.4.0.50");Q142=makeQuery(id+"F0.imprint","IMPRINT",FACE,{"disambiguationData":[TD([[makeQuery(id+"F0.imprint","IMPRINT",EDGE,{"derivedFrom":subQ4}),1.0]])]});}
            var Q143;
            {var subQ4=sQuery(id+"F0.wireOp",EDGE,"E12.5.0.50");Q143=makeQuery(id+"F0.imprint","IMPRINT",FACE,{"disambiguationData":[TD([[makeQuery(id+"F0.imprint","IMPRINT",EDGE,{"derivedFrom":subQ4}),1.0]])]});}
            var Q144;
            {var subQ4=sQuery(id+"F0.wireOp",EDGE,"E12.7.0.50");Q144=makeQuery(id+"F0.imprint","IMPRINT",FACE,{"disambiguationData":[TD([[makeQuery(id+"F0.imprint","IMPRINT",EDGE,{"derivedFrom":subQ4}),1.0]])]});}
            var Q145;
            {var subQ4=sQuery(id+"F0.wireOp",EDGE,"E12.6.0.50");Q145=makeQuery(id+"F0.imprint","IMPRINT",FACE,{"disambiguationData":[TD([[makeQuery(id+"F0.imprint","IMPRINT",EDGE,{"derivedFrom":subQ4}),1.0]])]});}
            var Q146;
            {var subQ0=sQuery(id+"F0.wireOp",EDGE,"E12.1.0.49");Q146=makeQuery(id+"F0.imprint","IMPRINT",FACE,{"disambiguationData":[TD([[makeQuery(id+"F0.imprint","IMPRINT",EDGE,{"derivedFrom":subQ0}),1.0]])]});}
            var Q147;
            {var subQ0=sQuery(id+"F0.wireOp",EDGE,"E12.3.0.43");Q147=makeQuery(id+"F0.imprint","IMPRINT",FACE,{"disambiguationData":[TD([[makeQuery(id+"F0.imprint","IMPRINT",EDGE,{"derivedFrom":subQ0}),-1.0]])]});}
            var Q148;
            {var subQ5=sQuery(id+"F0.wireOp",EDGE,"E3.right");Q148=makeQuery(id+"F0.imprint","IMPRINT",FACE,{"disambiguationData":[TD([[makeQuery(id+"F0.imprint","IMPRINT",EDGE,{"derivedFrom":subQ5}),-1.0]])]});}
            var Q149;
            {var subQ5=sQuery(id+"F0.wireOp",EDGE,"E11.right");Q149=makeQuery(id+"F0.imprint","IMPRINT",FACE,{"disambiguationData":[TD([[makeQuery(id+"F0.imprint","IMPRINT",EDGE,{"derivedFrom":subQ5}),-1.0]])]});}
            var Q150;
            {var subQ5=sQuery(id+"F0.wireOp",EDGE,"E12.4.0.42");Q150=makeQuery(id+"F0.imprint","IMPRINT",FACE,{"disambiguationData":[TD([[makeQuery(id+"F0.imprint","IMPRINT",EDGE,{"derivedFrom":subQ5}),-1.0]])]});}
            var Q151;
            {var subQ5=sQuery(id+"F0.wireOp",EDGE,"E12.3.0.42");Q151=makeQuery(id+"F0.imprint","IMPRINT",FACE,{"disambiguationData":[TD([[makeQuery(id+"F0.imprint","IMPRINT",EDGE,{"derivedFrom":subQ5}),-1.0]])]});}
            var Q152;
            {var subQ5=sQuery(id+"F0.wireOp",EDGE,"E12.5.0.42");Q152=makeQuery(id+"F0.imprint","IMPRINT",FACE,{"disambiguationData":[TD([[makeQuery(id+"F0.imprint","IMPRINT",EDGE,{"derivedFrom":subQ5}),-1.0]])]});}
            var Q153;
            {var subQ5=sQuery(id+"F0.wireOp",EDGE,"E12.6.0.42");Q153=makeQuery(id+"F0.imprint","IMPRINT",FACE,{"disambiguationData":[TD([[makeQuery(id+"F0.imprint","IMPRINT",EDGE,{"derivedFrom":subQ5}),-1.0]])]});}
            var Q154;
            {var subQ5=sQuery(id+"F0.wireOp",EDGE,"E12.7.0.42");Q154=makeQuery(id+"F0.imprint","IMPRINT",FACE,{"disambiguationData":[TD([[makeQuery(id+"F0.imprint","IMPRINT",EDGE,{"derivedFrom":subQ5}),-1.0]])]});}
            var Q155;
            {var subQ0=sQuery(id+"F0.wireOp",EDGE,"E12.4.0.43");Q155=makeQuery(id+"F0.imprint","IMPRINT",FACE,{"disambiguationData":[TD([[makeQuery(id+"F0.imprint","IMPRINT",EDGE,{"derivedFrom":subQ0}),-1.0]])]});}
            var Q156;
            {var subQ5=sQuery(id+"F0.wireOp",EDGE,"E12.1.0.42");Q156=makeQuery(id+"F0.imprint","IMPRINT",FACE,{"disambiguationData":[TD([[makeQuery(id+"F0.imprint","IMPRINT",EDGE,{"derivedFrom":subQ5}),-1.0]])]});}
            var Q157;
            {var subQ5=sQuery(id+"F0.wireOp",EDGE,"E12.2.0.42");Q157=makeQuery(id+"F0.imprint","IMPRINT",FACE,{"disambiguationData":[TD([[makeQuery(id+"F0.imprint","IMPRINT",EDGE,{"derivedFrom":subQ5}),-1.0]])]});}
            var Q158;
            {var subQ5=sQuery(id+"F0.wireOp",EDGE,"E5.right");Q158=makeQuery(id+"F0.imprint","IMPRINT",FACE,{"disambiguationData":[TD([[makeQuery(id+"F0.imprint","IMPRINT",EDGE,{"derivedFrom":subQ5}),-1.0]])]});}
            var Q159;
            {var subQ5=sQuery(id+"F0.wireOp",EDGE,"E12.6.0.41");Q159=makeQuery(id+"F0.imprint","IMPRINT",FACE,{"disambiguationData":[TD([[makeQuery(id+"F0.imprint","IMPRINT",EDGE,{"derivedFrom":subQ5}),-1.0]])]});}
            var Q160;
            {var subQ5=sQuery(id+"F0.wireOp",EDGE,"E12.7.0.41");Q160=makeQuery(id+"F0.imprint","IMPRINT",FACE,{"disambiguationData":[TD([[makeQuery(id+"F0.imprint","IMPRINT",EDGE,{"derivedFrom":subQ5}),-1.0]])]});}
            var Q161;
            {var subQ0=sQuery(id+"F0.wireOp",EDGE,"E12.5.0.43");Q161=makeQuery(id+"F0.imprint","IMPRINT",FACE,{"disambiguationData":[TD([[makeQuery(id+"F0.imprint","IMPRINT",EDGE,{"derivedFrom":subQ0}),-1.0]])]});}
            var Q162;
            {var subQ0=sQuery(id+"F0.wireOp",EDGE,"E4.left");Q162=makeQuery(id+"F0.imprint","IMPRINT",FACE,{"disambiguationData":[TD([[makeQuery(id+"F0.imprint","IMPRINT",EDGE,{"derivedFrom":subQ0}),1.0]])]});}
            var Q163;
            {var subQ5=sQuery(id+"F0.wireOp",EDGE,"E12.1.0.41");Q163=makeQuery(id+"F0.imprint","IMPRINT",FACE,{"disambiguationData":[TD([[makeQuery(id+"F0.imprint","IMPRINT",EDGE,{"derivedFrom":subQ5}),-1.0]])]});}
            var Q164;
            {var subQ5=sQuery(id+"F0.wireOp",EDGE,"E12.2.0.41");Q164=makeQuery(id+"F0.imprint","IMPRINT",FACE,{"disambiguationData":[TD([[makeQuery(id+"F0.imprint","IMPRINT",EDGE,{"derivedFrom":subQ5}),-1.0]])]});}
            var Q165;
            {var subQ5=sQuery(id+"F0.wireOp",EDGE,"E12.4.0.41");Q165=makeQuery(id+"F0.imprint","IMPRINT",FACE,{"disambiguationData":[TD([[makeQuery(id+"F0.imprint","IMPRINT",EDGE,{"derivedFrom":subQ5}),-1.0]])]});}
            var Q166;
            {var subQ5=sQuery(id+"F0.wireOp",EDGE,"E12.3.0.41");Q166=makeQuery(id+"F0.imprint","IMPRINT",FACE,{"disambiguationData":[TD([[makeQuery(id+"F0.imprint","IMPRINT",EDGE,{"derivedFrom":subQ5}),-1.0]])]});}
            var Q167;
            {var subQ5=sQuery(id+"F0.wireOp",EDGE,"E12.5.0.41");Q167=makeQuery(id+"F0.imprint","IMPRINT",FACE,{"disambiguationData":[TD([[makeQuery(id+"F0.imprint","IMPRINT",EDGE,{"derivedFrom":subQ5}),-1.0]])]});}
            var Q168;
            {var subQ0=sQuery(id+"F0.wireOp",EDGE,"E12.6.0.43");Q168=makeQuery(id+"F0.imprint","IMPRINT",FACE,{"disambiguationData":[TD([[makeQuery(id+"F0.imprint","IMPRINT",EDGE,{"derivedFrom":subQ0}),-1.0]])]});}
            var Q169;
            {var subQ3=sQuery(id+"F0.wireOp",EDGE,"E12.1.0.58");Q169=makeQuery(id+"F0.imprint","IMPRINT",FACE,{"disambiguationData":[TD([[makeQuery(id+"F0.imprint","IMPRINT",EDGE,{"derivedFrom":subQ3}),1.0]])]});}
            var Q170;
            {var subQ0=sQuery(id+"F0.wireOp",EDGE,"E12.7.0.43");Q170=makeQuery(id+"F0.imprint","IMPRINT",FACE,{"disambiguationData":[TD([[makeQuery(id+"F0.imprint","IMPRINT",EDGE,{"derivedFrom":subQ0}),-1.0]])]});}
            var Q171;
            {var subQ5=sQuery(id+"F0.wireOp",EDGE,"E2.right");Q171=makeQuery(id+"F0.imprint","IMPRINT",FACE,{"disambiguationData":[TD([[makeQuery(id+"F0.imprint","IMPRINT",EDGE,{"derivedFrom":subQ5}),-1.0]])]});}
            var Q172;
            {var subQ4=sQuery(id+"F0.wireOp",EDGE,"E12.1.0.50");Q172=makeQuery(id+"F0.imprint","IMPRINT",FACE,{"disambiguationData":[TD([[makeQuery(id+"F0.imprint","IMPRINT",EDGE,{"derivedFrom":subQ4}),1.0]])]});}
            var Q173;
            {var subQ3=sQuery(id+"F0.wireOp",EDGE,"E12.1.0.59");Q173=makeQuery(id+"F0.imprint","IMPRINT",FACE,{"disambiguationData":[TD([[makeQuery(id+"F0.imprint","IMPRINT",EDGE,{"derivedFrom":subQ3}),1.0]])]});}
            var Q174;
            {var subQ5=sQuery(id+"F0.wireOp",EDGE,"E10.right");Q174=makeQuery(id+"F0.imprint","IMPRINT",FACE,{"disambiguationData":[TD([[makeQuery(id+"F0.imprint","IMPRINT",EDGE,{"derivedFrom":subQ5}),-1.0]])]});}
            var Q175;
            {var subQ0=sQuery(id+"F0.wireOp",EDGE,"E12.5.0.49");Q175=makeQuery(id+"F0.imprint","IMPRINT",FACE,{"disambiguationData":[TD([[makeQuery(id+"F0.imprint","IMPRINT",EDGE,{"derivedFrom":subQ0}),1.0]])]});}
            var Q176;
            {var subQ0=sQuery(id+"F0.wireOp",EDGE,"E12.4.0.49");Q176=makeQuery(id+"F0.imprint","IMPRINT",FACE,{"disambiguationData":[TD([[makeQuery(id+"F0.imprint","IMPRINT",EDGE,{"derivedFrom":subQ0}),1.0]])]});}
            var Q177;
            {var subQ0=sQuery(id+"F0.wireOp",EDGE,"E12.6.0.49");Q177=makeQuery(id+"F0.imprint","IMPRINT",FACE,{"disambiguationData":[TD([[makeQuery(id+"F0.imprint","IMPRINT",EDGE,{"derivedFrom":subQ0}),1.0]])]});}
            var Q178;
            {var subQ0=sQuery(id+"F0.wireOp",EDGE,"E12.7.0.49");Q178=makeQuery(id+"F0.imprint","IMPRINT",FACE,{"disambiguationData":[TD([[makeQuery(id+"F0.imprint","IMPRINT",EDGE,{"derivedFrom":subQ0}),1.0]])]});}
            var Q179;
            {var subQ4=sQuery(id+"F0.wireOp",EDGE,"E12.3.0.55");Q179=makeQuery(id+"F0.imprint","IMPRINT",FACE,{"disambiguationData":[TD([[makeQuery(id+"F0.imprint","IMPRINT",EDGE,{"derivedFrom":subQ4}),-1.0]])]});}
            var Q180;
            {var subQ4=sQuery(id+"F0.wireOp",EDGE,"E12.5.0.55");Q180=makeQuery(id+"F0.imprint","IMPRINT",FACE,{"disambiguationData":[TD([[makeQuery(id+"F0.imprint","IMPRINT",EDGE,{"derivedFrom":subQ4}),-1.0]])]});}
            var Q181;
            {var subQ4=sQuery(id+"F0.wireOp",EDGE,"E12.4.0.55");Q181=makeQuery(id+"F0.imprint","IMPRINT",FACE,{"disambiguationData":[TD([[makeQuery(id+"F0.imprint","IMPRINT",EDGE,{"derivedFrom":subQ4}),-1.0]])]});}
            var Q182;
            {var subQ4=sQuery(id+"F0.wireOp",EDGE,"E12.6.0.55");Q182=makeQuery(id+"F0.imprint","IMPRINT",FACE,{"disambiguationData":[TD([[makeQuery(id+"F0.imprint","IMPRINT",EDGE,{"derivedFrom":subQ4}),-1.0]])]});}
            var Q183;
            {var subQ4=sQuery(id+"F0.wireOp",EDGE,"E12.7.0.55");Q183=makeQuery(id+"F0.imprint","IMPRINT",FACE,{"disambiguationData":[TD([[makeQuery(id+"F0.imprint","IMPRINT",EDGE,{"derivedFrom":subQ4}),-1.0]])]});}
            var Q184;
            {var subQ4=sQuery(id+"F0.wireOp",EDGE,"E12.1.0.55");Q184=makeQuery(id+"F0.imprint","IMPRINT",FACE,{"disambiguationData":[TD([[makeQuery(id+"F0.imprint","IMPRINT",EDGE,{"derivedFrom":subQ4}),-1.0]])]});}
            var Q185;
            {var subQ5=sQuery(id+"F0.wireOp",EDGE,"E6.right");Q185=makeQuery(id+"F0.imprint","IMPRINT",FACE,{"disambiguationData":[TD([[makeQuery(id+"F0.imprint","IMPRINT",EDGE,{"derivedFrom":subQ5}),-1.0]])]});}
            var Q186;
            {var subQ3=sQuery(id+"F0.wireOp",EDGE,"E12.2.0.58");Q186=makeQuery(id+"F0.imprint","IMPRINT",FACE,{"disambiguationData":[TD([[makeQuery(id+"F0.imprint","IMPRINT",EDGE,{"derivedFrom":subQ3}),1.0]])]});}
            var Q187;
            {var subQ3=sQuery(id+"F0.wireOp",EDGE,"E12.4.0.58");Q187=makeQuery(id+"F0.imprint","IMPRINT",FACE,{"disambiguationData":[TD([[makeQuery(id+"F0.imprint","IMPRINT",EDGE,{"derivedFrom":subQ3}),1.0]])]});}
            var Q188;
            {var subQ3=sQuery(id+"F0.wireOp",EDGE,"E12.3.0.58");Q188=makeQuery(id+"F0.imprint","IMPRINT",FACE,{"disambiguationData":[TD([[makeQuery(id+"F0.imprint","IMPRINT",EDGE,{"derivedFrom":subQ3}),1.0]])]});}
            var Q189;
            {var subQ3=sQuery(id+"F0.wireOp",EDGE,"E12.5.0.58");Q189=makeQuery(id+"F0.imprint","IMPRINT",FACE,{"disambiguationData":[TD([[makeQuery(id+"F0.imprint","IMPRINT",EDGE,{"derivedFrom":subQ3}),1.0]])]});}
            var Q190;
            {var subQ3=sQuery(id+"F0.wireOp",EDGE,"E12.6.0.58");Q190=makeQuery(id+"F0.imprint","IMPRINT",FACE,{"disambiguationData":[TD([[makeQuery(id+"F0.imprint","IMPRINT",EDGE,{"derivedFrom":subQ3}),1.0]])]});}
            var Q191;
            {var subQ3=sQuery(id+"F0.wireOp",EDGE,"E12.7.0.58");Q191=makeQuery(id+"F0.imprint","IMPRINT",FACE,{"disambiguationData":[TD([[makeQuery(id+"F0.imprint","IMPRINT",EDGE,{"derivedFrom":subQ3}),1.0]])]});}
            var Q192;
            {var subQ0=sQuery(id+"F0.wireOp",EDGE,"E3.left");Q192=makeQuery(id+"F0.imprint","IMPRINT",FACE,{"disambiguationData":[TD([[makeQuery(id+"F0.imprint","IMPRINT",EDGE,{"derivedFrom":subQ0}),1.0]])]});}
            var Q193;
            {var subQ5=sQuery(id+"F0.wireOp",EDGE,"E12.1.0.44");Q193=makeQuery(id+"F0.imprint","IMPRINT",FACE,{"disambiguationData":[TD([[makeQuery(id+"F0.imprint","IMPRINT",EDGE,{"derivedFrom":subQ5}),1.0]])]});}
            var Q194;
            {var subQ3=sQuery(id+"F0.wireOp",EDGE,"E12.2.0.51");Q194=makeQuery(id+"F0.imprint","IMPRINT",FACE,{"disambiguationData":[TD([[makeQuery(id+"F0.imprint","IMPRINT",EDGE,{"derivedFrom":subQ3}),1.0]])]});}
            var Q195;
            {var subQ3=sQuery(id+"F0.wireOp",EDGE,"E12.3.0.48");Q195=makeQuery(id+"F0.imprint","IMPRINT",FACE,{"disambiguationData":[TD([[makeQuery(id+"F0.imprint","IMPRINT",EDGE,{"derivedFrom":subQ3}),1.0]])]});}
            var Q196;
            {var subQ3=sQuery(id+"F0.wireOp",EDGE,"E12.3.0.51");Q196=makeQuery(id+"F0.imprint","IMPRINT",FACE,{"disambiguationData":[TD([[makeQuery(id+"F0.imprint","IMPRINT",EDGE,{"derivedFrom":subQ3}),1.0]])]});}
            var Q197;
            {var subQ3=sQuery(id+"F0.wireOp",EDGE,"E12.2.0.48");Q197=makeQuery(id+"F0.imprint","IMPRINT",FACE,{"disambiguationData":[TD([[makeQuery(id+"F0.imprint","IMPRINT",EDGE,{"derivedFrom":subQ3}),1.0]])]});}
            var Q198;
            {var subQ3=sQuery(id+"F0.wireOp",EDGE,"E12.4.0.48");Q198=makeQuery(id+"F0.imprint","IMPRINT",FACE,{"disambiguationData":[TD([[makeQuery(id+"F0.imprint","IMPRINT",EDGE,{"derivedFrom":subQ3}),1.0]])]});}
            var Q199;
            {var subQ3=sQuery(id+"F0.wireOp",EDGE,"E12.4.0.51");Q199=makeQuery(id+"F0.imprint","IMPRINT",FACE,{"disambiguationData":[TD([[makeQuery(id+"F0.imprint","IMPRINT",EDGE,{"derivedFrom":subQ3}),1.0]])]});}
            var Q200;
            {var subQ3=sQuery(id+"F0.wireOp",EDGE,"E12.6.0.51");Q200=makeQuery(id+"F0.imprint","IMPRINT",FACE,{"disambiguationData":[TD([[makeQuery(id+"F0.imprint","IMPRINT",EDGE,{"derivedFrom":subQ3}),1.0]])]});}
            var Q201;
            {var subQ3=sQuery(id+"F0.wireOp",EDGE,"E12.5.0.48");Q201=makeQuery(id+"F0.imprint","IMPRINT",FACE,{"disambiguationData":[TD([[makeQuery(id+"F0.imprint","IMPRINT",EDGE,{"derivedFrom":subQ3}),1.0]])]});}
            var Q202;
            {var subQ3=sQuery(id+"F0.wireOp",EDGE,"E12.5.0.51");Q202=makeQuery(id+"F0.imprint","IMPRINT",FACE,{"disambiguationData":[TD([[makeQuery(id+"F0.imprint","IMPRINT",EDGE,{"derivedFrom":subQ3}),1.0]])]});}
            var Q203;
            {var subQ3=sQuery(id+"F0.wireOp",EDGE,"E12.7.0.48");Q203=makeQuery(id+"F0.imprint","IMPRINT",FACE,{"disambiguationData":[TD([[makeQuery(id+"F0.imprint","IMPRINT",EDGE,{"derivedFrom":subQ3}),1.0]])]});}
            var Q204;
            {var subQ3=sQuery(id+"F0.wireOp",EDGE,"E12.7.0.51");Q204=makeQuery(id+"F0.imprint","IMPRINT",FACE,{"disambiguationData":[TD([[makeQuery(id+"F0.imprint","IMPRINT",EDGE,{"derivedFrom":subQ3}),1.0]])]});}
            var Q205;
            {var subQ3=sQuery(id+"F0.wireOp",EDGE,"E12.6.0.48");Q205=makeQuery(id+"F0.imprint","IMPRINT",FACE,{"disambiguationData":[TD([[makeQuery(id+"F0.imprint","IMPRINT",EDGE,{"derivedFrom":subQ3}),1.0]])]});}
            var Q206;
            {var subQ5=sQuery(id+"F0.wireOp",EDGE,"E12.3.0.44");Q206=makeQuery(id+"F0.imprint","IMPRINT",FACE,{"disambiguationData":[TD([[makeQuery(id+"F0.imprint","IMPRINT",EDGE,{"derivedFrom":subQ5}),1.0]])]});}
            var Q207;
            {var subQ0=sQuery(id+"F0.wireOp",EDGE,"E12.2.0.43");Q207=makeQuery(id+"F0.imprint","IMPRINT",FACE,{"disambiguationData":[TD([[makeQuery(id+"F0.imprint","IMPRINT",EDGE,{"derivedFrom":subQ0}),-1.0]])]});}
            var Q208;
            {var subQ4=sQuery(id+"F0.wireOp",EDGE,"E12.3.0.50");Q208=makeQuery(id+"F0.imprint","IMPRINT",FACE,{"disambiguationData":[TD([[makeQuery(id+"F0.imprint","IMPRINT",EDGE,{"derivedFrom":subQ4}),1.0]])]});}
            var Q209;
            {var subQ4=sQuery(id+"F0.wireOp",EDGE,"E12.2.0.50");Q209=makeQuery(id+"F0.imprint","IMPRINT",FACE,{"disambiguationData":[TD([[makeQuery(id+"F0.imprint","IMPRINT",EDGE,{"derivedFrom":subQ4}),1.0]])]});}
            var Q210;
            {var subQ0=sQuery(id+"F0.wireOp",EDGE,"E12.2.0.49");Q210=makeQuery(id+"F0.imprint","IMPRINT",FACE,{"disambiguationData":[TD([[makeQuery(id+"F0.imprint","IMPRINT",EDGE,{"derivedFrom":subQ0}),1.0]])]});}
            var Q211;
            {var subQ3=sQuery(id+"F0.wireOp",EDGE,"E12.4.0.59");Q211=makeQuery(id+"F0.imprint","IMPRINT",FACE,{"disambiguationData":[TD([[makeQuery(id+"F0.imprint","IMPRINT",EDGE,{"derivedFrom":subQ3}),1.0]])]});}
            var Q212;
            {var subQ0=sQuery(id+"F0.wireOp",EDGE,"E12.3.0.49");Q212=makeQuery(id+"F0.imprint","IMPRINT",FACE,{"disambiguationData":[TD([[makeQuery(id+"F0.imprint","IMPRINT",EDGE,{"derivedFrom":subQ0}),1.0]])]});}
            var Q213;
            {var subQ3=sQuery(id+"F0.wireOp",EDGE,"E12.5.0.59");Q213=makeQuery(id+"F0.imprint","IMPRINT",FACE,{"disambiguationData":[TD([[makeQuery(id+"F0.imprint","IMPRINT",EDGE,{"derivedFrom":subQ3}),1.0]])]});}
            var Q214;
            {var subQ3=sQuery(id+"F0.wireOp",EDGE,"E12.6.0.59");Q214=makeQuery(id+"F0.imprint","IMPRINT",FACE,{"disambiguationData":[TD([[makeQuery(id+"F0.imprint","IMPRINT",EDGE,{"derivedFrom":subQ3}),1.0]])]});}
            var Q215;
            {var subQ3=sQuery(id+"F0.wireOp",EDGE,"E12.7.0.59");Q215=makeQuery(id+"F0.imprint","IMPRINT",FACE,{"disambiguationData":[TD([[makeQuery(id+"F0.imprint","IMPRINT",EDGE,{"derivedFrom":subQ3}),1.0]])]});}
            var Q216;
            {var subQ4=sQuery(id+"F0.wireOp",EDGE,"E12.2.0.55");Q216=makeQuery(id+"F0.imprint","IMPRINT",FACE,{"disambiguationData":[TD([[makeQuery(id+"F0.imprint","IMPRINT",EDGE,{"derivedFrom":subQ4}),-1.0]])]});}
            var Q217;
            {var subQ5=sQuery(id+"F0.wireOp",EDGE,"E12.2.0.44");Q217=makeQuery(id+"F0.imprint","IMPRINT",FACE,{"disambiguationData":[TD([[makeQuery(id+"F0.imprint","IMPRINT",EDGE,{"derivedFrom":subQ5}),1.0]])]});}
            var Q218;
            {var subQ5=sQuery(id+"F0.wireOp",EDGE,"E12.5.0.44");Q218=makeQuery(id+"F0.imprint","IMPRINT",FACE,{"disambiguationData":[TD([[makeQuery(id+"F0.imprint","IMPRINT",EDGE,{"derivedFrom":subQ5}),1.0]])]});}
            var Q219;
            {var subQ3=sQuery(id+"F0.wireOp",EDGE,"E12.2.0.59");Q219=makeQuery(id+"F0.imprint","IMPRINT",FACE,{"disambiguationData":[TD([[makeQuery(id+"F0.imprint","IMPRINT",EDGE,{"derivedFrom":subQ3}),1.0]])]});}
            var Q220;
            {var subQ3=sQuery(id+"F0.wireOp",EDGE,"E12.3.0.59");Q220=makeQuery(id+"F0.imprint","IMPRINT",FACE,{"disambiguationData":[TD([[makeQuery(id+"F0.imprint","IMPRINT",EDGE,{"derivedFrom":subQ3}),1.0]])]});}
            var Q221;
            {var subQ5=sQuery(id+"F0.wireOp",EDGE,"E12.6.0.44");Q221=makeQuery(id+"F0.imprint","IMPRINT",FACE,{"disambiguationData":[TD([[makeQuery(id+"F0.imprint","IMPRINT",EDGE,{"derivedFrom":subQ5}),1.0]])]});}
            var Q222;
            {var subQ5=sQuery(id+"F0.wireOp",EDGE,"E12.4.0.44");Q222=makeQuery(id+"F0.imprint","IMPRINT",FACE,{"disambiguationData":[TD([[makeQuery(id+"F0.imprint","IMPRINT",EDGE,{"derivedFrom":subQ5}),1.0]])]});}
            var Q223;
            {var subQ5=sQuery(id+"F0.wireOp",EDGE,"E12.7.0.44");Q223=makeQuery(id+"F0.imprint","IMPRINT",FACE,{"disambiguationData":[TD([[makeQuery(id+"F0.imprint","IMPRINT",EDGE,{"derivedFrom":subQ5}),1.0]])]});}
            extrude(context, id + "F1", {"entities" : qUnion([Q0, Q1, Q2, Q3, Q4, Q5, Q6, Q7, Q8, Q9, Q10, Q11, Q12, Q13, Q14, Q15, Q16, Q17, Q18, Q19, Q20, Q21, Q22, Q23, Q24, Q25, Q26, Q27, Q28, Q29, Q30, Q31, Q32, Q33, Q34, Q35, Q36, Q37, Q38, Q39, Q40, Q41, Q42, Q43, Q44, Q45, Q46, Q47, Q48, Q49, Q50, Q51, Q52, Q53, Q54, Q55, Q56, Q57, Q58, Q59, Q60, Q61, Q62, Q63, Q64, Q65, Q66, Q67, Q68, Q69, Q70, Q71, Q72, Q73, Q74, Q75, Q76, Q77, Q78, Q79, Q80, Q81, Q82, Q83, Q84, Q85, Q86, Q87, Q88, Q89, Q90, Q91, Q92, Q93, Q94, Q95, Q96, Q97, Q98, Q99, Q100, Q101, Q102, Q103, Q104, Q105, Q106, Q107, Q108, Q109, Q110, Q111, Q112, Q113, Q114, Q115, Q116, Q117, Q118, Q119, Q120, Q121, Q122, Q123, Q124, Q125, Q126, Q127, Q128, Q129, Q130, Q131, Q132, Q133, Q134, Q135, Q136, Q137, Q138, Q139, Q140, Q141, Q142, Q143, Q144, Q145, Q146, Q147, Q148, Q149, Q150, Q151, Q152, Q153, Q154, Q155, Q156, Q157, Q158, Q159, Q160, Q161, Q162, Q163, Q164, Q165, Q166, Q167, Q168, Q169, Q170, Q171, Q172, Q173, Q174, Q175, Q176, Q177, Q178, Q179, Q180, Q181, Q182, Q183, Q184, Q185, Q186, Q187, Q188, Q189, Q190, Q191, Q192, Q193, Q194, Q195, Q196, Q197, Q198, Q199, Q200, Q201, Q202, Q203, Q204, Q205, Q206, Q207, Q208, Q209, Q210, Q211, Q212, Q213, Q214, Q215, Q216, Q217, Q218, Q219, Q220, Q221, Q222, Q223]), "depth" : 0.25 * mm, "offsetDistance" : 25.4 * mm});
        }
    });
